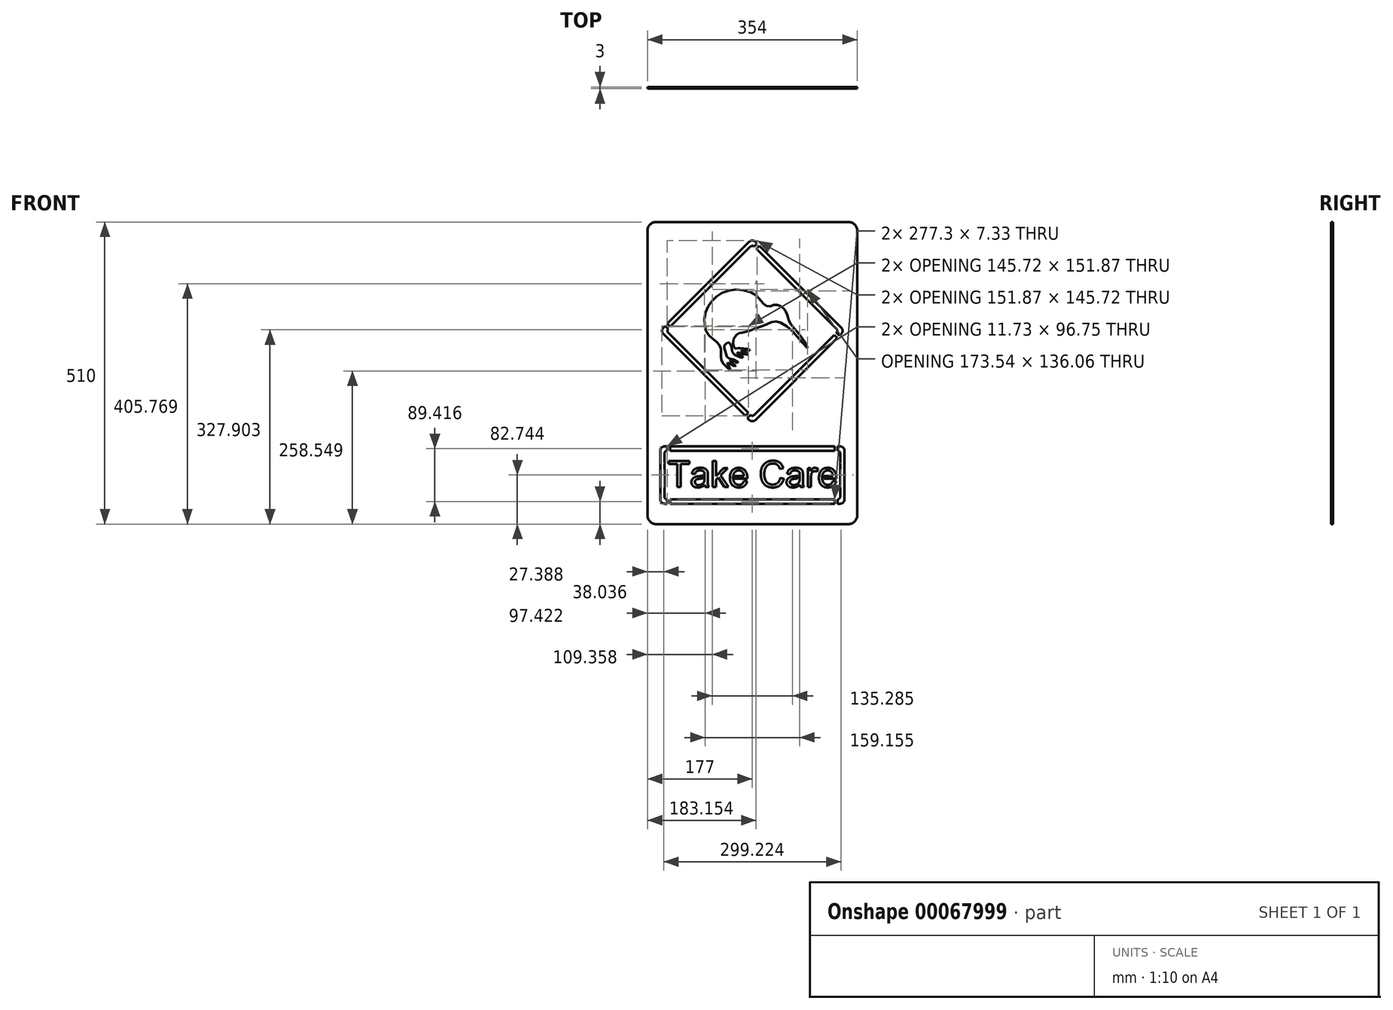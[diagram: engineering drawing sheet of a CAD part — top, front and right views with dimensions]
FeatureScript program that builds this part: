
annotation { "Feature Type Name" : "Feature", "Feature Type Description" : "" }
export const myFeature = defineFeature(function(context is Context, id is Id, definition is map)
    precondition{}
    {
        {
            var Q0;
            Q0=qCreatedBy(makeId("Front.planeOp"),FACE);
            var sketch = newSketch(context, id + "F0", { "sketchPlane" : qUnion([Q0])});
            skLineSegment(sketch, "E0", {"start": v(-162, 255) * mm, "end": v(162, 255) * mm});
            skArc(sketch, "E1", {"start": v(-162, 255) * mm, "mid": v(-172.6, 250.6) * mm, "end": v(-177, 240) * mm});
            skLineSegment(sketch, "E2", {"start": v(-177, -240) * mm, "end": v(-177, 240) * mm});
            skArc(sketch, "E3", {"start": v(-177, -240) * mm, "mid": v(-172.6, -250.6) * mm, "end": v(-162, -255) * mm});
            skLineSegment(sketch, "E4", {"start": v(-162, -255) * mm, "end": v(162, -255) * mm});
            skArc(sketch, "E5", {"start": v(162, -255) * mm, "mid": v(172.6, -250.6) * mm, "end": v(177, -240) * mm});
            skLineSegment(sketch, "E6", {"start": v(177, -240) * mm, "end": v(177, 240) * mm});
            skArc(sketch, "E7", {"start": v(177, 240) * mm, "mid": v(172.6, 250.6) * mm, "end": v(162, 255) * mm});
            skLineSegment(sketch, "E8", {"start": v(121.2, -173.58) * mm, "end": v(136, -173.58) * mm});
            skLineSegment(sketch, "E9", {"start": v(136, -173.58) * mm, "end": v(135.95, -173.09) * mm});
            skLineSegment(sketch, "E10", {"start": v(135.95, -173.09) * mm, "end": v(135.9, -172.61) * mm});
            skLineSegment(sketch, "E11", {"start": v(135.9, -172.61) * mm, "end": v(135.82, -172.15) * mm});
            skLineSegment(sketch, "E12", {"start": v(135.82, -172.15) * mm, "end": v(135.74, -171.7) * mm});
            skLineSegment(sketch, "E13", {"start": v(135.74, -171.7) * mm, "end": v(135.65, -171.27) * mm});
            skLineSegment(sketch, "E14", {"start": v(135.65, -171.27) * mm, "end": v(135.55, -170.85) * mm});
            skLineSegment(sketch, "E15", {"start": v(135.55, -170.85) * mm, "end": v(135.44, -170.45) * mm});
            skLineSegment(sketch, "E16", {"start": v(135.44, -170.45) * mm, "end": v(135.31, -170.07) * mm});
            skLineSegment(sketch, "E17", {"start": v(135.31, -170.07) * mm, "end": v(135.18, -169.7) * mm});
            skLineSegment(sketch, "E18", {"start": v(135.18, -169.7) * mm, "end": v(135.04, -169.34) * mm});
            skLineSegment(sketch, "E19", {"start": v(135.04, -169.34) * mm, "end": v(134.89, -169) * mm});
            skLineSegment(sketch, "E20", {"start": v(134.89, -169) * mm, "end": v(134.72, -168.69) * mm});
            skLineSegment(sketch, "E21", {"start": v(134.72, -168.69) * mm, "end": v(134.55, -168.38) * mm});
            skLineSegment(sketch, "E22", {"start": v(134.55, -168.38) * mm, "end": v(134.36, -168.09) * mm});
            skLineSegment(sketch, "E23", {"start": v(134.36, -168.09) * mm, "end": v(134.17, -167.81) * mm});
            skLineSegment(sketch, "E24", {"start": v(134.17, -167.81) * mm, "end": v(133.96, -167.55) * mm});
            skLineSegment(sketch, "E25", {"start": v(133.96, -167.55) * mm, "end": v(133.64, -167.18) * mm});
            skLineSegment(sketch, "E26", {"start": v(133.64, -167.18) * mm, "end": v(133.3, -166.82) * mm});
            skLineSegment(sketch, "E27", {"start": v(133.3, -166.82) * mm, "end": v(132.94, -166.5) * mm});
            skLineSegment(sketch, "E28", {"start": v(132.94, -166.5) * mm, "end": v(132.58, -166.2) * mm});
            skLineSegment(sketch, "E29", {"start": v(132.58, -166.2) * mm, "end": v(132.2, -165.9) * mm});
            skLineSegment(sketch, "E30", {"start": v(132.2, -165.9) * mm, "end": v(131.82, -165.65) * mm});
            skLineSegment(sketch, "E31", {"start": v(131.82, -165.65) * mm, "end": v(131.41, -165.42) * mm});
            skLineSegment(sketch, "E32", {"start": v(131.41, -165.42) * mm, "end": v(131, -165.22) * mm});
            skLineSegment(sketch, "E33", {"start": v(131, -165.22) * mm, "end": v(130.58, -165.03) * mm});
            skLineSegment(sketch, "E34", {"start": v(130.58, -165.03) * mm, "end": v(130.14, -164.87) * mm});
            skLineSegment(sketch, "E35", {"start": v(130.14, -164.87) * mm, "end": v(129.7, -164.74) * mm});
            skLineSegment(sketch, "E36", {"start": v(129.7, -164.74) * mm, "end": v(129.23, -164.63) * mm});
            skLineSegment(sketch, "E37", {"start": v(129.23, -164.63) * mm, "end": v(128.76, -164.54) * mm});
            skLineSegment(sketch, "E38", {"start": v(128.76, -164.54) * mm, "end": v(128.28, -164.48) * mm});
            skLineSegment(sketch, "E39", {"start": v(128.28, -164.48) * mm, "end": v(127.78, -164.45) * mm});
            skLineSegment(sketch, "E40", {"start": v(127.78, -164.45) * mm, "end": v(127.28, -164.44) * mm});
            skLineSegment(sketch, "E41", {"start": v(127.28, -164.44) * mm, "end": v(126.82, -164.44) * mm});
            skLineSegment(sketch, "E42", {"start": v(126.82, -164.44) * mm, "end": v(126.36, -164.47) * mm});
            skLineSegment(sketch, "E43", {"start": v(126.36, -164.47) * mm, "end": v(125.92, -164.52) * mm});
            skLineSegment(sketch, "E44", {"start": v(125.92, -164.52) * mm, "end": v(125.49, -164.6) * mm});
            skLineSegment(sketch, "E45", {"start": v(125.49, -164.6) * mm, "end": v(125.07, -164.68) * mm});
            skLineSegment(sketch, "E46", {"start": v(125.07, -164.68) * mm, "end": v(124.65, -164.79) * mm});
            skLineSegment(sketch, "E47", {"start": v(124.65, -164.79) * mm, "end": v(124.25, -164.91) * mm});
            skLineSegment(sketch, "E48", {"start": v(124.25, -164.91) * mm, "end": v(123.85, -165.06) * mm});
            skLineSegment(sketch, "E49", {"start": v(123.85, -165.06) * mm, "end": v(123.47, -165.22) * mm});
            skLineSegment(sketch, "E50", {"start": v(123.47, -165.22) * mm, "end": v(123.09, -165.4) * mm});
            skLineSegment(sketch, "E51", {"start": v(123.09, -165.4) * mm, "end": v(122.72, -165.61) * mm});
            skLineSegment(sketch, "E52", {"start": v(122.72, -165.61) * mm, "end": v(122.36, -165.84) * mm});
            skLineSegment(sketch, "E53", {"start": v(122.36, -165.84) * mm, "end": v(122.01, -166.08) * mm});
            skLineSegment(sketch, "E54", {"start": v(122.01, -166.08) * mm, "end": v(121.67, -166.34) * mm});
            skLineSegment(sketch, "E55", {"start": v(121.67, -166.34) * mm, "end": v(121.34, -166.62) * mm});
            skLineSegment(sketch, "E56", {"start": v(121.34, -166.62) * mm, "end": v(121.02, -166.92) * mm});
            skLineSegment(sketch, "E57", {"start": v(121.02, -166.92) * mm, "end": v(120.71, -167.24) * mm});
            skLineSegment(sketch, "E58", {"start": v(120.71, -167.24) * mm, "end": v(120.42, -167.57) * mm});
            skLineSegment(sketch, "E59", {"start": v(120.42, -167.57) * mm, "end": v(120.15, -167.92) * mm});
            skLineSegment(sketch, "E60", {"start": v(120.15, -167.92) * mm, "end": v(119.9, -168.27) * mm});
            skLineSegment(sketch, "E61", {"start": v(119.9, -168.27) * mm, "end": v(119.66, -168.65) * mm});
            skLineSegment(sketch, "E62", {"start": v(119.66, -168.65) * mm, "end": v(119.44, -169.03) * mm});
            skLineSegment(sketch, "E63", {"start": v(119.44, -169.03) * mm, "end": v(119.24, -169.42) * mm});
            skLineSegment(sketch, "E64", {"start": v(119.24, -169.42) * mm, "end": v(119.05, -169.83) * mm});
            skArc(sketch, "E65", {"start": v(119.05, -169.83) * mm, "mid": v(117.86, -176.49) * mm, "end": v(119, -183.15) * mm});
            skLineSegment(sketch, "E66", {"start": v(119, -183.15) * mm, "end": v(119.45, -184.08) * mm});
            skLineSegment(sketch, "E67", {"start": v(119.45, -184.08) * mm, "end": v(119.7, -184.51) * mm});
            skLineSegment(sketch, "E68", {"start": v(119.7, -184.51) * mm, "end": v(119.97, -184.93) * mm});
            skLineSegment(sketch, "E69", {"start": v(119.97, -184.93) * mm, "end": v(120.26, -185.33) * mm});
            skLineSegment(sketch, "E70", {"start": v(120.26, -185.33) * mm, "end": v(120.56, -185.7) * mm});
            skLineSegment(sketch, "E71", {"start": v(120.56, -185.7) * mm, "end": v(120.89, -186.06) * mm});
            skLineSegment(sketch, "E72", {"start": v(120.89, -186.06) * mm, "end": v(121.23, -186.4) * mm});
            skLineSegment(sketch, "E73", {"start": v(121.23, -186.4) * mm, "end": v(121.57, -186.72) * mm});
            skLineSegment(sketch, "E74", {"start": v(121.57, -186.72) * mm, "end": v(121.93, -187.01) * mm});
            skLineSegment(sketch, "E75", {"start": v(121.93, -187.01) * mm, "end": v(122.3, -187.28) * mm});
            skLineSegment(sketch, "E76", {"start": v(122.3, -187.28) * mm, "end": v(122.68, -187.53) * mm});
            skLineSegment(sketch, "E77", {"start": v(122.68, -187.53) * mm, "end": v(123.07, -187.76) * mm});
            skLineSegment(sketch, "E78", {"start": v(123.07, -187.76) * mm, "end": v(123.48, -187.97) * mm});
            skLineSegment(sketch, "E79", {"start": v(123.48, -187.97) * mm, "end": v(123.89, -188.16) * mm});
            skLineSegment(sketch, "E80", {"start": v(123.89, -188.16) * mm, "end": v(124.3, -188.32) * mm});
            skLineSegment(sketch, "E81", {"start": v(124.3, -188.32) * mm, "end": v(124.74, -188.46) * mm});
            skLineSegment(sketch, "E82", {"start": v(124.74, -188.46) * mm, "end": v(125.18, -188.58) * mm});
            skLineSegment(sketch, "E83", {"start": v(125.18, -188.58) * mm, "end": v(125.63, -188.68) * mm});
            skLineSegment(sketch, "E84", {"start": v(125.63, -188.68) * mm, "end": v(126.1, -188.75) * mm});
            skLineSegment(sketch, "E85", {"start": v(126.1, -188.75) * mm, "end": v(126.57, -188.8) * mm});
            skLineSegment(sketch, "E86", {"start": v(126.57, -188.8) * mm, "end": v(127.05, -188.84) * mm});
            skLineSegment(sketch, "E87", {"start": v(127.05, -188.84) * mm, "end": v(127.55, -188.85) * mm});
            skLineSegment(sketch, "E88", {"start": v(127.55, -188.85) * mm, "end": v(128.27, -188.83) * mm});
            skLineSegment(sketch, "E89", {"start": v(128.27, -188.83) * mm, "end": v(128.98, -188.75) * mm});
            skLineSegment(sketch, "E90", {"start": v(128.98, -188.75) * mm, "end": v(129.65, -188.63) * mm});
            skLineSegment(sketch, "E91", {"start": v(129.65, -188.63) * mm, "end": v(130.3, -188.46) * mm});
            skLineSegment(sketch, "E92", {"start": v(130.3, -188.46) * mm, "end": v(130.92, -188.24) * mm});
            skLineSegment(sketch, "E93", {"start": v(130.92, -188.24) * mm, "end": v(131.51, -187.98) * mm});
            skLineSegment(sketch, "E94", {"start": v(131.51, -187.98) * mm, "end": v(132.08, -187.66) * mm});
            skLineSegment(sketch, "E95", {"start": v(132.08, -187.66) * mm, "end": v(132.62, -187.3) * mm});
            skLineSegment(sketch, "E96", {"start": v(132.62, -187.3) * mm, "end": v(133.13, -186.87) * mm});
            skLineSegment(sketch, "E97", {"start": v(133.13, -186.87) * mm, "end": v(133.61, -186.4) * mm});
            skLineSegment(sketch, "E98", {"start": v(133.61, -186.4) * mm, "end": v(134.07, -185.86) * mm});
            skLineSegment(sketch, "E99", {"start": v(134.07, -185.86) * mm, "end": v(134.5, -185.27) * mm});
            skLineSegment(sketch, "E100", {"start": v(134.5, -185.27) * mm, "end": v(134.9, -184.62) * mm});
            skLineSegment(sketch, "E101", {"start": v(134.9, -184.62) * mm, "end": v(135.28, -183.9) * mm});
            skLineSegment(sketch, "E102", {"start": v(135.28, -183.9) * mm, "end": v(135.62, -183.14) * mm});
            skLineSegment(sketch, "E103", {"start": v(135.62, -183.14) * mm, "end": v(135.94, -182.31) * mm});
            skLineSegment(sketch, "E104", {"start": v(135.94, -182.31) * mm, "end": v(141.52, -183) * mm});
            skLineSegment(sketch, "E105", {"start": v(141.52, -183) * mm, "end": v(141.35, -183.6) * mm});
            skLineSegment(sketch, "E106", {"start": v(141.35, -183.6) * mm, "end": v(141.16, -184.2) * mm});
            skLineSegment(sketch, "E107", {"start": v(141.16, -184.2) * mm, "end": v(140.95, -184.76) * mm});
            skLineSegment(sketch, "E108", {"start": v(140.95, -184.76) * mm, "end": v(140.72, -185.31) * mm});
            skLineSegment(sketch, "E109", {"start": v(140.72, -185.31) * mm, "end": v(140.48, -185.85) * mm});
            skLineSegment(sketch, "E110", {"start": v(140.48, -185.85) * mm, "end": v(140.22, -186.36) * mm});
            skLineSegment(sketch, "E111", {"start": v(140.22, -186.36) * mm, "end": v(139.94, -186.86) * mm});
            skLineSegment(sketch, "E112", {"start": v(139.94, -186.86) * mm, "end": v(139.64, -187.35) * mm});
            skLineSegment(sketch, "E113", {"start": v(139.64, -187.35) * mm, "end": v(139.33, -187.81) * mm});
            skLineSegment(sketch, "E114", {"start": v(139.33, -187.81) * mm, "end": v(139, -188.26) * mm});
            skLineSegment(sketch, "E115", {"start": v(139, -188.26) * mm, "end": v(138.65, -188.7) * mm});
            skLineSegment(sketch, "E116", {"start": v(138.65, -188.7) * mm, "end": v(138.28, -189.1) * mm});
            skLineSegment(sketch, "E117", {"start": v(138.28, -189.1) * mm, "end": v(137.9, -189.5) * mm});
            skLineSegment(sketch, "E118", {"start": v(137.9, -189.5) * mm, "end": v(137.5, -189.88) * mm});
            skLineSegment(sketch, "E119", {"start": v(137.5, -189.88) * mm, "end": v(137.07, -190.25) * mm});
            skLineSegment(sketch, "E120", {"start": v(137.07, -190.25) * mm, "end": v(136.63, -190.6) * mm});
            skLineSegment(sketch, "E121", {"start": v(136.63, -190.6) * mm, "end": v(136.18, -190.92) * mm});
            skLineSegment(sketch, "E122", {"start": v(136.18, -190.92) * mm, "end": v(135.71, -191.23) * mm});
            skLineSegment(sketch, "E123", {"start": v(135.71, -191.23) * mm, "end": v(135.23, -191.5) * mm});
            skLineSegment(sketch, "E124", {"start": v(135.23, -191.5) * mm, "end": v(134.73, -191.77) * mm});
            skLineSegment(sketch, "E125", {"start": v(134.73, -191.77) * mm, "end": v(134.21, -192.02) * mm});
            skLineSegment(sketch, "E126", {"start": v(134.21, -192.02) * mm, "end": v(133.68, -192.24) * mm});
            skLineSegment(sketch, "E127", {"start": v(133.68, -192.24) * mm, "end": v(133.13, -192.44) * mm});
            skLineSegment(sketch, "E128", {"start": v(133.13, -192.44) * mm, "end": v(132.57, -192.62) * mm});
            skLineSegment(sketch, "E129", {"start": v(132.57, -192.62) * mm, "end": v(132, -192.78) * mm});
            skLineSegment(sketch, "E130", {"start": v(132, -192.78) * mm, "end": v(131.4, -192.91) * mm});
            skLineSegment(sketch, "E131", {"start": v(131.4, -192.91) * mm, "end": v(130.8, -193.03) * mm});
            skLineSegment(sketch, "E132", {"start": v(130.8, -193.03) * mm, "end": v(130.17, -193.12) * mm});
            skLineSegment(sketch, "E133", {"start": v(130.17, -193.12) * mm, "end": v(129.53, -193.2) * mm});
            skLineSegment(sketch, "E134", {"start": v(129.53, -193.2) * mm, "end": v(128.87, -193.25) * mm});
            skLineSegment(sketch, "E135", {"start": v(128.87, -193.25) * mm, "end": v(128.2, -193.28) * mm});
            skLineSegment(sketch, "E136", {"start": v(128.2, -193.28) * mm, "end": v(127.52, -193.3) * mm});
            skLineSegment(sketch, "E137", {"start": v(127.52, -193.3) * mm, "end": v(126.65, -193.28) * mm});
            skLineSegment(sketch, "E138", {"start": v(126.65, -193.28) * mm, "end": v(125.81, -193.22) * mm});
            skLineSegment(sketch, "E139", {"start": v(125.81, -193.22) * mm, "end": v(125, -193.14) * mm});
            skLineSegment(sketch, "E140", {"start": v(125, -193.14) * mm, "end": v(124.2, -193.02) * mm});
            skLineSegment(sketch, "E141", {"start": v(124.2, -193.02) * mm, "end": v(123.43, -192.87) * mm});
            skLineSegment(sketch, "E142", {"start": v(123.43, -192.87) * mm, "end": v(122.68, -192.69) * mm});
            skLineSegment(sketch, "E143", {"start": v(122.68, -192.69) * mm, "end": v(121.95, -192.47) * mm});
            skLineSegment(sketch, "E144", {"start": v(121.95, -192.47) * mm, "end": v(121.25, -192.22) * mm});
            skLineSegment(sketch, "E145", {"start": v(121.25, -192.22) * mm, "end": v(120.57, -191.93) * mm});
            skLineSegment(sketch, "E146", {"start": v(120.57, -191.93) * mm, "end": v(119.9, -191.61) * mm});
            skLineSegment(sketch, "E147", {"start": v(119.9, -191.61) * mm, "end": v(119.27, -191.26) * mm});
            skLineSegment(sketch, "E148", {"start": v(119.27, -191.26) * mm, "end": v(118.66, -190.87) * mm});
            skLineSegment(sketch, "E149", {"start": v(118.66, -190.87) * mm, "end": v(118.07, -190.45) * mm});
            skLineSegment(sketch, "E150", {"start": v(118.07, -190.45) * mm, "end": v(117.5, -190) * mm});
            skLineSegment(sketch, "E151", {"start": v(117.5, -190) * mm, "end": v(116.96, -189.5) * mm});
            skLineSegment(sketch, "E152", {"start": v(116.96, -189.5) * mm, "end": v(116.43, -188.99) * mm});
            skLineSegment(sketch, "E153", {"start": v(116.43, -188.99) * mm, "end": v(115.94, -188.44) * mm});
            skLineSegment(sketch, "E154", {"start": v(115.94, -188.44) * mm, "end": v(115.47, -187.86) * mm});
            skLineSegment(sketch, "E155", {"start": v(115.47, -187.86) * mm, "end": v(115.04, -187.25) * mm});
            skLineSegment(sketch, "E156", {"start": v(115.04, -187.25) * mm, "end": v(114.64, -186.62) * mm});
            skLineSegment(sketch, "E157", {"start": v(114.64, -186.62) * mm, "end": v(114.27, -185.96) * mm});
            skLineSegment(sketch, "E158", {"start": v(114.27, -185.96) * mm, "end": v(113.94, -185.27) * mm});
            skLineSegment(sketch, "E159", {"start": v(113.94, -185.27) * mm, "end": v(113.63, -184.56) * mm});
            skLineSegment(sketch, "E160", {"start": v(113.63, -184.56) * mm, "end": v(113.36, -183.82) * mm});
            skLineSegment(sketch, "E161", {"start": v(113.36, -183.82) * mm, "end": v(113.12, -183.05) * mm});
            skLineSegment(sketch, "E162", {"start": v(113.12, -183.05) * mm, "end": v(112.91, -182.25) * mm});
            skLineSegment(sketch, "E163", {"start": v(112.91, -182.25) * mm, "end": v(112.74, -181.43) * mm});
            skLineSegment(sketch, "E164", {"start": v(112.74, -181.43) * mm, "end": v(112.6, -180.58) * mm});
            skLineSegment(sketch, "E165", {"start": v(112.6, -180.58) * mm, "end": v(112.48, -179.7) * mm});
            skLineSegment(sketch, "E166", {"start": v(112.48, -179.7) * mm, "end": v(112.4, -178.8) * mm});
            skLineSegment(sketch, "E167", {"start": v(112.4, -178.8) * mm, "end": v(112.35, -177.87) * mm});
            skLineSegment(sketch, "E168", {"start": v(112.35, -177.87) * mm, "end": v(112.34, -176.91) * mm});
            skLineSegment(sketch, "E169", {"start": v(112.34, -176.91) * mm, "end": v(112.35, -175.92) * mm});
            skLineSegment(sketch, "E170", {"start": v(112.35, -175.92) * mm, "end": v(112.4, -174.96) * mm});
            skLineSegment(sketch, "E171", {"start": v(112.4, -174.96) * mm, "end": v(112.48, -174.03) * mm});
            skLineSegment(sketch, "E172", {"start": v(112.48, -174.03) * mm, "end": v(112.6, -173.12) * mm});
            skLineSegment(sketch, "E173", {"start": v(112.6, -173.12) * mm, "end": v(112.74, -172.24) * mm});
            skLineSegment(sketch, "E174", {"start": v(112.74, -172.24) * mm, "end": v(112.92, -171.4) * mm});
            skLineSegment(sketch, "E175", {"start": v(112.92, -171.4) * mm, "end": v(113.13, -170.57) * mm});
            skLineSegment(sketch, "E176", {"start": v(113.13, -170.57) * mm, "end": v(113.37, -169.77) * mm});
            skLineSegment(sketch, "E177", {"start": v(113.37, -169.77) * mm, "end": v(113.65, -169) * mm});
            skLineSegment(sketch, "E178", {"start": v(113.65, -169) * mm, "end": v(113.95, -168.27) * mm});
            skLineSegment(sketch, "E179", {"start": v(113.95, -168.27) * mm, "end": v(114.3, -167.56) * mm});
            skLineSegment(sketch, "E180", {"start": v(114.3, -167.56) * mm, "end": v(114.67, -166.88) * mm});
            skLineSegment(sketch, "E181", {"start": v(114.67, -166.88) * mm, "end": v(115.07, -166.23) * mm});
            skLineSegment(sketch, "E182", {"start": v(115.07, -166.23) * mm, "end": v(115.5, -165.6) * mm});
            skLineSegment(sketch, "E183", {"start": v(115.5, -165.6) * mm, "end": v(115.98, -165) * mm});
            skLineSegment(sketch, "E184", {"start": v(115.98, -165) * mm, "end": v(116.48, -164.44) * mm});
            skLineSegment(sketch, "E185", {"start": v(116.48, -164.44) * mm, "end": v(117, -163.9) * mm});
            skLineSegment(sketch, "E186", {"start": v(117, -163.9) * mm, "end": v(117.55, -163.4) * mm});
            skLineSegment(sketch, "E187", {"start": v(117.55, -163.4) * mm, "end": v(118.12, -162.93) * mm});
            skLineSegment(sketch, "E188", {"start": v(118.12, -162.93) * mm, "end": v(118.7, -162.5) * mm});
            skLineSegment(sketch, "E189", {"start": v(118.7, -162.5) * mm, "end": v(119.3, -162.1) * mm});
            skLineSegment(sketch, "E190", {"start": v(119.3, -162.1) * mm, "end": v(119.93, -161.73) * mm});
            skLineSegment(sketch, "E191", {"start": v(119.93, -161.73) * mm, "end": v(120.57, -161.4) * mm});
            skLineSegment(sketch, "E192", {"start": v(120.57, -161.4) * mm, "end": v(121.23, -161.1) * mm});
            skLineSegment(sketch, "E193", {"start": v(121.23, -161.1) * mm, "end": v(121.91, -160.85) * mm});
            skLineSegment(sketch, "E194", {"start": v(121.91, -160.85) * mm, "end": v(122.61, -160.62) * mm});
            skLineSegment(sketch, "E195", {"start": v(122.61, -160.62) * mm, "end": v(123.33, -160.43) * mm});
            skLineSegment(sketch, "E196", {"start": v(123.33, -160.43) * mm, "end": v(124.07, -160.27) * mm});
            skLineSegment(sketch, "E197", {"start": v(124.07, -160.27) * mm, "end": v(124.83, -160.15) * mm});
            skLineSegment(sketch, "E198", {"start": v(124.83, -160.15) * mm, "end": v(125.6, -160.07) * mm});
            skLineSegment(sketch, "E199", {"start": v(125.6, -160.07) * mm, "end": v(126.4, -160.01) * mm});
            skLineSegment(sketch, "E200", {"start": v(126.4, -160.01) * mm, "end": v(127.22, -160) * mm});
            skLineSegment(sketch, "E201", {"start": v(127.22, -160) * mm, "end": v(128, -160.01) * mm});
            skLineSegment(sketch, "E202", {"start": v(128, -160.01) * mm, "end": v(128.78, -160.06) * mm});
            skLineSegment(sketch, "E203", {"start": v(128.78, -160.06) * mm, "end": v(129.53, -160.15) * mm});
            skLineSegment(sketch, "E204", {"start": v(129.53, -160.15) * mm, "end": v(130.26, -160.27) * mm});
            skLineSegment(sketch, "E205", {"start": v(130.26, -160.27) * mm, "end": v(130.98, -160.42) * mm});
            skLineSegment(sketch, "E206", {"start": v(130.98, -160.42) * mm, "end": v(131.68, -160.6) * mm});
            skLineSegment(sketch, "E207", {"start": v(131.68, -160.6) * mm, "end": v(132.36, -160.83) * mm});
            skLineSegment(sketch, "E208", {"start": v(132.36, -160.83) * mm, "end": v(133.02, -161.08) * mm});
            skLineSegment(sketch, "E209", {"start": v(133.02, -161.08) * mm, "end": v(133.66, -161.37) * mm});
            skLineSegment(sketch, "E210", {"start": v(133.66, -161.37) * mm, "end": v(134.29, -161.7) * mm});
            skLineSegment(sketch, "E211", {"start": v(134.29, -161.7) * mm, "end": v(134.9, -162.05) * mm});
            skLineSegment(sketch, "E212", {"start": v(134.9, -162.05) * mm, "end": v(135.48, -162.44) * mm});
            skLineSegment(sketch, "E213", {"start": v(135.48, -162.44) * mm, "end": v(136.05, -162.87) * mm});
            skLineSegment(sketch, "E214", {"start": v(136.05, -162.87) * mm, "end": v(136.6, -163.33) * mm});
            skLineSegment(sketch, "E215", {"start": v(136.6, -163.33) * mm, "end": v(137.14, -163.82) * mm});
            skLineSegment(sketch, "E216", {"start": v(137.14, -163.82) * mm, "end": v(137.65, -164.35) * mm});
            skLineSegment(sketch, "E217", {"start": v(137.65, -164.35) * mm, "end": v(138.14, -164.9) * mm});
            skLineSegment(sketch, "E218", {"start": v(138.14, -164.9) * mm, "end": v(138.6, -165.49) * mm});
            skLineSegment(sketch, "E219", {"start": v(138.6, -165.49) * mm, "end": v(139.03, -166.1) * mm});
            skLineSegment(sketch, "E220", {"start": v(139.03, -166.1) * mm, "end": v(139.43, -166.74) * mm});
            skLineSegment(sketch, "E221", {"start": v(139.43, -166.74) * mm, "end": v(139.8, -167.4) * mm});
            skLineSegment(sketch, "E222", {"start": v(139.8, -167.4) * mm, "end": v(140.12, -168.1) * mm});
            skLineSegment(sketch, "E223", {"start": v(140.12, -168.1) * mm, "end": v(140.42, -168.83) * mm});
            skLineSegment(sketch, "E224", {"start": v(140.42, -168.83) * mm, "end": v(140.7, -169.58) * mm});
            skLineSegment(sketch, "E225", {"start": v(140.7, -169.58) * mm, "end": v(140.93, -170.36) * mm});
            skLineSegment(sketch, "E226", {"start": v(140.93, -170.36) * mm, "end": v(141.13, -171.16) * mm});
            skLineSegment(sketch, "E227", {"start": v(141.13, -171.16) * mm, "end": v(141.3, -172) * mm});
            skLineSegment(sketch, "E228", {"start": v(141.3, -172) * mm, "end": v(141.45, -172.86) * mm});
            skLineSegment(sketch, "E229", {"start": v(141.45, -172.86) * mm, "end": v(141.56, -173.75) * mm});
            skLineSegment(sketch, "E230", {"start": v(141.56, -173.75) * mm, "end": v(141.64, -174.67) * mm});
            skLineSegment(sketch, "E231", {"start": v(141.64, -174.67) * mm, "end": v(141.69, -175.61) * mm});
            skLineSegment(sketch, "E232", {"start": v(141.69, -175.61) * mm, "end": v(141.7, -176.58) * mm});
            skLineSegment(sketch, "E233", {"start": v(141.7, -176.58) * mm, "end": v(141.7, -176.85) * mm});
            skLineSegment(sketch, "E234", {"start": v(141.7, -176.85) * mm, "end": v(141.7, -177.18) * mm});
            skLineSegment(sketch, "E235", {"start": v(141.7, -177.18) * mm, "end": v(141.69, -177.57) * mm});
            skLineSegment(sketch, "E236", {"start": v(141.69, -177.57) * mm, "end": v(141.67, -178.02) * mm});
            skLineSegment(sketch, "E237", {"start": v(141.67, -178.02) * mm, "end": v(120.99, -178.02) * mm});
            skArc(sketch, "E238", {"start": v(121.2, -173.58) * mm, "mid": v(120.94, -175.8) * mm, "end": v(120.99, -178.02) * mm});
            skLineSegment(sketch, "E239", {"start": v(80.37, -189.2) * mm, "end": v(80.3, -188.64) * mm});
            skLineSegment(sketch, "E240", {"start": v(80.3, -188.64) * mm, "end": v(79.55, -189.26) * mm});
            skLineSegment(sketch, "E241", {"start": v(79.55, -189.26) * mm, "end": v(78.82, -189.82) * mm});
            skLineSegment(sketch, "E242", {"start": v(78.82, -189.82) * mm, "end": v(78.08, -190.34) * mm});
            skLineSegment(sketch, "E243", {"start": v(78.08, -190.34) * mm, "end": v(77.36, -190.82) * mm});
            skLineSegment(sketch, "E244", {"start": v(77.36, -190.82) * mm, "end": v(76.64, -191.24) * mm});
            skLineSegment(sketch, "E245", {"start": v(76.64, -191.24) * mm, "end": v(75.93, -191.62) * mm});
            skLineSegment(sketch, "E246", {"start": v(75.93, -191.62) * mm, "end": v(75.22, -191.96) * mm});
            skLineSegment(sketch, "E247", {"start": v(75.22, -191.96) * mm, "end": v(74.53, -192.24) * mm});
            skLineSegment(sketch, "E248", {"start": v(74.53, -192.24) * mm, "end": v(73.83, -192.49) * mm});
            skLineSegment(sketch, "E249", {"start": v(73.83, -192.49) * mm, "end": v(73.11, -192.7) * mm});
            skLineSegment(sketch, "E250", {"start": v(73.11, -192.7) * mm, "end": v(72.39, -192.88) * mm});
            skLineSegment(sketch, "E251", {"start": v(72.39, -192.88) * mm, "end": v(71.65, -193.03) * mm});
            skLineSegment(sketch, "E252", {"start": v(71.65, -193.03) * mm, "end": v(70.9, -193.14) * mm});
            skLineSegment(sketch, "E253", {"start": v(70.9, -193.14) * mm, "end": v(70.14, -193.23) * mm});
            skLineSegment(sketch, "E254", {"start": v(70.14, -193.23) * mm, "end": v(69.36, -193.28) * mm});
            skLineSegment(sketch, "E255", {"start": v(69.36, -193.28) * mm, "end": v(68.57, -193.3) * mm});
            skLineSegment(sketch, "E256", {"start": v(68.57, -193.3) * mm, "end": v(67.93, -193.28) * mm});
            skLineSegment(sketch, "E257", {"start": v(67.93, -193.28) * mm, "end": v(67.3, -193.25) * mm});
            skLineSegment(sketch, "E258", {"start": v(67.3, -193.25) * mm, "end": v(66.69, -193.2) * mm});
            skLineSegment(sketch, "E259", {"start": v(66.69, -193.2) * mm, "end": v(66.1, -193.13) * mm});
            skLineSegment(sketch, "E260", {"start": v(66.1, -193.13) * mm, "end": v(65.53, -193.04) * mm});
            skLineSegment(sketch, "E261", {"start": v(65.53, -193.04) * mm, "end": v(64.98, -192.93) * mm});
            skLineSegment(sketch, "E262", {"start": v(64.98, -192.93) * mm, "end": v(64.44, -192.8) * mm});
            skLineSegment(sketch, "E263", {"start": v(64.44, -192.8) * mm, "end": v(63.93, -192.65) * mm});
            skLineSegment(sketch, "E264", {"start": v(63.93, -192.65) * mm, "end": v(63.44, -192.48) * mm});
            skLineSegment(sketch, "E265", {"start": v(63.44, -192.48) * mm, "end": v(62.96, -192.3) * mm});
            skLineSegment(sketch, "E266", {"start": v(62.96, -192.3) * mm, "end": v(62.5, -192.08) * mm});
            skLineSegment(sketch, "E267", {"start": v(62.5, -192.08) * mm, "end": v(62.06, -191.85) * mm});
            skLineSegment(sketch, "E268", {"start": v(62.06, -191.85) * mm, "end": v(61.65, -191.6) * mm});
            skLineSegment(sketch, "E269", {"start": v(61.65, -191.6) * mm, "end": v(61.25, -191.33) * mm});
            skLineSegment(sketch, "E270", {"start": v(61.25, -191.33) * mm, "end": v(60.87, -191.04) * mm});
            skLineSegment(sketch, "E271", {"start": v(60.87, -191.04) * mm, "end": v(60.5, -190.73) * mm});
            skLineSegment(sketch, "E272", {"start": v(60.5, -190.73) * mm, "end": v(60.16, -190.4) * mm});
            skLineSegment(sketch, "E273", {"start": v(60.16, -190.4) * mm, "end": v(59.84, -190.06) * mm});
            skLineSegment(sketch, "E274", {"start": v(59.84, -190.06) * mm, "end": v(59.54, -189.72) * mm});
            skLineSegment(sketch, "E275", {"start": v(59.54, -189.72) * mm, "end": v(59.27, -189.36) * mm});
            skLineSegment(sketch, "E276", {"start": v(59.27, -189.36) * mm, "end": v(59.02, -188.99) * mm});
            skLineSegment(sketch, "E277", {"start": v(59.02, -188.99) * mm, "end": v(58.78, -188.6) * mm});
            skLineSegment(sketch, "E278", {"start": v(58.78, -188.6) * mm, "end": v(58.58, -188.21) * mm});
            skLineSegment(sketch, "E279", {"start": v(58.58, -188.21) * mm, "end": v(58.39, -187.8) * mm});
            skLineSegment(sketch, "E280", {"start": v(58.39, -187.8) * mm, "end": v(58.22, -187.4) * mm});
            skLineSegment(sketch, "E281", {"start": v(58.22, -187.4) * mm, "end": v(58.08, -186.96) * mm});
            skLineSegment(sketch, "E282", {"start": v(58.08, -186.96) * mm, "end": v(57.96, -186.53) * mm});
            skLineSegment(sketch, "E283", {"start": v(57.96, -186.53) * mm, "end": v(57.86, -186.08) * mm});
            skLineSegment(sketch, "E284", {"start": v(57.86, -186.08) * mm, "end": v(57.78, -185.62) * mm});
            skLineSegment(sketch, "E285", {"start": v(57.78, -185.62) * mm, "end": v(57.73, -185.15) * mm});
            skLineSegment(sketch, "E286", {"start": v(57.73, -185.15) * mm, "end": v(57.7, -184.67) * mm});
            skLineSegment(sketch, "E287", {"start": v(57.7, -184.67) * mm, "end": v(57.68, -184.17) * mm});
            skLineSegment(sketch, "E288", {"start": v(57.68, -184.17) * mm, "end": v(57.7, -183.6) * mm});
            skLineSegment(sketch, "E289", {"start": v(57.7, -183.6) * mm, "end": v(57.75, -183.03) * mm});
            skLineSegment(sketch, "E290", {"start": v(57.75, -183.03) * mm, "end": v(57.83, -182.48) * mm});
            skLineSegment(sketch, "E291", {"start": v(57.83, -182.48) * mm, "end": v(57.95, -181.93) * mm});
            skLineSegment(sketch, "E292", {"start": v(57.95, -181.93) * mm, "end": v(58.1, -181.4) * mm});
            skLineSegment(sketch, "E293", {"start": v(58.1, -181.4) * mm, "end": v(58.28, -180.9) * mm});
            skLineSegment(sketch, "E294", {"start": v(58.28, -180.9) * mm, "end": v(58.5, -180.39) * mm});
            skLineSegment(sketch, "E295", {"start": v(58.5, -180.39) * mm, "end": v(58.75, -179.9) * mm});
            skLineSegment(sketch, "E296", {"start": v(58.75, -179.9) * mm, "end": v(59.02, -179.43) * mm});
            skLineSegment(sketch, "E297", {"start": v(59.02, -179.43) * mm, "end": v(59.32, -178.98) * mm});
            skLineSegment(sketch, "E298", {"start": v(59.32, -178.98) * mm, "end": v(59.64, -178.55) * mm});
            skLineSegment(sketch, "E299", {"start": v(59.64, -178.55) * mm, "end": v(59.98, -178.15) * mm});
            skLineSegment(sketch, "E300", {"start": v(59.98, -178.15) * mm, "end": v(60.34, -177.78) * mm});
            skLineSegment(sketch, "E301", {"start": v(60.34, -177.78) * mm, "end": v(60.72, -177.43) * mm});
            skLineSegment(sketch, "E302", {"start": v(60.72, -177.43) * mm, "end": v(61.12, -177.1) * mm});
            skLineSegment(sketch, "E303", {"start": v(61.12, -177.1) * mm, "end": v(61.54, -176.8) * mm});
            skLineSegment(sketch, "E304", {"start": v(61.54, -176.8) * mm, "end": v(61.98, -176.51) * mm});
            skLineSegment(sketch, "E305", {"start": v(61.98, -176.51) * mm, "end": v(62.43, -176.24) * mm});
            skLineSegment(sketch, "E306", {"start": v(62.43, -176.24) * mm, "end": v(62.9, -176) * mm});
            skLineSegment(sketch, "E307", {"start": v(62.9, -176) * mm, "end": v(63.37, -175.77) * mm});
            skLineSegment(sketch, "E308", {"start": v(63.37, -175.77) * mm, "end": v(63.86, -175.55) * mm});
            skLineSegment(sketch, "E309", {"start": v(63.86, -175.55) * mm, "end": v(64.37, -175.36) * mm});
            skLineSegment(sketch, "E310", {"start": v(64.37, -175.36) * mm, "end": v(64.89, -175.18) * mm});
            skLineSegment(sketch, "E311", {"start": v(64.89, -175.18) * mm, "end": v(65.42, -175.02) * mm});
            skLineSegment(sketch, "E312", {"start": v(65.42, -175.02) * mm, "end": v(65.85, -174.92) * mm});
            skLineSegment(sketch, "E313", {"start": v(65.85, -174.92) * mm, "end": v(66.32, -174.82) * mm});
            skLineSegment(sketch, "E314", {"start": v(66.32, -174.82) * mm, "end": v(66.84, -174.71) * mm});
            skLineSegment(sketch, "E315", {"start": v(66.84, -174.71) * mm, "end": v(67.42, -174.61) * mm});
            skLineSegment(sketch, "E316", {"start": v(67.42, -174.61) * mm, "end": v(68.04, -174.51) * mm});
            skLineSegment(sketch, "E317", {"start": v(68.04, -174.51) * mm, "end": v(68.72, -174.41) * mm});
            skLineSegment(sketch, "E318", {"start": v(68.72, -174.41) * mm, "end": v(69.45, -174.31) * mm});
            skLineSegment(sketch, "E319", {"start": v(69.45, -174.31) * mm, "end": v(70.22, -174.21) * mm});
            skLineSegment(sketch, "E320", {"start": v(70.22, -174.21) * mm, "end": v(71.03, -174.12) * mm});
            skLineSegment(sketch, "E321", {"start": v(71.03, -174.12) * mm, "end": v(71.8, -174.01) * mm});
            skLineSegment(sketch, "E322", {"start": v(71.8, -174.01) * mm, "end": v(72.55, -173.91) * mm});
            skLineSegment(sketch, "E323", {"start": v(72.55, -173.91) * mm, "end": v(73.28, -173.8) * mm});
            skLineSegment(sketch, "E324", {"start": v(73.28, -173.8) * mm, "end": v(73.97, -173.7) * mm});
            skLineSegment(sketch, "E325", {"start": v(73.97, -173.7) * mm, "end": v(74.64, -173.59) * mm});
            skLineSegment(sketch, "E326", {"start": v(74.64, -173.59) * mm, "end": v(75.28, -173.47) * mm});
            skLineSegment(sketch, "E327", {"start": v(75.28, -173.47) * mm, "end": v(75.9, -173.36) * mm});
            skLineSegment(sketch, "E328", {"start": v(75.9, -173.36) * mm, "end": v(76.49, -173.24) * mm});
            skLineSegment(sketch, "E329", {"start": v(76.49, -173.24) * mm, "end": v(76.8, -173.18) * mm});
            skLineSegment(sketch, "E330", {"start": v(76.8, -177.55) * mm, "end": v(76.8, -173.18) * mm});
            skLineSegment(sketch, "E331", {"start": v(76.8, -177.55) * mm, "end": v(76.72, -177.56) * mm});
            skLineSegment(sketch, "E332", {"start": v(76.72, -177.56) * mm, "end": v(76.18, -177.7) * mm});
            skLineSegment(sketch, "E333", {"start": v(76.18, -177.7) * mm, "end": v(75.61, -177.82) * mm});
            skLineSegment(sketch, "E334", {"start": v(75.61, -177.82) * mm, "end": v(75.03, -177.94) * mm});
            skLineSegment(sketch, "E335", {"start": v(75.03, -177.94) * mm, "end": v(74.42, -178.06) * mm});
            skLineSegment(sketch, "E336", {"start": v(74.42, -178.06) * mm, "end": v(73.79, -178.18) * mm});
            skLineSegment(sketch, "E337", {"start": v(73.79, -178.18) * mm, "end": v(73.13, -178.3) * mm});
            skLineSegment(sketch, "E338", {"start": v(73.13, -178.3) * mm, "end": v(72.46, -178.4) * mm});
            skLineSegment(sketch, "E339", {"start": v(72.46, -178.4) * mm, "end": v(71.76, -178.52) * mm});
            skLineSegment(sketch, "E340", {"start": v(71.76, -178.52) * mm, "end": v(71.03, -178.62) * mm});
            skLineSegment(sketch, "E341", {"start": v(71.03, -178.62) * mm, "end": v(70.23, -178.75) * mm});
            skLineSegment(sketch, "E342", {"start": v(70.23, -178.75) * mm, "end": v(69.49, -178.87) * mm});
            skLineSegment(sketch, "E343", {"start": v(69.49, -178.87) * mm, "end": v(68.8, -179) * mm});
            skLineSegment(sketch, "E344", {"start": v(68.8, -179) * mm, "end": v(68.19, -179.13) * mm});
            skLineSegment(sketch, "E345", {"start": v(68.19, -179.13) * mm, "end": v(67.63, -179.27) * mm});
            skLineSegment(sketch, "E346", {"start": v(67.63, -179.27) * mm, "end": v(67.13, -179.41) * mm});
            skLineSegment(sketch, "E347", {"start": v(67.13, -179.41) * mm, "end": v(66.7, -179.56) * mm});
            skLineSegment(sketch, "E348", {"start": v(66.7, -179.56) * mm, "end": v(66.32, -179.7) * mm});
            skLineSegment(sketch, "E349", {"start": v(66.32, -179.7) * mm, "end": v(65.99, -179.86) * mm});
            skLineSegment(sketch, "E350", {"start": v(65.99, -179.86) * mm, "end": v(65.67, -180.04) * mm});
            skLineSegment(sketch, "E351", {"start": v(65.67, -180.04) * mm, "end": v(65.38, -180.23) * mm});
            skLineSegment(sketch, "E352", {"start": v(65.38, -180.23) * mm, "end": v(65.1, -180.44) * mm});
            skLineSegment(sketch, "E353", {"start": v(65.1, -180.44) * mm, "end": v(64.84, -180.67) * mm});
            skLineSegment(sketch, "E354", {"start": v(64.84, -180.67) * mm, "end": v(64.6, -180.92) * mm});
            skLineSegment(sketch, "E355", {"start": v(64.6, -180.92) * mm, "end": v(64.4, -181.18) * mm});
            skLineSegment(sketch, "E356", {"start": v(64.4, -181.18) * mm, "end": v(64.2, -181.46) * mm});
            skLineSegment(sketch, "E357", {"start": v(64.2, -181.46) * mm, "end": v(64.02, -181.75) * mm});
            skLineSegment(sketch, "E358", {"start": v(64.02, -181.75) * mm, "end": v(63.86, -182.05) * mm});
            skLineSegment(sketch, "E359", {"start": v(63.86, -182.05) * mm, "end": v(63.74, -182.36) * mm});
            skLineSegment(sketch, "E360", {"start": v(63.74, -182.36) * mm, "end": v(63.63, -182.68) * mm});
            skLineSegment(sketch, "E361", {"start": v(63.63, -182.68) * mm, "end": v(63.55, -183) * mm});
            skLineSegment(sketch, "E362", {"start": v(63.55, -183) * mm, "end": v(63.49, -183.33) * mm});
            skLineSegment(sketch, "E363", {"start": v(63.49, -183.33) * mm, "end": v(63.45, -183.67) * mm});
            skLineSegment(sketch, "E364", {"start": v(63.45, -183.67) * mm, "end": v(63.44, -184.02) * mm});
            skLineSegment(sketch, "E365", {"start": v(63.44, -184.02) * mm, "end": v(63.47, -184.55) * mm});
            skLineSegment(sketch, "E366", {"start": v(63.47, -184.55) * mm, "end": v(63.55, -185.06) * mm});
            skLineSegment(sketch, "E367", {"start": v(63.55, -185.06) * mm, "end": v(63.67, -185.54) * mm});
            skLineSegment(sketch, "E368", {"start": v(63.67, -185.54) * mm, "end": v(63.85, -186) * mm});
            skLineSegment(sketch, "E369", {"start": v(63.85, -186) * mm, "end": v(64.08, -186.44) * mm});
            skLineSegment(sketch, "E370", {"start": v(64.08, -186.44) * mm, "end": v(64.36, -186.86) * mm});
            skLineSegment(sketch, "E371", {"start": v(64.36, -186.86) * mm, "end": v(64.7, -187.25) * mm});
            skLineSegment(sketch, "E372", {"start": v(64.7, -187.25) * mm, "end": v(65.08, -187.62) * mm});
            skLineSegment(sketch, "E373", {"start": v(65.08, -187.62) * mm, "end": v(65.51, -187.96) * mm});
            skLineSegment(sketch, "E374", {"start": v(65.51, -187.96) * mm, "end": v(65.99, -188.25) * mm});
            skLineSegment(sketch, "E375", {"start": v(65.99, -188.25) * mm, "end": v(66.52, -188.5) * mm});
            skLineSegment(sketch, "E376", {"start": v(66.52, -188.5) * mm, "end": v(67.1, -188.7) * mm});
            skLineSegment(sketch, "E377", {"start": v(67.1, -188.7) * mm, "end": v(67.71, -188.86) * mm});
            skLineSegment(sketch, "E378", {"start": v(67.71, -188.86) * mm, "end": v(68.38, -188.97) * mm});
            skLineSegment(sketch, "E379", {"start": v(68.38, -188.97) * mm, "end": v(69.1, -189.04) * mm});
            skLineSegment(sketch, "E380", {"start": v(69.1, -189.04) * mm, "end": v(69.86, -189.06) * mm});
            skLineSegment(sketch, "E381", {"start": v(69.86, -189.06) * mm, "end": v(70.63, -189.04) * mm});
            skLineSegment(sketch, "E382", {"start": v(70.63, -189.04) * mm, "end": v(71.38, -188.98) * mm});
            skLineSegment(sketch, "E383", {"start": v(71.38, -188.98) * mm, "end": v(72.1, -188.87) * mm});
            skLineSegment(sketch, "E384", {"start": v(72.1, -188.87) * mm, "end": v(72.8, -188.72) * mm});
            skLineSegment(sketch, "E385", {"start": v(72.8, -188.72) * mm, "end": v(73.5, -188.53) * mm});
            skLineSegment(sketch, "E386", {"start": v(73.5, -188.53) * mm, "end": v(74.15, -188.3) * mm});
            skLineSegment(sketch, "E387", {"start": v(74.15, -188.3) * mm, "end": v(74.8, -188.02) * mm});
            skLineSegment(sketch, "E388", {"start": v(74.8, -188.02) * mm, "end": v(75.41, -187.7) * mm});
            skLineSegment(sketch, "E389", {"start": v(75.41, -187.7) * mm, "end": v(76, -187.34) * mm});
            skLineSegment(sketch, "E390", {"start": v(76, -187.34) * mm, "end": v(76.55, -186.95) * mm});
            skLineSegment(sketch, "E391", {"start": v(76.55, -186.95) * mm, "end": v(77.05, -186.53) * mm});
            skLineSegment(sketch, "E392", {"start": v(77.05, -186.53) * mm, "end": v(77.52, -186.08) * mm});
            skLineSegment(sketch, "E393", {"start": v(77.52, -186.08) * mm, "end": v(77.94, -185.6) * mm});
            skLineSegment(sketch, "E394", {"start": v(77.94, -185.6) * mm, "end": v(78.33, -185.09) * mm});
            skLineSegment(sketch, "E395", {"start": v(78.33, -185.09) * mm, "end": v(78.68, -184.54) * mm});
            skLineSegment(sketch, "E396", {"start": v(78.68, -184.54) * mm, "end": v(78.98, -183.96) * mm});
            skLineSegment(sketch, "E397", {"start": v(78.98, -183.96) * mm, "end": v(79.19, -183.48) * mm});
            skLineSegment(sketch, "E398", {"start": v(79.19, -183.48) * mm, "end": v(79.36, -182.94) * mm});
            skLineSegment(sketch, "E399", {"start": v(79.36, -182.94) * mm, "end": v(79.51, -182.35) * mm});
            skLineSegment(sketch, "E400", {"start": v(79.51, -182.35) * mm, "end": v(79.63, -181.7) * mm});
            skLineSegment(sketch, "E401", {"start": v(79.63, -181.7) * mm, "end": v(79.73, -181) * mm});
            skLineSegment(sketch, "E402", {"start": v(79.73, -181) * mm, "end": v(79.8, -180.24) * mm});
            skLineSegment(sketch, "E403", {"start": v(79.8, -180.24) * mm, "end": v(79.84, -179.43) * mm});
            skLineSegment(sketch, "E404", {"start": v(79.84, -179.43) * mm, "end": v(79.85, -178.56) * mm});
            skLineSegment(sketch, "E405", {"start": v(79.85, -178.56) * mm, "end": v(79.86, -172.09) * mm});
            skLineSegment(sketch, "E406", {"start": v(79.86, -172.09) * mm, "end": v(79.86, -171.85) * mm});
            skLineSegment(sketch, "E407", {"start": v(79.86, -171.85) * mm, "end": v(79.87, -171.64) * mm});
            skLineSegment(sketch, "E408", {"start": v(79.87, -171.64) * mm, "end": v(79.87, -171.45) * mm});
            skLineSegment(sketch, "E409", {"start": v(79.87, -171.45) * mm, "end": v(79.88, -171.28) * mm});
            skLineSegment(sketch, "E410", {"start": v(79.88, -171.28) * mm, "end": v(79.88, -171.15) * mm});
            skLineSegment(sketch, "E411", {"start": v(79.88, -171.15) * mm, "end": v(79.88, -171.03) * mm});
            skLineSegment(sketch, "E412", {"start": v(79.88, -171.03) * mm, "end": v(79.88, -170.94) * mm});
            skLineSegment(sketch, "E413", {"start": v(79.88, -170.94) * mm, "end": v(79.88, -170.54) * mm});
            skLineSegment(sketch, "E414", {"start": v(79.88, -170.54) * mm, "end": v(79.86, -170.15) * mm});
            skLineSegment(sketch, "E415", {"start": v(79.86, -170.15) * mm, "end": v(79.83, -169.78) * mm});
            skLineSegment(sketch, "E416", {"start": v(79.83, -169.78) * mm, "end": v(79.79, -169.42) * mm});
            skLineSegment(sketch, "E417", {"start": v(79.79, -169.42) * mm, "end": v(79.73, -169.07) * mm});
            skLineSegment(sketch, "E418", {"start": v(79.73, -169.07) * mm, "end": v(79.67, -168.74) * mm});
            skLineSegment(sketch, "E419", {"start": v(79.67, -168.74) * mm, "end": v(79.59, -168.43) * mm});
            skLineSegment(sketch, "E420", {"start": v(79.59, -168.43) * mm, "end": v(79.5, -168.13) * mm});
            skLineSegment(sketch, "E421", {"start": v(79.5, -168.13) * mm, "end": v(79.4, -167.85) * mm});
            skLineSegment(sketch, "E422", {"start": v(79.4, -167.85) * mm, "end": v(79.28, -167.58) * mm});
            skLineSegment(sketch, "E423", {"start": v(79.28, -167.58) * mm, "end": v(79.16, -167.33) * mm});
            skLineSegment(sketch, "E424", {"start": v(79.16, -167.33) * mm, "end": v(79.02, -167.1) * mm});
            skLineSegment(sketch, "E425", {"start": v(79.02, -167.1) * mm, "end": v(78.87, -166.87) * mm});
            skLineSegment(sketch, "E426", {"start": v(78.87, -166.87) * mm, "end": v(78.7, -166.66) * mm});
            skLineSegment(sketch, "E427", {"start": v(78.7, -166.66) * mm, "end": v(78.54, -166.47) * mm});
            skLineSegment(sketch, "E428", {"start": v(78.54, -166.47) * mm, "end": v(78.35, -166.3) * mm});
            skLineSegment(sketch, "E429", {"start": v(78.35, -166.3) * mm, "end": v(78.08, -166.07) * mm});
            skLineSegment(sketch, "E430", {"start": v(78.08, -166.07) * mm, "end": v(77.8, -165.87) * mm});
            skLineSegment(sketch, "E431", {"start": v(77.8, -165.87) * mm, "end": v(77.5, -165.67) * mm});
            skLineSegment(sketch, "E432", {"start": v(77.5, -165.67) * mm, "end": v(77.2, -165.5) * mm});
            skLineSegment(sketch, "E433", {"start": v(77.2, -165.5) * mm, "end": v(76.86, -165.33) * mm});
            skLineSegment(sketch, "E434", {"start": v(76.86, -165.33) * mm, "end": v(76.52, -165.18) * mm});
            skLineSegment(sketch, "E435", {"start": v(76.52, -165.18) * mm, "end": v(76.16, -165.04) * mm});
            skLineSegment(sketch, "E436", {"start": v(76.16, -165.04) * mm, "end": v(75.78, -164.92) * mm});
            skLineSegment(sketch, "E437", {"start": v(75.78, -164.92) * mm, "end": v(75.39, -164.82) * mm});
            skLineSegment(sketch, "E438", {"start": v(75.39, -164.82) * mm, "end": v(74.98, -164.72) * mm});
            skLineSegment(sketch, "E439", {"start": v(74.98, -164.72) * mm, "end": v(74.56, -164.64) * mm});
            skLineSegment(sketch, "E440", {"start": v(74.56, -164.64) * mm, "end": v(74.12, -164.58) * mm});
            skLineSegment(sketch, "E441", {"start": v(74.12, -164.58) * mm, "end": v(73.66, -164.53) * mm});
            skLineSegment(sketch, "E442", {"start": v(73.66, -164.53) * mm, "end": v(73.2, -164.5) * mm});
            skLineSegment(sketch, "E443", {"start": v(73.2, -164.5) * mm, "end": v(72.7, -164.47) * mm});
            skLineSegment(sketch, "E444", {"start": v(72.7, -164.47) * mm, "end": v(72.2, -164.47) * mm});
            skLineSegment(sketch, "E445", {"start": v(72.2, -164.47) * mm, "end": v(71.73, -164.47) * mm});
            skLineSegment(sketch, "E446", {"start": v(71.73, -164.47) * mm, "end": v(71.28, -164.49) * mm});
            skLineSegment(sketch, "E447", {"start": v(71.28, -164.49) * mm, "end": v(70.84, -164.51) * mm});
            skLineSegment(sketch, "E448", {"start": v(70.84, -164.51) * mm, "end": v(70.42, -164.55) * mm});
            skLineSegment(sketch, "E449", {"start": v(70.42, -164.55) * mm, "end": v(70.02, -164.6) * mm});
            skLineSegment(sketch, "E450", {"start": v(70.02, -164.6) * mm, "end": v(69.63, -164.65) * mm});
            skLineSegment(sketch, "E451", {"start": v(69.63, -164.65) * mm, "end": v(69.25, -164.72) * mm});
            skLineSegment(sketch, "E452", {"start": v(69.25, -164.72) * mm, "end": v(68.9, -164.8) * mm});
            skLineSegment(sketch, "E453", {"start": v(68.9, -164.8) * mm, "end": v(68.55, -164.89) * mm});
            skLineSegment(sketch, "E454", {"start": v(68.55, -164.89) * mm, "end": v(68.22, -164.99) * mm});
            skLineSegment(sketch, "E455", {"start": v(68.22, -164.99) * mm, "end": v(67.9, -165.1) * mm});
            skLineSegment(sketch, "E456", {"start": v(67.9, -165.1) * mm, "end": v(67.6, -165.22) * mm});
            skLineSegment(sketch, "E457", {"start": v(67.6, -165.22) * mm, "end": v(67.33, -165.35) * mm});
            skLineSegment(sketch, "E458", {"start": v(67.33, -165.35) * mm, "end": v(67.06, -165.49) * mm});
            skLineSegment(sketch, "E459", {"start": v(67.06, -165.49) * mm, "end": v(66.81, -165.64) * mm});
            skLineSegment(sketch, "E460", {"start": v(66.81, -165.64) * mm, "end": v(66.58, -165.8) * mm});
            skLineSegment(sketch, "E461", {"start": v(66.58, -165.8) * mm, "end": v(66.35, -165.97) * mm});
            skLineSegment(sketch, "E462", {"start": v(66.35, -165.97) * mm, "end": v(66.14, -166.17) * mm});
            skLineSegment(sketch, "E463", {"start": v(66.14, -166.17) * mm, "end": v(65.93, -166.37) * mm});
            skLineSegment(sketch, "E464", {"start": v(65.93, -166.37) * mm, "end": v(65.73, -166.6) * mm});
            skLineSegment(sketch, "E465", {"start": v(65.73, -166.6) * mm, "end": v(65.54, -166.83) * mm});
            skLineSegment(sketch, "E466", {"start": v(65.54, -166.83) * mm, "end": v(65.35, -167.1) * mm});
            skLineSegment(sketch, "E467", {"start": v(65.35, -167.1) * mm, "end": v(65.17, -167.36) * mm});
            skLineSegment(sketch, "E468", {"start": v(65.17, -167.36) * mm, "end": v(65, -167.65) * mm});
            skLineSegment(sketch, "E469", {"start": v(65, -167.65) * mm, "end": v(64.83, -167.95) * mm});
            skLineSegment(sketch, "E470", {"start": v(64.83, -167.95) * mm, "end": v(64.68, -168.27) * mm});
            skLineSegment(sketch, "E471", {"start": v(64.68, -168.27) * mm, "end": v(64.53, -168.6) * mm});
            skLineSegment(sketch, "E472", {"start": v(64.53, -168.6) * mm, "end": v(64.39, -168.96) * mm});
            skLineSegment(sketch, "E473", {"start": v(64.39, -168.96) * mm, "end": v(64.25, -169.33) * mm});
            skLineSegment(sketch, "E474", {"start": v(64.25, -169.33) * mm, "end": v(64.13, -169.7) * mm});
            skLineSegment(sketch, "E475", {"start": v(64.13, -169.7) * mm, "end": v(64, -170.1) * mm});
            skLineSegment(sketch, "E476", {"start": v(64, -170.1) * mm, "end": v(63.9, -170.52) * mm});
            skLineSegment(sketch, "E477", {"start": v(63.9, -170.52) * mm, "end": v(58.61, -169.8) * mm});
            skLineSegment(sketch, "E478", {"start": v(58.61, -169.8) * mm, "end": v(58.8, -168.98) * mm});
            skLineSegment(sketch, "E479", {"start": v(58.8, -168.98) * mm, "end": v(59.03, -168.2) * mm});
            skLineSegment(sketch, "E480", {"start": v(59.03, -168.2) * mm, "end": v(59.28, -167.45) * mm});
            skLineSegment(sketch, "E481", {"start": v(59.28, -167.45) * mm, "end": v(59.57, -166.74) * mm});
            skLineSegment(sketch, "E482", {"start": v(59.57, -166.74) * mm, "end": v(59.88, -166.08) * mm});
            skLineSegment(sketch, "E483", {"start": v(59.88, -166.08) * mm, "end": v(60.22, -165.45) * mm});
            skLineSegment(sketch, "E484", {"start": v(60.22, -165.45) * mm, "end": v(60.59, -164.87) * mm});
            skLineSegment(sketch, "E485", {"start": v(60.59, -164.87) * mm, "end": v(60.98, -164.33) * mm});
            skLineSegment(sketch, "E486", {"start": v(60.98, -164.33) * mm, "end": v(61.42, -163.82) * mm});
            skLineSegment(sketch, "E487", {"start": v(61.42, -163.82) * mm, "end": v(61.9, -163.35) * mm});
            skLineSegment(sketch, "E488", {"start": v(61.9, -163.35) * mm, "end": v(62.43, -162.9) * mm});
            skLineSegment(sketch, "E489", {"start": v(62.43, -162.9) * mm, "end": v(63, -162.49) * mm});
            skLineSegment(sketch, "E490", {"start": v(63, -162.49) * mm, "end": v(63.62, -162.1) * mm});
            skLineSegment(sketch, "E491", {"start": v(63.62, -162.1) * mm, "end": v(64.28, -161.74) * mm});
            skLineSegment(sketch, "E492", {"start": v(64.28, -161.74) * mm, "end": v(65, -161.42) * mm});
            skLineSegment(sketch, "E493", {"start": v(65, -161.42) * mm, "end": v(65.75, -161.12) * mm});
            skLineSegment(sketch, "E494", {"start": v(65.75, -161.12) * mm, "end": v(66.55, -160.86) * mm});
            skLineSegment(sketch, "E495", {"start": v(66.55, -160.86) * mm, "end": v(67.37, -160.63) * mm});
            skLineSegment(sketch, "E496", {"start": v(67.37, -160.63) * mm, "end": v(68.23, -160.44) * mm});
            skLineSegment(sketch, "E497", {"start": v(68.23, -160.44) * mm, "end": v(69.12, -160.28) * mm});
            skLineSegment(sketch, "E498", {"start": v(69.12, -160.28) * mm, "end": v(70.04, -160.15) * mm});
            skLineSegment(sketch, "E499", {"start": v(70.04, -160.15) * mm, "end": v(70.99, -160.07) * mm});
            skLineSegment(sketch, "E500", {"start": v(70.99, -160.07) * mm, "end": v(71.97, -160.01) * mm});
            skLineSegment(sketch, "E501", {"start": v(71.97, -160.01) * mm, "end": v(72.98, -160) * mm});
            skLineSegment(sketch, "E502", {"start": v(72.98, -160) * mm, "end": v(73.98, -160.01) * mm});
            skLineSegment(sketch, "E503", {"start": v(73.98, -160.01) * mm, "end": v(74.93, -160.06) * mm});
            skLineSegment(sketch, "E504", {"start": v(74.93, -160.06) * mm, "end": v(75.83, -160.13) * mm});
            skLineSegment(sketch, "E505", {"start": v(75.83, -160.13) * mm, "end": v(76.68, -160.24) * mm});
            skLineSegment(sketch, "E506", {"start": v(76.68, -160.24) * mm, "end": v(77.48, -160.37) * mm});
            skLineSegment(sketch, "E507", {"start": v(77.48, -160.37) * mm, "end": v(78.24, -160.54) * mm});
            skLineSegment(sketch, "E508", {"start": v(78.24, -160.54) * mm, "end": v(78.95, -160.73) * mm});
            skLineSegment(sketch, "E509", {"start": v(78.95, -160.73) * mm, "end": v(79.61, -160.96) * mm});
            skLineSegment(sketch, "E510", {"start": v(79.61, -160.96) * mm, "end": v(80.23, -161.2) * mm});
            skLineSegment(sketch, "E511", {"start": v(80.23, -161.2) * mm, "end": v(80.8, -161.47) * mm});
            skLineSegment(sketch, "E512", {"start": v(80.8, -161.47) * mm, "end": v(81.33, -161.75) * mm});
            skLineSegment(sketch, "E513", {"start": v(81.33, -161.75) * mm, "end": v(81.82, -162.04) * mm});
            skLineSegment(sketch, "E514", {"start": v(81.82, -162.04) * mm, "end": v(82.27, -162.35) * mm});
            skLineSegment(sketch, "E515", {"start": v(82.27, -162.35) * mm, "end": v(82.68, -162.67) * mm});
            skLineSegment(sketch, "E516", {"start": v(82.68, -162.67) * mm, "end": v(83.04, -163.01) * mm});
            skLineSegment(sketch, "E517", {"start": v(83.04, -163.01) * mm, "end": v(83.36, -163.37) * mm});
            skLineSegment(sketch, "E518", {"start": v(83.36, -163.37) * mm, "end": v(83.65, -163.75) * mm});
            skLineSegment(sketch, "E519", {"start": v(83.65, -163.75) * mm, "end": v(83.92, -164.15) * mm});
            skLineSegment(sketch, "E520", {"start": v(83.92, -164.15) * mm, "end": v(84.16, -164.57) * mm});
            skLineSegment(sketch, "E521", {"start": v(84.16, -164.57) * mm, "end": v(84.38, -165.02) * mm});
            skLineSegment(sketch, "E522", {"start": v(84.38, -165.02) * mm, "end": v(84.58, -165.49) * mm});
            skLineSegment(sketch, "E523", {"start": v(84.58, -165.49) * mm, "end": v(84.76, -165.98) * mm});
            skLineSegment(sketch, "E524", {"start": v(84.76, -165.98) * mm, "end": v(84.9, -166.5) * mm});
            skLineSegment(sketch, "E525", {"start": v(84.9, -166.5) * mm, "end": v(85.04, -167.04) * mm});
            skLineSegment(sketch, "E526", {"start": v(85.04, -167.04) * mm, "end": v(85.1, -167.42) * mm});
            skLineSegment(sketch, "E527", {"start": v(85.1, -167.42) * mm, "end": v(85.16, -167.87) * mm});
            skLineSegment(sketch, "E528", {"start": v(85.16, -167.87) * mm, "end": v(85.2, -168.4) * mm});
            skLineSegment(sketch, "E529", {"start": v(85.2, -168.4) * mm, "end": v(85.24, -168.98) * mm});
            skLineSegment(sketch, "E530", {"start": v(85.24, -168.98) * mm, "end": v(85.27, -169.64) * mm});
            skLineSegment(sketch, "E531", {"start": v(85.27, -169.64) * mm, "end": v(85.3, -170.36) * mm});
            skLineSegment(sketch, "E532", {"start": v(85.3, -170.36) * mm, "end": v(85.3, -171.16) * mm});
            skLineSegment(sketch, "E533", {"start": v(85.3, -171.16) * mm, "end": v(85.31, -172.02) * mm});
            skLineSegment(sketch, "E534", {"start": v(85.31, -172.02) * mm, "end": v(85.31, -179.22) * mm});
            skLineSegment(sketch, "E535", {"start": v(85.31, -179.22) * mm, "end": v(85.31, -180.14) * mm});
            skLineSegment(sketch, "E536", {"start": v(85.31, -180.14) * mm, "end": v(85.32, -181.02) * mm});
            skLineSegment(sketch, "E537", {"start": v(85.32, -181.02) * mm, "end": v(85.32, -181.85) * mm});
            skLineSegment(sketch, "E538", {"start": v(85.32, -181.85) * mm, "end": v(85.33, -182.64) * mm});
            skLineSegment(sketch, "E539", {"start": v(85.33, -182.64) * mm, "end": v(85.34, -183.39) * mm});
            skLineSegment(sketch, "E540", {"start": v(85.34, -183.39) * mm, "end": v(85.36, -184.1) * mm});
            skLineSegment(sketch, "E541", {"start": v(85.36, -184.1) * mm, "end": v(85.38, -184.75) * mm});
            skLineSegment(sketch, "E542", {"start": v(85.38, -184.75) * mm, "end": v(85.4, -185.37) * mm});
            skLineSegment(sketch, "E543", {"start": v(85.4, -185.37) * mm, "end": v(85.42, -185.94) * mm});
            skLineSegment(sketch, "E544", {"start": v(85.42, -185.94) * mm, "end": v(85.45, -186.47) * mm});
            skLineSegment(sketch, "E545", {"start": v(85.45, -186.47) * mm, "end": v(85.47, -186.96) * mm});
            skLineSegment(sketch, "E546", {"start": v(85.47, -186.96) * mm, "end": v(85.5, -187.4) * mm});
            skLineSegment(sketch, "E547", {"start": v(85.5, -187.4) * mm, "end": v(85.54, -187.8) * mm});
            skLineSegment(sketch, "E548", {"start": v(85.54, -187.8) * mm, "end": v(85.57, -188.16) * mm});
            skLineSegment(sketch, "E549", {"start": v(85.57, -188.16) * mm, "end": v(85.61, -188.48) * mm});
            skLineSegment(sketch, "E550", {"start": v(85.61, -188.48) * mm, "end": v(85.66, -188.75) * mm});
            skLineSegment(sketch, "E551", {"start": v(85.66, -188.75) * mm, "end": v(85.75, -189.24) * mm});
            skLineSegment(sketch, "E552", {"start": v(85.75, -189.24) * mm, "end": v(85.87, -189.73) * mm});
            skLineSegment(sketch, "E553", {"start": v(85.87, -189.73) * mm, "end": v(86, -190.22) * mm});
            skLineSegment(sketch, "E554", {"start": v(86, -190.22) * mm, "end": v(86.17, -190.7) * mm});
            skLineSegment(sketch, "E555", {"start": v(86.17, -190.7) * mm, "end": v(86.35, -191.18) * mm});
            skLineSegment(sketch, "E556", {"start": v(86.35, -191.18) * mm, "end": v(86.55, -191.65) * mm});
            skLineSegment(sketch, "E557", {"start": v(86.55, -191.65) * mm, "end": v(86.78, -192.11) * mm});
            skLineSegment(sketch, "E558", {"start": v(86.78, -192.11) * mm, "end": v(87.02, -192.57) * mm});
            skLineSegment(sketch, "E559", {"start": v(87.02, -192.57) * mm, "end": v(81.38, -192.57) * mm});
            skLineSegment(sketch, "E560", {"start": v(81.38, -192.57) * mm, "end": v(81.18, -192.14) * mm});
            skLineSegment(sketch, "E561", {"start": v(81.18, -192.14) * mm, "end": v(81, -191.7) * mm});
            skLineSegment(sketch, "E562", {"start": v(81, -191.7) * mm, "end": v(80.84, -191.23) * mm});
            skLineSegment(sketch, "E563", {"start": v(80.84, -191.23) * mm, "end": v(80.7, -190.75) * mm});
            skLineSegment(sketch, "E564", {"start": v(80.7, -190.75) * mm, "end": v(80.57, -190.25) * mm});
            skLineSegment(sketch, "E565", {"start": v(80.57, -190.25) * mm, "end": v(80.46, -189.73) * mm});
            skLineSegment(sketch, "E566", {"start": v(80.46, -189.73) * mm, "end": v(80.37, -189.2) * mm});
            skArc(sketch, "E567", {"start": v(-29.03, -173.58) * mm, "mid": v(-29.28, -175.8) * mm, "end": v(-29.24, -178.02) * mm});
            skLineSegment(sketch, "E568", {"start": v(-29.03, -173.58) * mm, "end": v(-14.22, -173.58) * mm});
            skLineSegment(sketch, "E569", {"start": v(-14.22, -173.58) * mm, "end": v(-14.27, -173.09) * mm});
            skLineSegment(sketch, "E570", {"start": v(-14.27, -173.09) * mm, "end": v(-14.33, -172.61) * mm});
            skLineSegment(sketch, "E571", {"start": v(-14.33, -172.61) * mm, "end": v(-14.4, -172.15) * mm});
            skLineSegment(sketch, "E572", {"start": v(-14.4, -172.15) * mm, "end": v(-14.48, -171.7) * mm});
            skLineSegment(sketch, "E573", {"start": v(-14.48, -171.7) * mm, "end": v(-14.57, -171.27) * mm});
            skLineSegment(sketch, "E574", {"start": v(-14.57, -171.27) * mm, "end": v(-14.67, -170.85) * mm});
            skLineSegment(sketch, "E575", {"start": v(-14.67, -170.85) * mm, "end": v(-14.79, -170.45) * mm});
            skLineSegment(sketch, "E576", {"start": v(-14.79, -170.45) * mm, "end": v(-14.9, -170.07) * mm});
            skLineSegment(sketch, "E577", {"start": v(-14.9, -170.07) * mm, "end": v(-15.04, -169.7) * mm});
            skLineSegment(sketch, "E578", {"start": v(-15.04, -169.7) * mm, "end": v(-15.18, -169.34) * mm});
            skLineSegment(sketch, "E579", {"start": v(-15.18, -169.34) * mm, "end": v(-15.34, -169) * mm});
            skLineSegment(sketch, "E580", {"start": v(-15.34, -169) * mm, "end": v(-15.5, -168.69) * mm});
            skLineSegment(sketch, "E581", {"start": v(-15.5, -168.69) * mm, "end": v(-15.67, -168.38) * mm});
            skLineSegment(sketch, "E582", {"start": v(-15.67, -168.38) * mm, "end": v(-15.86, -168.09) * mm});
            skLineSegment(sketch, "E583", {"start": v(-15.86, -168.09) * mm, "end": v(-16.05, -167.81) * mm});
            skLineSegment(sketch, "E584", {"start": v(-16.05, -167.81) * mm, "end": v(-16.26, -167.55) * mm});
            skLineSegment(sketch, "E585", {"start": v(-16.26, -167.55) * mm, "end": v(-16.59, -167.18) * mm});
            skLineSegment(sketch, "E586", {"start": v(-16.59, -167.18) * mm, "end": v(-16.93, -166.82) * mm});
            skLineSegment(sketch, "E587", {"start": v(-16.93, -166.82) * mm, "end": v(-17.28, -166.5) * mm});
            skLineSegment(sketch, "E588", {"start": v(-17.28, -166.5) * mm, "end": v(-17.64, -166.2) * mm});
            skLineSegment(sketch, "E589", {"start": v(-17.64, -166.2) * mm, "end": v(-18.02, -165.9) * mm});
            skLineSegment(sketch, "E590", {"start": v(-18.02, -165.9) * mm, "end": v(-18.4, -165.65) * mm});
            skLineSegment(sketch, "E591", {"start": v(-18.4, -165.65) * mm, "end": v(-18.8, -165.42) * mm});
            skLineSegment(sketch, "E592", {"start": v(-18.8, -165.42) * mm, "end": v(-19.22, -165.22) * mm});
            skLineSegment(sketch, "E593", {"start": v(-19.22, -165.22) * mm, "end": v(-19.64, -165.03) * mm});
            skLineSegment(sketch, "E594", {"start": v(-19.64, -165.03) * mm, "end": v(-20.08, -164.87) * mm});
            skLineSegment(sketch, "E595", {"start": v(-20.08, -164.87) * mm, "end": v(-20.53, -164.74) * mm});
            skLineSegment(sketch, "E596", {"start": v(-20.53, -164.74) * mm, "end": v(-20.99, -164.63) * mm});
            skLineSegment(sketch, "E597", {"start": v(-20.99, -164.63) * mm, "end": v(-21.46, -164.54) * mm});
            skLineSegment(sketch, "E598", {"start": v(-21.46, -164.54) * mm, "end": v(-21.94, -164.48) * mm});
            skLineSegment(sketch, "E599", {"start": v(-21.94, -164.48) * mm, "end": v(-22.44, -164.45) * mm});
            skLineSegment(sketch, "E600", {"start": v(-22.44, -164.45) * mm, "end": v(-22.95, -164.44) * mm});
            skLineSegment(sketch, "E601", {"start": v(-22.95, -164.44) * mm, "end": v(-23.4, -164.44) * mm});
            skLineSegment(sketch, "E602", {"start": v(-23.4, -164.44) * mm, "end": v(-23.86, -164.47) * mm});
            skLineSegment(sketch, "E603", {"start": v(-23.86, -164.47) * mm, "end": v(-24.3, -164.52) * mm});
            skLineSegment(sketch, "E604", {"start": v(-24.3, -164.52) * mm, "end": v(-24.73, -164.6) * mm});
            skLineSegment(sketch, "E605", {"start": v(-24.73, -164.6) * mm, "end": v(-25.16, -164.68) * mm});
            skLineSegment(sketch, "E606", {"start": v(-25.16, -164.68) * mm, "end": v(-25.57, -164.79) * mm});
            skLineSegment(sketch, "E607", {"start": v(-25.57, -164.79) * mm, "end": v(-25.98, -164.91) * mm});
            skLineSegment(sketch, "E608", {"start": v(-25.98, -164.91) * mm, "end": v(-26.37, -165.06) * mm});
            skLineSegment(sketch, "E609", {"start": v(-26.37, -165.06) * mm, "end": v(-26.76, -165.22) * mm});
            skLineSegment(sketch, "E610", {"start": v(-26.76, -165.22) * mm, "end": v(-27.13, -165.4) * mm});
            skLineSegment(sketch, "E611", {"start": v(-27.13, -165.4) * mm, "end": v(-27.5, -165.61) * mm});
            skLineSegment(sketch, "E612", {"start": v(-27.5, -165.61) * mm, "end": v(-27.86, -165.84) * mm});
            skLineSegment(sketch, "E613", {"start": v(-27.86, -165.84) * mm, "end": v(-28.2, -166.08) * mm});
            skLineSegment(sketch, "E614", {"start": v(-28.2, -166.08) * mm, "end": v(-28.55, -166.34) * mm});
            skLineSegment(sketch, "E615", {"start": v(-28.55, -166.34) * mm, "end": v(-28.88, -166.62) * mm});
            skLineSegment(sketch, "E616", {"start": v(-28.88, -166.62) * mm, "end": v(-29.2, -166.92) * mm});
            skLineSegment(sketch, "E617", {"start": v(-29.2, -166.92) * mm, "end": v(-29.5, -167.24) * mm});
            skLineSegment(sketch, "E618", {"start": v(-29.5, -167.24) * mm, "end": v(-29.8, -167.57) * mm});
            skLineSegment(sketch, "E619", {"start": v(-29.8, -167.57) * mm, "end": v(-30.07, -167.92) * mm});
            skLineSegment(sketch, "E620", {"start": v(-30.07, -167.92) * mm, "end": v(-30.33, -168.27) * mm});
            skLineSegment(sketch, "E621", {"start": v(-30.33, -168.27) * mm, "end": v(-30.56, -168.65) * mm});
            skLineSegment(sketch, "E622", {"start": v(-30.56, -168.65) * mm, "end": v(-30.78, -169.03) * mm});
            skLineSegment(sketch, "E623", {"start": v(-30.78, -169.03) * mm, "end": v(-30.99, -169.42) * mm});
            skLineSegment(sketch, "E624", {"start": v(-30.99, -169.42) * mm, "end": v(-31.17, -169.83) * mm});
            skArc(sketch, "E625", {"start": v(-31.17, -169.83) * mm, "mid": v(-32.36, -176.49) * mm, "end": v(-31.22, -183.15) * mm});
            skLineSegment(sketch, "E626", {"start": v(-31.22, -183.15) * mm, "end": v(-30.77, -184.08) * mm});
            skLineSegment(sketch, "E627", {"start": v(-30.77, -184.08) * mm, "end": v(-30.52, -184.51) * mm});
            skLineSegment(sketch, "E628", {"start": v(-30.52, -184.51) * mm, "end": v(-30.25, -184.93) * mm});
            skLineSegment(sketch, "E629", {"start": v(-30.25, -184.93) * mm, "end": v(-29.97, -185.33) * mm});
            skLineSegment(sketch, "E630", {"start": v(-29.97, -185.33) * mm, "end": v(-29.66, -185.7) * mm});
            skLineSegment(sketch, "E631", {"start": v(-29.66, -185.7) * mm, "end": v(-29.34, -186.06) * mm});
            skLineSegment(sketch, "E632", {"start": v(-29.34, -186.06) * mm, "end": v(-29, -186.4) * mm});
            skLineSegment(sketch, "E633", {"start": v(-29, -186.4) * mm, "end": v(-28.65, -186.72) * mm});
            skLineSegment(sketch, "E634", {"start": v(-28.65, -186.72) * mm, "end": v(-28.29, -187.01) * mm});
            skLineSegment(sketch, "E635", {"start": v(-28.29, -187.01) * mm, "end": v(-27.92, -187.28) * mm});
            skLineSegment(sketch, "E636", {"start": v(-27.92, -187.28) * mm, "end": v(-27.54, -187.53) * mm});
            skLineSegment(sketch, "E637", {"start": v(-27.54, -187.53) * mm, "end": v(-27.15, -187.76) * mm});
            skLineSegment(sketch, "E638", {"start": v(-27.15, -187.76) * mm, "end": v(-26.75, -187.97) * mm});
            skLineSegment(sketch, "E639", {"start": v(-26.75, -187.97) * mm, "end": v(-26.34, -188.16) * mm});
            skLineSegment(sketch, "E640", {"start": v(-26.34, -188.16) * mm, "end": v(-25.92, -188.32) * mm});
            skLineSegment(sketch, "E641", {"start": v(-25.92, -188.32) * mm, "end": v(-25.48, -188.46) * mm});
            skLineSegment(sketch, "E642", {"start": v(-25.48, -188.46) * mm, "end": v(-25.04, -188.58) * mm});
            skLineSegment(sketch, "E643", {"start": v(-25.04, -188.58) * mm, "end": v(-24.59, -188.68) * mm});
            skLineSegment(sketch, "E644", {"start": v(-24.59, -188.68) * mm, "end": v(-24.13, -188.75) * mm});
            skLineSegment(sketch, "E645", {"start": v(-24.13, -188.75) * mm, "end": v(-23.65, -188.8) * mm});
            skLineSegment(sketch, "E646", {"start": v(-23.65, -188.8) * mm, "end": v(-23.17, -188.84) * mm});
            skLineSegment(sketch, "E647", {"start": v(-23.17, -188.84) * mm, "end": v(-22.68, -188.85) * mm});
            skLineSegment(sketch, "E648", {"start": v(-22.68, -188.85) * mm, "end": v(-21.95, -188.83) * mm});
            skLineSegment(sketch, "E649", {"start": v(-21.95, -188.83) * mm, "end": v(-21.25, -188.75) * mm});
            skLineSegment(sketch, "E650", {"start": v(-21.25, -188.75) * mm, "end": v(-20.57, -188.63) * mm});
            skLineSegment(sketch, "E651", {"start": v(-20.57, -188.63) * mm, "end": v(-19.93, -188.46) * mm});
            skLineSegment(sketch, "E652", {"start": v(-19.93, -188.46) * mm, "end": v(-19.3, -188.24) * mm});
            skLineSegment(sketch, "E653", {"start": v(-19.3, -188.24) * mm, "end": v(-18.71, -187.98) * mm});
            skLineSegment(sketch, "E654", {"start": v(-18.71, -187.98) * mm, "end": v(-18.15, -187.66) * mm});
            skLineSegment(sketch, "E655", {"start": v(-18.15, -187.66) * mm, "end": v(-17.6, -187.3) * mm});
            skLineSegment(sketch, "E656", {"start": v(-17.6, -187.3) * mm, "end": v(-17.1, -186.87) * mm});
            skLineSegment(sketch, "E657", {"start": v(-17.1, -186.87) * mm, "end": v(-16.61, -186.4) * mm});
            skLineSegment(sketch, "E658", {"start": v(-16.61, -186.4) * mm, "end": v(-16.16, -185.86) * mm});
            skLineSegment(sketch, "E659", {"start": v(-16.16, -185.86) * mm, "end": v(-15.73, -185.27) * mm});
            skLineSegment(sketch, "E660", {"start": v(-15.73, -185.27) * mm, "end": v(-15.32, -184.62) * mm});
            skLineSegment(sketch, "E661", {"start": v(-15.32, -184.62) * mm, "end": v(-14.95, -183.9) * mm});
            skLineSegment(sketch, "E662", {"start": v(-14.95, -183.9) * mm, "end": v(-14.6, -183.14) * mm});
            skLineSegment(sketch, "E663", {"start": v(-14.6, -183.14) * mm, "end": v(-14.28, -182.31) * mm});
            skLineSegment(sketch, "E664", {"start": v(-14.28, -182.31) * mm, "end": v(-8.7, -183) * mm});
            skLineSegment(sketch, "E665", {"start": v(-8.7, -183) * mm, "end": v(-8.87, -183.6) * mm});
            skLineSegment(sketch, "E666", {"start": v(-8.87, -183.6) * mm, "end": v(-9.06, -184.2) * mm});
            skLineSegment(sketch, "E667", {"start": v(-9.06, -184.2) * mm, "end": v(-9.27, -184.76) * mm});
            skLineSegment(sketch, "E668", {"start": v(-9.27, -184.76) * mm, "end": v(-9.5, -185.31) * mm});
            skLineSegment(sketch, "E669", {"start": v(-9.5, -185.31) * mm, "end": v(-9.74, -185.85) * mm});
            skLineSegment(sketch, "E670", {"start": v(-9.74, -185.85) * mm, "end": v(-10, -186.36) * mm});
            skLineSegment(sketch, "E671", {"start": v(-10, -186.36) * mm, "end": v(-10.28, -186.86) * mm});
            skLineSegment(sketch, "E672", {"start": v(-10.28, -186.86) * mm, "end": v(-10.58, -187.35) * mm});
            skLineSegment(sketch, "E673", {"start": v(-10.58, -187.35) * mm, "end": v(-10.9, -187.81) * mm});
            skLineSegment(sketch, "E674", {"start": v(-10.9, -187.81) * mm, "end": v(-11.23, -188.26) * mm});
            skLineSegment(sketch, "E675", {"start": v(-11.23, -188.26) * mm, "end": v(-11.58, -188.7) * mm});
            skLineSegment(sketch, "E676", {"start": v(-11.58, -188.7) * mm, "end": v(-11.94, -189.1) * mm});
            skLineSegment(sketch, "E677", {"start": v(-11.94, -189.1) * mm, "end": v(-12.33, -189.5) * mm});
            skLineSegment(sketch, "E678", {"start": v(-12.33, -189.5) * mm, "end": v(-12.73, -189.88) * mm});
            skLineSegment(sketch, "E679", {"start": v(-12.73, -189.88) * mm, "end": v(-13.15, -190.25) * mm});
            skLineSegment(sketch, "E680", {"start": v(-13.15, -190.25) * mm, "end": v(-13.59, -190.6) * mm});
            skLineSegment(sketch, "E681", {"start": v(-13.59, -190.6) * mm, "end": v(-14.04, -190.92) * mm});
            skLineSegment(sketch, "E682", {"start": v(-14.04, -190.92) * mm, "end": v(-14.51, -191.23) * mm});
            skLineSegment(sketch, "E683", {"start": v(-14.51, -191.23) * mm, "end": v(-15, -191.5) * mm});
            skLineSegment(sketch, "E684", {"start": v(-15, -191.5) * mm, "end": v(-15.5, -191.77) * mm});
            skLineSegment(sketch, "E685", {"start": v(-15.5, -191.77) * mm, "end": v(-16.01, -192.02) * mm});
            skLineSegment(sketch, "E686", {"start": v(-16.01, -192.02) * mm, "end": v(-16.54, -192.24) * mm});
            skLineSegment(sketch, "E687", {"start": v(-16.54, -192.24) * mm, "end": v(-17.1, -192.44) * mm});
            skLineSegment(sketch, "E688", {"start": v(-17.1, -192.44) * mm, "end": v(-17.65, -192.62) * mm});
            skLineSegment(sketch, "E689", {"start": v(-17.65, -192.62) * mm, "end": v(-18.23, -192.78) * mm});
            skLineSegment(sketch, "E690", {"start": v(-18.23, -192.78) * mm, "end": v(-18.82, -192.91) * mm});
            skLineSegment(sketch, "E691", {"start": v(-18.82, -192.91) * mm, "end": v(-19.43, -193.03) * mm});
            skLineSegment(sketch, "E692", {"start": v(-19.43, -193.03) * mm, "end": v(-20.06, -193.12) * mm});
            skLineSegment(sketch, "E693", {"start": v(-20.06, -193.12) * mm, "end": v(-20.7, -193.2) * mm});
            skLineSegment(sketch, "E694", {"start": v(-20.7, -193.2) * mm, "end": v(-21.35, -193.25) * mm});
            skLineSegment(sketch, "E695", {"start": v(-21.35, -193.25) * mm, "end": v(-22.02, -193.28) * mm});
            skLineSegment(sketch, "E696", {"start": v(-22.02, -193.28) * mm, "end": v(-22.7, -193.3) * mm});
            skLineSegment(sketch, "E697", {"start": v(-22.7, -193.3) * mm, "end": v(-23.57, -193.28) * mm});
            skLineSegment(sketch, "E698", {"start": v(-23.57, -193.28) * mm, "end": v(-24.4, -193.22) * mm});
            skLineSegment(sketch, "E699", {"start": v(-24.4, -193.22) * mm, "end": v(-25.23, -193.14) * mm});
            skLineSegment(sketch, "E700", {"start": v(-25.23, -193.14) * mm, "end": v(-26.02, -193.02) * mm});
            skLineSegment(sketch, "E701", {"start": v(-26.02, -193.02) * mm, "end": v(-26.8, -192.87) * mm});
            skLineSegment(sketch, "E702", {"start": v(-26.8, -192.87) * mm, "end": v(-27.54, -192.69) * mm});
            skLineSegment(sketch, "E703", {"start": v(-27.54, -192.69) * mm, "end": v(-28.27, -192.47) * mm});
            skLineSegment(sketch, "E704", {"start": v(-28.27, -192.47) * mm, "end": v(-28.97, -192.22) * mm});
            skLineSegment(sketch, "E705", {"start": v(-28.97, -192.22) * mm, "end": v(-29.65, -191.93) * mm});
            skLineSegment(sketch, "E706", {"start": v(-29.65, -191.93) * mm, "end": v(-30.31, -191.61) * mm});
            skLineSegment(sketch, "E707", {"start": v(-30.31, -191.61) * mm, "end": v(-30.95, -191.26) * mm});
            skLineSegment(sketch, "E708", {"start": v(-30.95, -191.26) * mm, "end": v(-31.56, -190.87) * mm});
            skLineSegment(sketch, "E709", {"start": v(-31.56, -190.87) * mm, "end": v(-32.15, -190.45) * mm});
            skLineSegment(sketch, "E710", {"start": v(-32.15, -190.45) * mm, "end": v(-32.72, -190) * mm});
            skLineSegment(sketch, "E711", {"start": v(-32.72, -190) * mm, "end": v(-33.27, -189.5) * mm});
            skLineSegment(sketch, "E712", {"start": v(-33.27, -189.5) * mm, "end": v(-33.8, -188.99) * mm});
            skLineSegment(sketch, "E713", {"start": v(-33.8, -188.99) * mm, "end": v(-34.29, -188.44) * mm});
            skLineSegment(sketch, "E714", {"start": v(-34.29, -188.44) * mm, "end": v(-34.75, -187.86) * mm});
            skLineSegment(sketch, "E715", {"start": v(-34.75, -187.86) * mm, "end": v(-35.18, -187.25) * mm});
            skLineSegment(sketch, "E716", {"start": v(-35.18, -187.25) * mm, "end": v(-35.58, -186.62) * mm});
            skLineSegment(sketch, "E717", {"start": v(-35.58, -186.62) * mm, "end": v(-35.95, -185.96) * mm});
            skLineSegment(sketch, "E718", {"start": v(-35.95, -185.96) * mm, "end": v(-36.29, -185.27) * mm});
            skLineSegment(sketch, "E719", {"start": v(-36.29, -185.27) * mm, "end": v(-36.6, -184.56) * mm});
            skLineSegment(sketch, "E720", {"start": v(-36.6, -184.56) * mm, "end": v(-36.86, -183.82) * mm});
            skLineSegment(sketch, "E721", {"start": v(-36.86, -183.82) * mm, "end": v(-37.1, -183.05) * mm});
            skLineSegment(sketch, "E722", {"start": v(-37.1, -183.05) * mm, "end": v(-37.3, -182.25) * mm});
            skLineSegment(sketch, "E723", {"start": v(-37.3, -182.25) * mm, "end": v(-37.49, -181.43) * mm});
            skLineSegment(sketch, "E724", {"start": v(-37.49, -181.43) * mm, "end": v(-37.63, -180.58) * mm});
            skLineSegment(sketch, "E725", {"start": v(-37.63, -180.58) * mm, "end": v(-37.74, -179.7) * mm});
            skLineSegment(sketch, "E726", {"start": v(-37.74, -179.7) * mm, "end": v(-37.82, -178.8) * mm});
            skLineSegment(sketch, "E727", {"start": v(-37.82, -178.8) * mm, "end": v(-37.87, -177.87) * mm});
            skLineSegment(sketch, "E728", {"start": v(-37.87, -177.87) * mm, "end": v(-37.89, -176.91) * mm});
            skLineSegment(sketch, "E729", {"start": v(-37.89, -176.91) * mm, "end": v(-37.87, -175.92) * mm});
            skLineSegment(sketch, "E730", {"start": v(-37.87, -175.92) * mm, "end": v(-37.82, -174.96) * mm});
            skLineSegment(sketch, "E731", {"start": v(-37.82, -174.96) * mm, "end": v(-37.74, -174.03) * mm});
            skLineSegment(sketch, "E732", {"start": v(-37.74, -174.03) * mm, "end": v(-37.63, -173.12) * mm});
            skLineSegment(sketch, "E733", {"start": v(-37.63, -173.12) * mm, "end": v(-37.48, -172.24) * mm});
            skLineSegment(sketch, "E734", {"start": v(-37.48, -172.24) * mm, "end": v(-37.3, -171.4) * mm});
            skLineSegment(sketch, "E735", {"start": v(-37.3, -171.4) * mm, "end": v(-37.1, -170.57) * mm});
            skLineSegment(sketch, "E736", {"start": v(-37.1, -170.57) * mm, "end": v(-36.85, -169.77) * mm});
            skLineSegment(sketch, "E737", {"start": v(-36.85, -169.77) * mm, "end": v(-36.58, -169) * mm});
            skLineSegment(sketch, "E738", {"start": v(-36.58, -169) * mm, "end": v(-36.27, -168.27) * mm});
            skLineSegment(sketch, "E739", {"start": v(-36.27, -168.27) * mm, "end": v(-35.93, -167.56) * mm});
            skLineSegment(sketch, "E740", {"start": v(-35.93, -167.56) * mm, "end": v(-35.56, -166.88) * mm});
            skLineSegment(sketch, "E741", {"start": v(-35.56, -166.88) * mm, "end": v(-35.15, -166.23) * mm});
            skLineSegment(sketch, "E742", {"start": v(-35.15, -166.23) * mm, "end": v(-34.72, -165.6) * mm});
            skLineSegment(sketch, "E743", {"start": v(-34.72, -165.6) * mm, "end": v(-34.25, -165) * mm});
            skLineSegment(sketch, "E744", {"start": v(-34.25, -165) * mm, "end": v(-33.75, -164.44) * mm});
            skLineSegment(sketch, "E745", {"start": v(-33.75, -164.44) * mm, "end": v(-33.22, -163.9) * mm});
            skLineSegment(sketch, "E746", {"start": v(-33.22, -163.9) * mm, "end": v(-32.67, -163.4) * mm});
            skLineSegment(sketch, "E747", {"start": v(-32.67, -163.4) * mm, "end": v(-32.1, -162.93) * mm});
            skLineSegment(sketch, "E748", {"start": v(-32.1, -162.93) * mm, "end": v(-31.52, -162.5) * mm});
            skLineSegment(sketch, "E749", {"start": v(-31.52, -162.5) * mm, "end": v(-30.92, -162.1) * mm});
            skLineSegment(sketch, "E750", {"start": v(-30.92, -162.1) * mm, "end": v(-30.3, -161.73) * mm});
            skLineSegment(sketch, "E751", {"start": v(-30.3, -161.73) * mm, "end": v(-29.65, -161.4) * mm});
            skLineSegment(sketch, "E752", {"start": v(-29.65, -161.4) * mm, "end": v(-29, -161.1) * mm});
            skLineSegment(sketch, "E753", {"start": v(-29, -161.1) * mm, "end": v(-28.31, -160.85) * mm});
            skLineSegment(sketch, "E754", {"start": v(-28.31, -160.85) * mm, "end": v(-27.61, -160.62) * mm});
            skLineSegment(sketch, "E755", {"start": v(-27.61, -160.62) * mm, "end": v(-26.9, -160.43) * mm});
            skLineSegment(sketch, "E756", {"start": v(-26.9, -160.43) * mm, "end": v(-26.15, -160.27) * mm});
            skLineSegment(sketch, "E757", {"start": v(-26.15, -160.27) * mm, "end": v(-25.4, -160.15) * mm});
            skLineSegment(sketch, "E758", {"start": v(-25.4, -160.15) * mm, "end": v(-24.62, -160.07) * mm});
            skLineSegment(sketch, "E759", {"start": v(-24.62, -160.07) * mm, "end": v(-23.82, -160.01) * mm});
            skLineSegment(sketch, "E760", {"start": v(-23.82, -160.01) * mm, "end": v(-23, -160) * mm});
            skLineSegment(sketch, "E761", {"start": v(-23, -160) * mm, "end": v(-22.22, -160.01) * mm});
            skLineSegment(sketch, "E762", {"start": v(-22.22, -160.01) * mm, "end": v(-21.45, -160.06) * mm});
            skLineSegment(sketch, "E763", {"start": v(-21.45, -160.06) * mm, "end": v(-20.7, -160.15) * mm});
            skLineSegment(sketch, "E764", {"start": v(-20.7, -160.15) * mm, "end": v(-19.96, -160.27) * mm});
            skLineSegment(sketch, "E765", {"start": v(-19.96, -160.27) * mm, "end": v(-19.24, -160.42) * mm});
            skLineSegment(sketch, "E766", {"start": v(-19.24, -160.42) * mm, "end": v(-18.54, -160.6) * mm});
            skLineSegment(sketch, "E767", {"start": v(-18.54, -160.6) * mm, "end": v(-17.86, -160.83) * mm});
            skLineSegment(sketch, "E768", {"start": v(-17.86, -160.83) * mm, "end": v(-17.2, -161.08) * mm});
            skLineSegment(sketch, "E769", {"start": v(-17.2, -161.08) * mm, "end": v(-16.56, -161.37) * mm});
            skLineSegment(sketch, "E770", {"start": v(-16.56, -161.37) * mm, "end": v(-15.93, -161.7) * mm});
            skLineSegment(sketch, "E771", {"start": v(-15.93, -161.7) * mm, "end": v(-15.33, -162.05) * mm});
            skLineSegment(sketch, "E772", {"start": v(-15.33, -162.05) * mm, "end": v(-14.74, -162.44) * mm});
            skLineSegment(sketch, "E773", {"start": v(-14.74, -162.44) * mm, "end": v(-14.17, -162.87) * mm});
            skLineSegment(sketch, "E774", {"start": v(-14.17, -162.87) * mm, "end": v(-13.62, -163.33) * mm});
            skLineSegment(sketch, "E775", {"start": v(-13.62, -163.33) * mm, "end": v(-13.08, -163.82) * mm});
            skLineSegment(sketch, "E776", {"start": v(-13.08, -163.82) * mm, "end": v(-12.57, -164.35) * mm});
            skLineSegment(sketch, "E777", {"start": v(-12.57, -164.35) * mm, "end": v(-12.08, -164.9) * mm});
            skLineSegment(sketch, "E778", {"start": v(-12.08, -164.9) * mm, "end": v(-11.62, -165.49) * mm});
            skLineSegment(sketch, "E779", {"start": v(-11.62, -165.49) * mm, "end": v(-11.2, -166.1) * mm});
            skLineSegment(sketch, "E780", {"start": v(-11.2, -166.1) * mm, "end": v(-10.8, -166.74) * mm});
            skLineSegment(sketch, "E781", {"start": v(-10.8, -166.74) * mm, "end": v(-10.43, -167.4) * mm});
            skLineSegment(sketch, "E782", {"start": v(-10.43, -167.4) * mm, "end": v(-10.1, -168.1) * mm});
            skLineSegment(sketch, "E783", {"start": v(-10.1, -168.1) * mm, "end": v(-9.8, -168.83) * mm});
            skLineSegment(sketch, "E784", {"start": v(-9.8, -168.83) * mm, "end": v(-9.53, -169.58) * mm});
            skLineSegment(sketch, "E785", {"start": v(-9.53, -169.58) * mm, "end": v(-9.3, -170.36) * mm});
            skLineSegment(sketch, "E786", {"start": v(-9.3, -170.36) * mm, "end": v(-9.09, -171.16) * mm});
            skLineSegment(sketch, "E787", {"start": v(-9.09, -171.16) * mm, "end": v(-8.91, -172) * mm});
            skLineSegment(sketch, "E788", {"start": v(-8.91, -172) * mm, "end": v(-8.77, -172.86) * mm});
            skLineSegment(sketch, "E789", {"start": v(-8.77, -172.86) * mm, "end": v(-8.66, -173.75) * mm});
            skLineSegment(sketch, "E790", {"start": v(-8.66, -173.75) * mm, "end": v(-8.58, -174.67) * mm});
            skLineSegment(sketch, "E791", {"start": v(-8.58, -174.67) * mm, "end": v(-8.53, -175.61) * mm});
            skLineSegment(sketch, "E792", {"start": v(-8.53, -175.61) * mm, "end": v(-8.52, -176.58) * mm});
            skLineSegment(sketch, "E793", {"start": v(-8.52, -176.58) * mm, "end": v(-8.52, -176.85) * mm});
            skLineSegment(sketch, "E794", {"start": v(-8.52, -176.85) * mm, "end": v(-8.53, -177.18) * mm});
            skLineSegment(sketch, "E795", {"start": v(-8.53, -177.18) * mm, "end": v(-8.54, -177.57) * mm});
            skLineSegment(sketch, "E796", {"start": v(-8.54, -177.57) * mm, "end": v(-8.55, -178.02) * mm});
            skLineSegment(sketch, "E797", {"start": v(-8.55, -178.02) * mm, "end": v(-29.24, -178.02) * mm});
            skLineSegment(sketch, "E798", {"start": v(-80.11, -189.2) * mm, "end": v(-80.18, -188.64) * mm});
            skLineSegment(sketch, "E799", {"start": v(-80.18, -188.64) * mm, "end": v(-80.93, -189.26) * mm});
            skLineSegment(sketch, "E800", {"start": v(-80.93, -189.26) * mm, "end": v(-81.67, -189.82) * mm});
            skLineSegment(sketch, "E801", {"start": v(-81.67, -189.82) * mm, "end": v(-82.4, -190.34) * mm});
            skLineSegment(sketch, "E802", {"start": v(-82.4, -190.34) * mm, "end": v(-83.12, -190.82) * mm});
            skLineSegment(sketch, "E803", {"start": v(-83.12, -190.82) * mm, "end": v(-83.84, -191.24) * mm});
            skLineSegment(sketch, "E804", {"start": v(-83.84, -191.24) * mm, "end": v(-84.55, -191.62) * mm});
            skLineSegment(sketch, "E805", {"start": v(-84.55, -191.62) * mm, "end": v(-85.26, -191.96) * mm});
            skLineSegment(sketch, "E806", {"start": v(-85.26, -191.96) * mm, "end": v(-85.96, -192.24) * mm});
            skLineSegment(sketch, "E807", {"start": v(-85.96, -192.24) * mm, "end": v(-86.66, -192.49) * mm});
            skLineSegment(sketch, "E808", {"start": v(-86.66, -192.49) * mm, "end": v(-87.37, -192.7) * mm});
            skLineSegment(sketch, "E809", {"start": v(-87.37, -192.7) * mm, "end": v(-88.1, -192.88) * mm});
            skLineSegment(sketch, "E810", {"start": v(-88.1, -192.88) * mm, "end": v(-88.83, -193.03) * mm});
            skLineSegment(sketch, "E811", {"start": v(-88.83, -193.03) * mm, "end": v(-89.58, -193.14) * mm});
            skLineSegment(sketch, "E812", {"start": v(-89.58, -193.14) * mm, "end": v(-90.35, -193.23) * mm});
            skLineSegment(sketch, "E813", {"start": v(-90.35, -193.23) * mm, "end": v(-91.12, -193.28) * mm});
            skLineSegment(sketch, "E814", {"start": v(-91.12, -193.28) * mm, "end": v(-91.9, -193.3) * mm});
            skLineSegment(sketch, "E815", {"start": v(-91.9, -193.3) * mm, "end": v(-92.56, -193.28) * mm});
            skLineSegment(sketch, "E816", {"start": v(-92.56, -193.28) * mm, "end": v(-93.18, -193.25) * mm});
            skLineSegment(sketch, "E817", {"start": v(-93.18, -193.25) * mm, "end": v(-93.8, -193.2) * mm});
            skLineSegment(sketch, "E818", {"start": v(-93.8, -193.2) * mm, "end": v(-94.38, -193.13) * mm});
            skLineSegment(sketch, "E819", {"start": v(-94.38, -193.13) * mm, "end": v(-94.95, -193.04) * mm});
            skLineSegment(sketch, "E820", {"start": v(-94.95, -193.04) * mm, "end": v(-95.5, -192.93) * mm});
            skLineSegment(sketch, "E821", {"start": v(-95.5, -192.93) * mm, "end": v(-96.04, -192.8) * mm});
            skLineSegment(sketch, "E822", {"start": v(-96.04, -192.8) * mm, "end": v(-96.55, -192.65) * mm});
            skLineSegment(sketch, "E823", {"start": v(-96.55, -192.65) * mm, "end": v(-97.05, -192.48) * mm});
            skLineSegment(sketch, "E824", {"start": v(-97.05, -192.48) * mm, "end": v(-97.52, -192.3) * mm});
            skLineSegment(sketch, "E825", {"start": v(-97.52, -192.3) * mm, "end": v(-97.98, -192.08) * mm});
            skLineSegment(sketch, "E826", {"start": v(-97.98, -192.08) * mm, "end": v(-98.42, -191.85) * mm});
            skLineSegment(sketch, "E827", {"start": v(-98.42, -191.85) * mm, "end": v(-98.84, -191.6) * mm});
            skLineSegment(sketch, "E828", {"start": v(-98.84, -191.6) * mm, "end": v(-99.24, -191.33) * mm});
            skLineSegment(sketch, "E829", {"start": v(-99.24, -191.33) * mm, "end": v(-99.62, -191.04) * mm});
            skLineSegment(sketch, "E830", {"start": v(-99.62, -191.04) * mm, "end": v(-99.98, -190.73) * mm});
            skLineSegment(sketch, "E831", {"start": v(-99.98, -190.73) * mm, "end": v(-100.32, -190.4) * mm});
            skLineSegment(sketch, "E832", {"start": v(-100.32, -190.4) * mm, "end": v(-100.64, -190.06) * mm});
            skLineSegment(sketch, "E833", {"start": v(-100.64, -190.06) * mm, "end": v(-100.94, -189.72) * mm});
            skLineSegment(sketch, "E834", {"start": v(-100.94, -189.72) * mm, "end": v(-101.21, -189.36) * mm});
            skLineSegment(sketch, "E835", {"start": v(-101.21, -189.36) * mm, "end": v(-101.47, -188.99) * mm});
            skLineSegment(sketch, "E836", {"start": v(-101.47, -188.99) * mm, "end": v(-101.7, -188.6) * mm});
            skLineSegment(sketch, "E837", {"start": v(-101.7, -188.6) * mm, "end": v(-101.9, -188.21) * mm});
            skLineSegment(sketch, "E838", {"start": v(-101.9, -188.21) * mm, "end": v(-102.1, -187.8) * mm});
            skLineSegment(sketch, "E839", {"start": v(-102.1, -187.8) * mm, "end": v(-102.26, -187.4) * mm});
            skLineSegment(sketch, "E840", {"start": v(-102.26, -187.4) * mm, "end": v(-102.4, -186.96) * mm});
            skLineSegment(sketch, "E841", {"start": v(-102.4, -186.96) * mm, "end": v(-102.52, -186.53) * mm});
            skLineSegment(sketch, "E842", {"start": v(-102.52, -186.53) * mm, "end": v(-102.62, -186.08) * mm});
            skLineSegment(sketch, "E843", {"start": v(-102.62, -186.08) * mm, "end": v(-102.7, -185.62) * mm});
            skLineSegment(sketch, "E844", {"start": v(-102.7, -185.62) * mm, "end": v(-102.75, -185.15) * mm});
            skLineSegment(sketch, "E845", {"start": v(-102.75, -185.15) * mm, "end": v(-102.79, -184.67) * mm});
            skLineSegment(sketch, "E846", {"start": v(-102.79, -184.67) * mm, "end": v(-102.8, -184.17) * mm});
            skLineSegment(sketch, "E847", {"start": v(-102.8, -184.17) * mm, "end": v(-102.78, -183.6) * mm});
            skLineSegment(sketch, "E848", {"start": v(-102.78, -183.6) * mm, "end": v(-102.73, -183.03) * mm});
            skLineSegment(sketch, "E849", {"start": v(-102.73, -183.03) * mm, "end": v(-102.65, -182.48) * mm});
            skLineSegment(sketch, "E850", {"start": v(-102.65, -182.48) * mm, "end": v(-102.53, -181.93) * mm});
            skLineSegment(sketch, "E851", {"start": v(-102.53, -181.93) * mm, "end": v(-102.38, -181.4) * mm});
            skLineSegment(sketch, "E852", {"start": v(-102.38, -181.4) * mm, "end": v(-102.2, -180.9) * mm});
            skLineSegment(sketch, "E853", {"start": v(-102.2, -180.9) * mm, "end": v(-101.98, -180.39) * mm});
            skLineSegment(sketch, "E854", {"start": v(-101.98, -180.39) * mm, "end": v(-101.73, -179.9) * mm});
            skLineSegment(sketch, "E855", {"start": v(-101.73, -179.9) * mm, "end": v(-101.46, -179.43) * mm});
            skLineSegment(sketch, "E856", {"start": v(-101.46, -179.43) * mm, "end": v(-101.16, -178.98) * mm});
            skLineSegment(sketch, "E857", {"start": v(-101.16, -178.98) * mm, "end": v(-100.84, -178.55) * mm});
            skLineSegment(sketch, "E858", {"start": v(-100.84, -178.55) * mm, "end": v(-100.5, -178.15) * mm});
            skLineSegment(sketch, "E859", {"start": v(-100.5, -178.15) * mm, "end": v(-100.14, -177.78) * mm});
            skLineSegment(sketch, "E860", {"start": v(-100.14, -177.78) * mm, "end": v(-99.77, -177.43) * mm});
            skLineSegment(sketch, "E861", {"start": v(-99.77, -177.43) * mm, "end": v(-99.36, -177.1) * mm});
            skLineSegment(sketch, "E862", {"start": v(-99.36, -177.1) * mm, "end": v(-98.94, -176.8) * mm});
            skLineSegment(sketch, "E863", {"start": v(-98.94, -176.8) * mm, "end": v(-98.5, -176.51) * mm});
            skLineSegment(sketch, "E864", {"start": v(-98.5, -176.51) * mm, "end": v(-98.05, -176.24) * mm});
            skLineSegment(sketch, "E865", {"start": v(-98.05, -176.24) * mm, "end": v(-97.59, -176) * mm});
            skLineSegment(sketch, "E866", {"start": v(-97.59, -176) * mm, "end": v(-97.11, -175.77) * mm});
            skLineSegment(sketch, "E867", {"start": v(-97.11, -175.77) * mm, "end": v(-96.62, -175.55) * mm});
            skLineSegment(sketch, "E868", {"start": v(-96.62, -175.55) * mm, "end": v(-96.11, -175.36) * mm});
            skLineSegment(sketch, "E869", {"start": v(-96.11, -175.36) * mm, "end": v(-95.6, -175.18) * mm});
            skLineSegment(sketch, "E870", {"start": v(-95.6, -175.18) * mm, "end": v(-95.06, -175.02) * mm});
            skLineSegment(sketch, "E871", {"start": v(-95.06, -175.02) * mm, "end": v(-94.64, -174.92) * mm});
            skLineSegment(sketch, "E872", {"start": v(-94.64, -174.92) * mm, "end": v(-94.16, -174.82) * mm});
            skLineSegment(sketch, "E873", {"start": v(-94.16, -174.82) * mm, "end": v(-93.64, -174.71) * mm});
            skLineSegment(sketch, "E874", {"start": v(-93.64, -174.71) * mm, "end": v(-93.06, -174.61) * mm});
            skLineSegment(sketch, "E875", {"start": v(-93.06, -174.61) * mm, "end": v(-92.44, -174.51) * mm});
            skLineSegment(sketch, "E876", {"start": v(-92.44, -174.51) * mm, "end": v(-91.76, -174.41) * mm});
            skLineSegment(sketch, "E877", {"start": v(-91.76, -174.41) * mm, "end": v(-91.04, -174.31) * mm});
            skLineSegment(sketch, "E878", {"start": v(-91.04, -174.31) * mm, "end": v(-90.26, -174.21) * mm});
            skLineSegment(sketch, "E879", {"start": v(-90.26, -174.21) * mm, "end": v(-89.46, -174.12) * mm});
            skLineSegment(sketch, "E880", {"start": v(-89.46, -174.12) * mm, "end": v(-88.68, -174.01) * mm});
            skLineSegment(sketch, "E881", {"start": v(-88.68, -174.01) * mm, "end": v(-87.93, -173.91) * mm});
            skLineSegment(sketch, "E882", {"start": v(-87.93, -173.91) * mm, "end": v(-87.2, -173.8) * mm});
            skLineSegment(sketch, "E883", {"start": v(-87.2, -173.8) * mm, "end": v(-86.5, -173.7) * mm});
            skLineSegment(sketch, "E884", {"start": v(-86.5, -173.7) * mm, "end": v(-85.84, -173.59) * mm});
            skLineSegment(sketch, "E885", {"start": v(-85.84, -173.59) * mm, "end": v(-85.2, -173.47) * mm});
            skLineSegment(sketch, "E886", {"start": v(-85.2, -173.47) * mm, "end": v(-84.58, -173.36) * mm});
            skLineSegment(sketch, "E887", {"start": v(-84.58, -173.36) * mm, "end": v(-84, -173.24) * mm});
            skLineSegment(sketch, "E888", {"start": v(-84, -173.24) * mm, "end": v(-83.69, -173.18) * mm});
            skLineSegment(sketch, "E889", {"start": v(-83.69, -177.55) * mm, "end": v(-83.69, -173.18) * mm});
            skLineSegment(sketch, "E890", {"start": v(-83.69, -177.55) * mm, "end": v(-83.77, -177.56) * mm});
            skLineSegment(sketch, "E891", {"start": v(-83.77, -177.56) * mm, "end": v(-84.3, -177.7) * mm});
            skLineSegment(sketch, "E892", {"start": v(-84.3, -177.7) * mm, "end": v(-84.87, -177.82) * mm});
            skLineSegment(sketch, "E893", {"start": v(-84.87, -177.82) * mm, "end": v(-85.45, -177.94) * mm});
            skLineSegment(sketch, "E894", {"start": v(-85.45, -177.94) * mm, "end": v(-86.06, -178.06) * mm});
            skLineSegment(sketch, "E895", {"start": v(-86.06, -178.06) * mm, "end": v(-86.7, -178.18) * mm});
            skLineSegment(sketch, "E896", {"start": v(-86.7, -178.18) * mm, "end": v(-87.35, -178.3) * mm});
            skLineSegment(sketch, "E897", {"start": v(-87.35, -178.3) * mm, "end": v(-88.03, -178.4) * mm});
            skLineSegment(sketch, "E898", {"start": v(-88.03, -178.4) * mm, "end": v(-88.73, -178.52) * mm});
            skLineSegment(sketch, "E899", {"start": v(-88.73, -178.52) * mm, "end": v(-89.45, -178.62) * mm});
            skLineSegment(sketch, "E900", {"start": v(-89.45, -178.62) * mm, "end": v(-90.25, -178.75) * mm});
            skLineSegment(sketch, "E901", {"start": v(-90.25, -178.75) * mm, "end": v(-91, -178.87) * mm});
            skLineSegment(sketch, "E902", {"start": v(-91, -178.87) * mm, "end": v(-91.67, -179) * mm});
            skLineSegment(sketch, "E903", {"start": v(-91.67, -179) * mm, "end": v(-92.3, -179.13) * mm});
            skLineSegment(sketch, "E904", {"start": v(-92.3, -179.13) * mm, "end": v(-92.85, -179.27) * mm});
            skLineSegment(sketch, "E905", {"start": v(-92.85, -179.27) * mm, "end": v(-93.35, -179.41) * mm});
            skLineSegment(sketch, "E906", {"start": v(-93.35, -179.41) * mm, "end": v(-93.78, -179.56) * mm});
            skLineSegment(sketch, "E907", {"start": v(-93.78, -179.56) * mm, "end": v(-94.16, -179.7) * mm});
            skLineSegment(sketch, "E908", {"start": v(-94.16, -179.7) * mm, "end": v(-94.5, -179.86) * mm});
            skLineSegment(sketch, "E909", {"start": v(-94.5, -179.86) * mm, "end": v(-94.8, -180.04) * mm});
            skLineSegment(sketch, "E910", {"start": v(-94.8, -180.04) * mm, "end": v(-95.1, -180.23) * mm});
            skLineSegment(sketch, "E911", {"start": v(-95.1, -180.23) * mm, "end": v(-95.38, -180.44) * mm});
            skLineSegment(sketch, "E912", {"start": v(-95.38, -180.44) * mm, "end": v(-95.64, -180.67) * mm});
            skLineSegment(sketch, "E913", {"start": v(-95.64, -180.67) * mm, "end": v(-95.87, -180.92) * mm});
            skLineSegment(sketch, "E914", {"start": v(-95.87, -180.92) * mm, "end": v(-96.1, -181.18) * mm});
            skLineSegment(sketch, "E915", {"start": v(-96.1, -181.18) * mm, "end": v(-96.29, -181.46) * mm});
            skLineSegment(sketch, "E916", {"start": v(-96.29, -181.46) * mm, "end": v(-96.46, -181.75) * mm});
            skLineSegment(sketch, "E917", {"start": v(-96.46, -181.75) * mm, "end": v(-96.62, -182.05) * mm});
            skLineSegment(sketch, "E918", {"start": v(-96.62, -182.05) * mm, "end": v(-96.75, -182.36) * mm});
            skLineSegment(sketch, "E919", {"start": v(-96.75, -182.36) * mm, "end": v(-96.85, -182.68) * mm});
            skLineSegment(sketch, "E920", {"start": v(-96.85, -182.68) * mm, "end": v(-96.93, -183) * mm});
            skLineSegment(sketch, "E921", {"start": v(-96.93, -183) * mm, "end": v(-97, -183.33) * mm});
            skLineSegment(sketch, "E922", {"start": v(-97, -183.33) * mm, "end": v(-97.03, -183.67) * mm});
            skLineSegment(sketch, "E923", {"start": v(-97.03, -183.67) * mm, "end": v(-97.04, -184.02) * mm});
            skLineSegment(sketch, "E924", {"start": v(-97.04, -184.02) * mm, "end": v(-97.01, -184.55) * mm});
            skLineSegment(sketch, "E925", {"start": v(-97.01, -184.55) * mm, "end": v(-96.94, -185.06) * mm});
            skLineSegment(sketch, "E926", {"start": v(-96.94, -185.06) * mm, "end": v(-96.8, -185.54) * mm});
            skLineSegment(sketch, "E927", {"start": v(-96.8, -185.54) * mm, "end": v(-96.63, -186) * mm});
            skLineSegment(sketch, "E928", {"start": v(-96.63, -186) * mm, "end": v(-96.4, -186.44) * mm});
            skLineSegment(sketch, "E929", {"start": v(-96.4, -186.44) * mm, "end": v(-96.12, -186.86) * mm});
            skLineSegment(sketch, "E930", {"start": v(-96.12, -186.86) * mm, "end": v(-95.79, -187.25) * mm});
            skLineSegment(sketch, "E931", {"start": v(-95.79, -187.25) * mm, "end": v(-95.4, -187.62) * mm});
            skLineSegment(sketch, "E932", {"start": v(-95.4, -187.62) * mm, "end": v(-94.97, -187.96) * mm});
            skLineSegment(sketch, "E933", {"start": v(-94.97, -187.96) * mm, "end": v(-94.5, -188.25) * mm});
            skLineSegment(sketch, "E934", {"start": v(-94.5, -188.25) * mm, "end": v(-93.97, -188.5) * mm});
            skLineSegment(sketch, "E935", {"start": v(-93.97, -188.5) * mm, "end": v(-93.4, -188.7) * mm});
            skLineSegment(sketch, "E936", {"start": v(-93.4, -188.7) * mm, "end": v(-92.77, -188.86) * mm});
            skLineSegment(sketch, "E937", {"start": v(-92.77, -188.86) * mm, "end": v(-92.1, -188.97) * mm});
            skLineSegment(sketch, "E938", {"start": v(-92.1, -188.97) * mm, "end": v(-91.38, -189.04) * mm});
            skLineSegment(sketch, "E939", {"start": v(-91.38, -189.04) * mm, "end": v(-90.62, -189.06) * mm});
            skLineSegment(sketch, "E940", {"start": v(-90.62, -189.06) * mm, "end": v(-89.85, -189.04) * mm});
            skLineSegment(sketch, "E941", {"start": v(-89.85, -189.04) * mm, "end": v(-89.1, -188.98) * mm});
            skLineSegment(sketch, "E942", {"start": v(-89.1, -188.98) * mm, "end": v(-88.38, -188.87) * mm});
            skLineSegment(sketch, "E943", {"start": v(-88.38, -188.87) * mm, "end": v(-87.67, -188.72) * mm});
            skLineSegment(sketch, "E944", {"start": v(-87.67, -188.72) * mm, "end": v(-86.99, -188.53) * mm});
            skLineSegment(sketch, "E945", {"start": v(-86.99, -188.53) * mm, "end": v(-86.33, -188.3) * mm});
            skLineSegment(sketch, "E946", {"start": v(-86.33, -188.3) * mm, "end": v(-85.69, -188.02) * mm});
            skLineSegment(sketch, "E947", {"start": v(-85.69, -188.02) * mm, "end": v(-85.07, -187.7) * mm});
            skLineSegment(sketch, "E948", {"start": v(-85.07, -187.7) * mm, "end": v(-84.48, -187.34) * mm});
            skLineSegment(sketch, "E949", {"start": v(-84.48, -187.34) * mm, "end": v(-83.94, -186.95) * mm});
            skLineSegment(sketch, "E950", {"start": v(-83.94, -186.95) * mm, "end": v(-83.43, -186.53) * mm});
            skLineSegment(sketch, "E951", {"start": v(-83.43, -186.53) * mm, "end": v(-82.96, -186.08) * mm});
            skLineSegment(sketch, "E952", {"start": v(-82.96, -186.08) * mm, "end": v(-82.54, -185.6) * mm});
            skLineSegment(sketch, "E953", {"start": v(-82.54, -185.6) * mm, "end": v(-82.15, -185.09) * mm});
            skLineSegment(sketch, "E954", {"start": v(-82.15, -185.09) * mm, "end": v(-81.8, -184.54) * mm});
            skLineSegment(sketch, "E955", {"start": v(-81.8, -184.54) * mm, "end": v(-81.5, -183.96) * mm});
            skLineSegment(sketch, "E956", {"start": v(-81.5, -183.96) * mm, "end": v(-81.3, -183.48) * mm});
            skLineSegment(sketch, "E957", {"start": v(-81.3, -183.48) * mm, "end": v(-81.12, -182.94) * mm});
            skLineSegment(sketch, "E958", {"start": v(-81.12, -182.94) * mm, "end": v(-80.97, -182.35) * mm});
            skLineSegment(sketch, "E959", {"start": v(-80.97, -182.35) * mm, "end": v(-80.85, -181.7) * mm});
            skLineSegment(sketch, "E960", {"start": v(-80.85, -181.7) * mm, "end": v(-80.75, -181) * mm});
            skLineSegment(sketch, "E961", {"start": v(-80.75, -181) * mm, "end": v(-80.69, -180.24) * mm});
            skLineSegment(sketch, "E962", {"start": v(-80.69, -180.24) * mm, "end": v(-80.64, -179.43) * mm});
            skLineSegment(sketch, "E963", {"start": v(-80.64, -179.43) * mm, "end": v(-80.63, -178.56) * mm});
            skLineSegment(sketch, "E964", {"start": v(-80.63, -178.56) * mm, "end": v(-80.62, -172.09) * mm});
            skLineSegment(sketch, "E965", {"start": v(-80.62, -172.09) * mm, "end": v(-80.62, -171.85) * mm});
            skLineSegment(sketch, "E966", {"start": v(-80.62, -171.85) * mm, "end": v(-80.61, -171.64) * mm});
            skLineSegment(sketch, "E967", {"start": v(-80.61, -171.64) * mm, "end": v(-80.6, -171.45) * mm});
            skLineSegment(sketch, "E968", {"start": v(-80.6, -171.45) * mm, "end": v(-80.6, -171.28) * mm});
            skLineSegment(sketch, "E969", {"start": v(-80.6, -171.28) * mm, "end": v(-80.6, -171.15) * mm});
            skLineSegment(sketch, "E970", {"start": v(-80.6, -171.15) * mm, "end": v(-80.6, -171.03) * mm});
            skLineSegment(sketch, "E971", {"start": v(-80.6, -171.03) * mm, "end": v(-80.6, -170.94) * mm});
            skLineSegment(sketch, "E972", {"start": v(-80.6, -170.94) * mm, "end": v(-80.6, -170.54) * mm});
            skLineSegment(sketch, "E973", {"start": v(-80.6, -170.54) * mm, "end": v(-80.62, -170.15) * mm});
            skLineSegment(sketch, "E974", {"start": v(-80.62, -170.15) * mm, "end": v(-80.65, -169.78) * mm});
            skLineSegment(sketch, "E975", {"start": v(-80.65, -169.78) * mm, "end": v(-80.7, -169.42) * mm});
            skLineSegment(sketch, "E976", {"start": v(-80.7, -169.42) * mm, "end": v(-80.75, -169.07) * mm});
            skLineSegment(sketch, "E977", {"start": v(-80.75, -169.07) * mm, "end": v(-80.82, -168.74) * mm});
            skLineSegment(sketch, "E978", {"start": v(-80.82, -168.74) * mm, "end": v(-80.9, -168.43) * mm});
            skLineSegment(sketch, "E979", {"start": v(-80.9, -168.43) * mm, "end": v(-80.98, -168.13) * mm});
            skLineSegment(sketch, "E980", {"start": v(-80.98, -168.13) * mm, "end": v(-81.08, -167.85) * mm});
            skLineSegment(sketch, "E981", {"start": v(-81.08, -167.85) * mm, "end": v(-81.2, -167.58) * mm});
            skLineSegment(sketch, "E982", {"start": v(-81.2, -167.58) * mm, "end": v(-81.32, -167.33) * mm});
            skLineSegment(sketch, "E983", {"start": v(-81.32, -167.33) * mm, "end": v(-81.46, -167.1) * mm});
            skLineSegment(sketch, "E984", {"start": v(-81.46, -167.1) * mm, "end": v(-81.61, -166.87) * mm});
            skLineSegment(sketch, "E985", {"start": v(-81.61, -166.87) * mm, "end": v(-81.77, -166.66) * mm});
            skLineSegment(sketch, "E986", {"start": v(-81.77, -166.66) * mm, "end": v(-81.95, -166.47) * mm});
            skLineSegment(sketch, "E987", {"start": v(-81.95, -166.47) * mm, "end": v(-82.13, -166.3) * mm});
            skLineSegment(sketch, "E988", {"start": v(-82.13, -166.3) * mm, "end": v(-82.4, -166.07) * mm});
            skLineSegment(sketch, "E989", {"start": v(-82.4, -166.07) * mm, "end": v(-82.68, -165.87) * mm});
            skLineSegment(sketch, "E990", {"start": v(-82.68, -165.87) * mm, "end": v(-82.98, -165.67) * mm});
            skLineSegment(sketch, "E991", {"start": v(-82.98, -165.67) * mm, "end": v(-83.3, -165.5) * mm});
            skLineSegment(sketch, "E992", {"start": v(-83.3, -165.5) * mm, "end": v(-83.62, -165.33) * mm});
            skLineSegment(sketch, "E993", {"start": v(-83.62, -165.33) * mm, "end": v(-83.97, -165.18) * mm});
            skLineSegment(sketch, "E994", {"start": v(-83.97, -165.18) * mm, "end": v(-84.33, -165.04) * mm});
            skLineSegment(sketch, "E995", {"start": v(-84.33, -165.04) * mm, "end": v(-84.7, -164.92) * mm});
            skLineSegment(sketch, "E996", {"start": v(-84.7, -164.92) * mm, "end": v(-85.1, -164.82) * mm});
            skLineSegment(sketch, "E997", {"start": v(-85.1, -164.82) * mm, "end": v(-85.5, -164.72) * mm});
            skLineSegment(sketch, "E998", {"start": v(-85.5, -164.72) * mm, "end": v(-85.93, -164.64) * mm});
            skLineSegment(sketch, "E999", {"start": v(-85.93, -164.64) * mm, "end": v(-86.37, -164.58) * mm});
            skLineSegment(sketch, "E1000", {"start": v(-86.37, -164.58) * mm, "end": v(-86.82, -164.53) * mm});
            skLineSegment(sketch, "E1001", {"start": v(-86.82, -164.53) * mm, "end": v(-87.3, -164.5) * mm});
            skLineSegment(sketch, "E1002", {"start": v(-87.3, -164.5) * mm, "end": v(-87.78, -164.47) * mm});
            skLineSegment(sketch, "E1003", {"start": v(-87.78, -164.47) * mm, "end": v(-88.28, -164.47) * mm});
            skLineSegment(sketch, "E1004", {"start": v(-88.28, -164.47) * mm, "end": v(-88.75, -164.47) * mm});
            skLineSegment(sketch, "E1005", {"start": v(-88.75, -164.47) * mm, "end": v(-89.2, -164.49) * mm});
            skLineSegment(sketch, "E1006", {"start": v(-89.2, -164.49) * mm, "end": v(-89.64, -164.51) * mm});
            skLineSegment(sketch, "E1007", {"start": v(-89.64, -164.51) * mm, "end": v(-90.06, -164.55) * mm});
            skLineSegment(sketch, "E1008", {"start": v(-90.06, -164.55) * mm, "end": v(-90.47, -164.6) * mm});
            skLineSegment(sketch, "E1009", {"start": v(-90.47, -164.6) * mm, "end": v(-90.86, -164.65) * mm});
            skLineSegment(sketch, "E1010", {"start": v(-90.86, -164.65) * mm, "end": v(-91.23, -164.72) * mm});
            skLineSegment(sketch, "E1011", {"start": v(-91.23, -164.72) * mm, "end": v(-91.6, -164.8) * mm});
            skLineSegment(sketch, "E1012", {"start": v(-91.6, -164.8) * mm, "end": v(-91.93, -164.89) * mm});
            skLineSegment(sketch, "E1013", {"start": v(-91.93, -164.89) * mm, "end": v(-92.26, -164.99) * mm});
            skLineSegment(sketch, "E1014", {"start": v(-92.26, -164.99) * mm, "end": v(-92.58, -165.1) * mm});
            skLineSegment(sketch, "E1015", {"start": v(-92.58, -165.1) * mm, "end": v(-92.87, -165.22) * mm});
            skLineSegment(sketch, "E1016", {"start": v(-92.87, -165.22) * mm, "end": v(-93.15, -165.35) * mm});
            skLineSegment(sketch, "E1017", {"start": v(-93.15, -165.35) * mm, "end": v(-93.42, -165.49) * mm});
            skLineSegment(sketch, "E1018", {"start": v(-93.42, -165.49) * mm, "end": v(-93.67, -165.64) * mm});
            skLineSegment(sketch, "E1019", {"start": v(-93.67, -165.64) * mm, "end": v(-93.9, -165.8) * mm});
            skLineSegment(sketch, "E1020", {"start": v(-93.9, -165.8) * mm, "end": v(-94.13, -165.97) * mm});
            skLineSegment(sketch, "E1021", {"start": v(-94.13, -165.97) * mm, "end": v(-94.34, -166.17) * mm});
            skLineSegment(sketch, "E1022", {"start": v(-94.34, -166.17) * mm, "end": v(-94.55, -166.37) * mm});
            skLineSegment(sketch, "E1023", {"start": v(-94.55, -166.37) * mm, "end": v(-94.75, -166.6) * mm});
            skLineSegment(sketch, "E1024", {"start": v(-94.75, -166.6) * mm, "end": v(-94.95, -166.83) * mm});
            skLineSegment(sketch, "E1025", {"start": v(-94.95, -166.83) * mm, "end": v(-95.13, -167.1) * mm});
            skLineSegment(sketch, "E1026", {"start": v(-95.13, -167.1) * mm, "end": v(-95.31, -167.36) * mm});
            skLineSegment(sketch, "E1027", {"start": v(-95.31, -167.36) * mm, "end": v(-95.48, -167.65) * mm});
            skLineSegment(sketch, "E1028", {"start": v(-95.48, -167.65) * mm, "end": v(-95.65, -167.95) * mm});
            skLineSegment(sketch, "E1029", {"start": v(-95.65, -167.95) * mm, "end": v(-95.8, -168.27) * mm});
            skLineSegment(sketch, "E1030", {"start": v(-95.8, -168.27) * mm, "end": v(-95.95, -168.6) * mm});
            skLineSegment(sketch, "E1031", {"start": v(-95.95, -168.6) * mm, "end": v(-96.1, -168.96) * mm});
            skLineSegment(sketch, "E1032", {"start": v(-96.1, -168.96) * mm, "end": v(-96.23, -169.33) * mm});
            skLineSegment(sketch, "E1033", {"start": v(-96.23, -169.33) * mm, "end": v(-96.36, -169.7) * mm});
            skLineSegment(sketch, "E1034", {"start": v(-96.36, -169.7) * mm, "end": v(-96.48, -170.1) * mm});
            skLineSegment(sketch, "E1035", {"start": v(-96.48, -170.1) * mm, "end": v(-96.59, -170.52) * mm});
            skLineSegment(sketch, "E1036", {"start": v(-96.59, -170.52) * mm, "end": v(-101.87, -169.8) * mm});
            skLineSegment(sketch, "E1037", {"start": v(-101.87, -169.8) * mm, "end": v(-101.67, -168.98) * mm});
            skLineSegment(sketch, "E1038", {"start": v(-101.67, -168.98) * mm, "end": v(-101.45, -168.2) * mm});
            skLineSegment(sketch, "E1039", {"start": v(-101.45, -168.2) * mm, "end": v(-101.2, -167.45) * mm});
            skLineSegment(sketch, "E1040", {"start": v(-101.2, -167.45) * mm, "end": v(-100.92, -166.74) * mm});
            skLineSegment(sketch, "E1041", {"start": v(-100.92, -166.74) * mm, "end": v(-100.6, -166.08) * mm});
            skLineSegment(sketch, "E1042", {"start": v(-100.6, -166.08) * mm, "end": v(-100.27, -165.45) * mm});
            skLineSegment(sketch, "E1043", {"start": v(-100.27, -165.45) * mm, "end": v(-99.9, -164.87) * mm});
            skLineSegment(sketch, "E1044", {"start": v(-99.9, -164.87) * mm, "end": v(-99.5, -164.33) * mm});
            skLineSegment(sketch, "E1045", {"start": v(-99.5, -164.33) * mm, "end": v(-99.06, -163.82) * mm});
            skLineSegment(sketch, "E1046", {"start": v(-99.06, -163.82) * mm, "end": v(-98.58, -163.35) * mm});
            skLineSegment(sketch, "E1047", {"start": v(-98.58, -163.35) * mm, "end": v(-98.05, -162.9) * mm});
            skLineSegment(sketch, "E1048", {"start": v(-98.05, -162.9) * mm, "end": v(-97.48, -162.49) * mm});
            skLineSegment(sketch, "E1049", {"start": v(-97.48, -162.49) * mm, "end": v(-96.86, -162.1) * mm});
            skLineSegment(sketch, "E1050", {"start": v(-96.86, -162.1) * mm, "end": v(-96.2, -161.74) * mm});
            skLineSegment(sketch, "E1051", {"start": v(-96.2, -161.74) * mm, "end": v(-95.49, -161.42) * mm});
            skLineSegment(sketch, "E1052", {"start": v(-95.49, -161.42) * mm, "end": v(-94.73, -161.12) * mm});
            skLineSegment(sketch, "E1053", {"start": v(-94.73, -161.12) * mm, "end": v(-93.93, -160.86) * mm});
            skLineSegment(sketch, "E1054", {"start": v(-93.93, -160.86) * mm, "end": v(-93.1, -160.63) * mm});
            skLineSegment(sketch, "E1055", {"start": v(-93.1, -160.63) * mm, "end": v(-92.25, -160.44) * mm});
            skLineSegment(sketch, "E1056", {"start": v(-92.25, -160.44) * mm, "end": v(-91.36, -160.28) * mm});
            skLineSegment(sketch, "E1057", {"start": v(-91.36, -160.28) * mm, "end": v(-90.44, -160.15) * mm});
            skLineSegment(sketch, "E1058", {"start": v(-90.44, -160.15) * mm, "end": v(-89.5, -160.07) * mm});
            skLineSegment(sketch, "E1059", {"start": v(-89.5, -160.07) * mm, "end": v(-88.51, -160.01) * mm});
            skLineSegment(sketch, "E1060", {"start": v(-88.51, -160.01) * mm, "end": v(-87.5, -160) * mm});
            skLineSegment(sketch, "E1061", {"start": v(-87.5, -160) * mm, "end": v(-86.5, -160.01) * mm});
            skLineSegment(sketch, "E1062", {"start": v(-86.5, -160.01) * mm, "end": v(-85.56, -160.06) * mm});
            skLineSegment(sketch, "E1063", {"start": v(-85.56, -160.06) * mm, "end": v(-84.66, -160.13) * mm});
            skLineSegment(sketch, "E1064", {"start": v(-84.66, -160.13) * mm, "end": v(-83.8, -160.24) * mm});
            skLineSegment(sketch, "E1065", {"start": v(-83.8, -160.24) * mm, "end": v(-83, -160.37) * mm});
            skLineSegment(sketch, "E1066", {"start": v(-83, -160.37) * mm, "end": v(-82.24, -160.54) * mm});
            skLineSegment(sketch, "E1067", {"start": v(-82.24, -160.54) * mm, "end": v(-81.53, -160.73) * mm});
            skLineSegment(sketch, "E1068", {"start": v(-81.53, -160.73) * mm, "end": v(-80.87, -160.96) * mm});
            skLineSegment(sketch, "E1069", {"start": v(-80.87, -160.96) * mm, "end": v(-80.25, -161.2) * mm});
            skLineSegment(sketch, "E1070", {"start": v(-80.25, -161.2) * mm, "end": v(-79.68, -161.47) * mm});
            skLineSegment(sketch, "E1071", {"start": v(-79.68, -161.47) * mm, "end": v(-79.15, -161.75) * mm});
            skLineSegment(sketch, "E1072", {"start": v(-79.15, -161.75) * mm, "end": v(-78.66, -162.04) * mm});
            skLineSegment(sketch, "E1073", {"start": v(-78.66, -162.04) * mm, "end": v(-78.21, -162.35) * mm});
            skLineSegment(sketch, "E1074", {"start": v(-78.21, -162.35) * mm, "end": v(-77.8, -162.67) * mm});
            skLineSegment(sketch, "E1075", {"start": v(-77.8, -162.67) * mm, "end": v(-77.44, -163.01) * mm});
            skLineSegment(sketch, "E1076", {"start": v(-77.44, -163.01) * mm, "end": v(-77.12, -163.37) * mm});
            skLineSegment(sketch, "E1077", {"start": v(-77.12, -163.37) * mm, "end": v(-76.83, -163.75) * mm});
            skLineSegment(sketch, "E1078", {"start": v(-76.83, -163.75) * mm, "end": v(-76.57, -164.15) * mm});
            skLineSegment(sketch, "E1079", {"start": v(-76.57, -164.15) * mm, "end": v(-76.32, -164.57) * mm});
            skLineSegment(sketch, "E1080", {"start": v(-76.32, -164.57) * mm, "end": v(-76.1, -165.02) * mm});
            skLineSegment(sketch, "E1081", {"start": v(-76.1, -165.02) * mm, "end": v(-75.9, -165.49) * mm});
            skLineSegment(sketch, "E1082", {"start": v(-75.9, -165.49) * mm, "end": v(-75.73, -165.98) * mm});
            skLineSegment(sketch, "E1083", {"start": v(-75.73, -165.98) * mm, "end": v(-75.57, -166.5) * mm});
            skLineSegment(sketch, "E1084", {"start": v(-75.57, -166.5) * mm, "end": v(-75.44, -167.04) * mm});
            skLineSegment(sketch, "E1085", {"start": v(-75.44, -167.04) * mm, "end": v(-75.38, -167.42) * mm});
            skLineSegment(sketch, "E1086", {"start": v(-75.38, -167.42) * mm, "end": v(-75.32, -167.87) * mm});
            skLineSegment(sketch, "E1087", {"start": v(-75.32, -167.87) * mm, "end": v(-75.28, -168.4) * mm});
            skLineSegment(sketch, "E1088", {"start": v(-75.28, -168.4) * mm, "end": v(-75.24, -168.98) * mm});
            skLineSegment(sketch, "E1089", {"start": v(-75.24, -168.98) * mm, "end": v(-75.2, -169.64) * mm});
            skLineSegment(sketch, "E1090", {"start": v(-75.2, -169.64) * mm, "end": v(-75.19, -170.36) * mm});
            skLineSegment(sketch, "E1091", {"start": v(-75.19, -170.36) * mm, "end": v(-75.18, -171.16) * mm});
            skLineSegment(sketch, "E1092", {"start": v(-75.18, -171.16) * mm, "end": v(-75.17, -172.02) * mm});
            skLineSegment(sketch, "E1093", {"start": v(-75.17, -172.02) * mm, "end": v(-75.17, -179.22) * mm});
            skLineSegment(sketch, "E1094", {"start": v(-75.17, -179.22) * mm, "end": v(-75.17, -180.14) * mm});
            skLineSegment(sketch, "E1095", {"start": v(-75.17, -180.14) * mm, "end": v(-75.17, -181.02) * mm});
            skLineSegment(sketch, "E1096", {"start": v(-75.17, -181.02) * mm, "end": v(-75.16, -181.85) * mm});
            skLineSegment(sketch, "E1097", {"start": v(-75.16, -181.85) * mm, "end": v(-75.15, -182.64) * mm});
            skLineSegment(sketch, "E1098", {"start": v(-75.15, -182.64) * mm, "end": v(-75.14, -183.39) * mm});
            skLineSegment(sketch, "E1099", {"start": v(-75.14, -183.39) * mm, "end": v(-75.12, -184.1) * mm});
            skLineSegment(sketch, "E1100", {"start": v(-75.12, -184.1) * mm, "end": v(-75.1, -184.75) * mm});
            skLineSegment(sketch, "E1101", {"start": v(-75.1, -184.75) * mm, "end": v(-75.09, -185.37) * mm});
            skLineSegment(sketch, "E1102", {"start": v(-75.09, -185.37) * mm, "end": v(-75.06, -185.94) * mm});
            skLineSegment(sketch, "E1103", {"start": v(-75.06, -185.94) * mm, "end": v(-75.04, -186.47) * mm});
            skLineSegment(sketch, "E1104", {"start": v(-75.04, -186.47) * mm, "end": v(-75, -186.96) * mm});
            skLineSegment(sketch, "E1105", {"start": v(-75, -186.96) * mm, "end": v(-74.98, -187.4) * mm});
            skLineSegment(sketch, "E1106", {"start": v(-74.98, -187.4) * mm, "end": v(-74.94, -187.8) * mm});
            skLineSegment(sketch, "E1107", {"start": v(-74.94, -187.8) * mm, "end": v(-74.9, -188.16) * mm});
            skLineSegment(sketch, "E1108", {"start": v(-74.9, -188.16) * mm, "end": v(-74.87, -188.48) * mm});
            skLineSegment(sketch, "E1109", {"start": v(-74.87, -188.48) * mm, "end": v(-74.83, -188.75) * mm});
            skLineSegment(sketch, "E1110", {"start": v(-74.83, -188.75) * mm, "end": v(-74.73, -189.24) * mm});
            skLineSegment(sketch, "E1111", {"start": v(-74.73, -189.24) * mm, "end": v(-74.61, -189.73) * mm});
            skLineSegment(sketch, "E1112", {"start": v(-74.61, -189.73) * mm, "end": v(-74.47, -190.22) * mm});
            skLineSegment(sketch, "E1113", {"start": v(-74.47, -190.22) * mm, "end": v(-74.31, -190.7) * mm});
            skLineSegment(sketch, "E1114", {"start": v(-74.31, -190.7) * mm, "end": v(-74.13, -191.18) * mm});
            skLineSegment(sketch, "E1115", {"start": v(-74.13, -191.18) * mm, "end": v(-73.93, -191.65) * mm});
            skLineSegment(sketch, "E1116", {"start": v(-73.93, -191.65) * mm, "end": v(-73.7, -192.11) * mm});
            skLineSegment(sketch, "E1117", {"start": v(-73.7, -192.11) * mm, "end": v(-73.46, -192.57) * mm});
            skLineSegment(sketch, "E1118", {"start": v(-73.46, -192.57) * mm, "end": v(-79.1, -192.57) * mm});
            skLineSegment(sketch, "E1119", {"start": v(-79.1, -192.57) * mm, "end": v(-79.3, -192.14) * mm});
            skLineSegment(sketch, "E1120", {"start": v(-79.3, -192.14) * mm, "end": v(-79.48, -191.7) * mm});
            skLineSegment(sketch, "E1121", {"start": v(-79.48, -191.7) * mm, "end": v(-79.65, -191.23) * mm});
            skLineSegment(sketch, "E1122", {"start": v(-79.65, -191.23) * mm, "end": v(-79.8, -190.75) * mm});
            skLineSegment(sketch, "E1123", {"start": v(-79.8, -190.75) * mm, "end": v(-79.92, -190.25) * mm});
            skLineSegment(sketch, "E1124", {"start": v(-79.92, -190.25) * mm, "end": v(-80.02, -189.73) * mm});
            skLineSegment(sketch, "E1125", {"start": v(-80.02, -189.73) * mm, "end": v(-80.11, -189.2) * mm});
            skLineSegment(sketch, "E1126", {"start": v(138.65, -213.3) * mm, "end": v(-138.65, -213.3) * mm});
            skLineSegment(sketch, "E1127", {"start": v(138.65, -213.3) * mm, "end": v(138.65, -220.63) * mm});
            skLineSegment(sketch, "E1128", {"start": v(138.65, -220.63) * mm, "end": v(-138.65, -220.63) * mm});
            skLineSegment(sketch, "E1129", {"start": v(-138.65, -213.3) * mm, "end": v(-138.65, -220.63) * mm});
            skArc(sketch, "E1130", {"start": v(143.75, -131.21) * mm, "mid": v(146.86, -132.5) * mm, "end": v(148.15, -135.61) * mm});
            skLineSegment(sketch, "E1131", {"start": v(143.75, -131.21) * mm, "end": v(143.75, -123.88) * mm});
            skLineSegment(sketch, "E1132", {"start": v(143.75, -123.88) * mm, "end": v(148.15, -123.88) * mm});
            skArc(sketch, "E1133", {"start": v(148.15, -123.88) * mm, "mid": v(153.33, -126.03) * mm, "end": v(155.48, -131.21) * mm});
            skLineSegment(sketch, "E1134", {"start": v(155.48, -131.21) * mm, "end": v(155.48, -213.3) * mm});
            skArc(sketch, "E1135", {"start": v(155.48, -213.3) * mm, "mid": v(153.33, -218.48) * mm, "end": v(148.15, -220.63) * mm});
            skLineSegment(sketch, "E1136", {"start": v(148.15, -220.63) * mm, "end": v(143.75, -220.63) * mm});
            skLineSegment(sketch, "E1137", {"start": v(143.75, -213.3) * mm, "end": v(143.75, -220.63) * mm});
            skArc(sketch, "E1138", {"start": v(148.15, -208.9) * mm, "mid": v(146.86, -212.01) * mm, "end": v(143.75, -213.3) * mm});
            skLineSegment(sketch, "E1139", {"start": v(148.15, -135.61) * mm, "end": v(148.15, -208.9) * mm});
            skLineSegment(sketch, "E1140", {"start": v(-138.65, -131.21) * mm, "end": v(138.65, -131.21) * mm});
            skLineSegment(sketch, "E1141", {"start": v(-138.65, -131.21) * mm, "end": v(-138.65, -123.88) * mm});
            skLineSegment(sketch, "E1142", {"start": v(-138.65, -123.88) * mm, "end": v(138.65, -123.88) * mm});
            skLineSegment(sketch, "E1143", {"start": v(138.65, -131.21) * mm, "end": v(138.65, -123.88) * mm});
            skLineSegment(sketch, "E1144", {"start": v(-6.72, -67.2) * mm, "end": v(-142, 68.08) * mm});
            skLineSegment(sketch, "E1145", {"start": v(-6.72, -67.2) * mm, "end": v(-11.9, -72.39) * mm});
            skLineSegment(sketch, "E1146", {"start": v(-11.9, -72.39) * mm, "end": v(-150.3, 66) * mm});
            skArc(sketch, "E1147", {"start": v(-150.3, 66) * mm, "mid": v(-152.44, 71.2) * mm, "end": v(-150.3, 76.37) * mm});
            skLineSegment(sketch, "E1148", {"start": v(-150.3, 76.37) * mm, "end": v(-147.18, 79.48) * mm});
            skLineSegment(sketch, "E1149", {"start": v(-142, 74.3) * mm, "end": v(-147.18, 79.48) * mm});
            skArc(sketch, "E1150", {"start": v(-142, 68.08) * mm, "mid": v(-143.29, 71.2) * mm, "end": v(-142, 74.3) * mm});
            skLineSegment(sketch, "E1151", {"start": v(138.4, 64.48) * mm, "end": v(3.1, -70.8) * mm});
            skLineSegment(sketch, "E1152", {"start": v(138.4, 64.48) * mm, "end": v(143.58, 59.3) * mm});
            skLineSegment(sketch, "E1153", {"start": v(143.58, 59.3) * mm, "end": v(5.18, -79.1) * mm});
            skArc(sketch, "E1154", {"start": v(5.18, -79.1) * mm, "mid": v(0, -81.25) * mm, "end": v(-5.18, -79.1) * mm});
            skLineSegment(sketch, "E1155", {"start": v(-5.18, -79.1) * mm, "end": v(-8.3, -76) * mm});
            skLineSegment(sketch, "E1156", {"start": v(-3.1, -70.8) * mm, "end": v(-8.3, -76) * mm});
            skArc(sketch, "E1157", {"start": v(3.1, -70.8) * mm, "mid": v(0, -72.1) * mm, "end": v(-3.1, -70.8) * mm});
            skLineSegment(sketch, "E1158", {"start": v(6.72, 209.59) * mm, "end": v(142, 74.3) * mm});
            skLineSegment(sketch, "E1159", {"start": v(6.72, 209.59) * mm, "end": v(11.9, 214.77) * mm});
            skLineSegment(sketch, "E1160", {"start": v(11.9, 214.77) * mm, "end": v(150.3, 76.37) * mm});
            skArc(sketch, "E1161", {"start": v(150.3, 76.37) * mm, "mid": v(152.44, 71.2) * mm, "end": v(150.3, 66) * mm});
            skLineSegment(sketch, "E1162", {"start": v(150.3, 66) * mm, "end": v(147.18, 62.9) * mm});
            skLineSegment(sketch, "E1163", {"start": v(142, 68.08) * mm, "end": v(147.18, 62.9) * mm});
            skArc(sketch, "E1164", {"start": v(142, 74.3) * mm, "mid": v(143.29, 71.2) * mm, "end": v(142, 68.08) * mm});
            skLineSegment(sketch, "E1165", {"start": v(92.92, 42.12) * mm, "end": v(84.45, 51.5) * mm});
            skLineSegment(sketch, "E1166", {"start": v(84.45, 51.5) * mm, "end": v(76.18, 61.04) * mm});
            skLineSegment(sketch, "E1167", {"start": v(76.18, 61.04) * mm, "end": v(67.62, 70.35) * mm});
            skLineSegment(sketch, "E1168", {"start": v(67.62, 70.35) * mm, "end": v(58.3, 78.87) * mm});
            skLineSegment(sketch, "E1169", {"start": v(58.3, 78.87) * mm, "end": v(47.42, 85.3) * mm});
            skLineSegment(sketch, "E1170", {"start": v(47.42, 85.3) * mm, "end": v(39.81, 87.37) * mm});
            skLineSegment(sketch, "E1171", {"start": v(39.81, 87.37) * mm, "end": v(32.08, 86.03) * mm});
            skLineSegment(sketch, "E1172", {"start": v(32.08, 86.03) * mm, "end": v(24.9, 82.62) * mm});
            skLineSegment(sketch, "E1173", {"start": v(24.9, 82.62) * mm, "end": v(17.56, 79.71) * mm});
            skLineSegment(sketch, "E1174", {"start": v(17.56, 79.71) * mm, "end": v(10.13, 77.06) * mm});
            skLineSegment(sketch, "E1175", {"start": v(10.13, 77.06) * mm, "end": v(2.77, 74.17) * mm});
            skLineSegment(sketch, "E1176", {"start": v(2.77, 74.17) * mm, "end": v(-4.61, 71.37) * mm});
            skLineSegment(sketch, "E1177", {"start": v(-4.61, 71.37) * mm, "end": v(-12.16, 69.12) * mm});
            skLineSegment(sketch, "E1178", {"start": v(-12.16, 69.12) * mm, "end": v(-17.35, 68.1) * mm});
            skLineSegment(sketch, "E1179", {"start": v(-17.35, 68.1) * mm, "end": v(-22.56, 67.14) * mm});
            skLineSegment(sketch, "E1180", {"start": v(-22.56, 67.14) * mm, "end": v(-27.06, 64.5) * mm});
            skLineSegment(sketch, "E1181", {"start": v(-27.06, 64.5) * mm, "end": v(-31.45, 57.9) * mm});
            skLineSegment(sketch, "E1182", {"start": v(-31.45, 57.9) * mm, "end": v(-32.43, 50.04) * mm});
            skLineSegment(sketch, "E1183", {"start": v(-32.43, 50.04) * mm, "end": v(-31.18, 45.01) * mm});
            skLineSegment(sketch, "E1184", {"start": v(-31.18, 45.01) * mm, "end": v(-29.97, 42.5) * mm});
            skLineSegment(sketch, "E1185", {"start": v(-29.97, 42.5) * mm, "end": v(-29.08, 41.6) * mm});
            skLineSegment(sketch, "E1186", {"start": v(-29.08, 41.6) * mm, "end": v(-27.86, 41.39) * mm});
            skLineSegment(sketch, "E1187", {"start": v(-27.86, 41.39) * mm, "end": v(-24, 41.83) * mm});
            skLineSegment(sketch, "E1188", {"start": v(-24, 41.83) * mm, "end": v(-20.34, 41.88) * mm});
            skLineSegment(sketch, "E1189", {"start": v(-20.34, 41.88) * mm, "end": v(-14.56, 41.49) * mm});
            skLineSegment(sketch, "E1190", {"start": v(-14.56, 41.49) * mm, "end": v(-8.75, 40.47) * mm});
            skLineSegment(sketch, "E1191", {"start": v(-8.75, 40.47) * mm, "end": v(-6.39, 39.95) * mm});
            skLineSegment(sketch, "E1192", {"start": v(-6.39, 39.95) * mm, "end": v(-4.36, 38.9) * mm});
            skLineSegment(sketch, "E1193", {"start": v(-4.36, 38.9) * mm, "end": v(-4.12, 38.6) * mm});
            skLineSegment(sketch, "E1194", {"start": v(-4.12, 38.6) * mm, "end": v(-4.24, 38.37) * mm});
            skLineSegment(sketch, "E1195", {"start": v(-4.24, 38.37) * mm, "end": v(-4.53, 38.24) * mm});
            skLineSegment(sketch, "E1196", {"start": v(-4.53, 38.24) * mm, "end": v(-5.3, 38.08) * mm});
            skLineSegment(sketch, "E1197", {"start": v(-5.3, 38.08) * mm, "end": v(-8.55, 37.96) * mm});
            skLineSegment(sketch, "E1198", {"start": v(-8.55, 37.96) * mm, "end": v(-11.38, 38.04) * mm});
            skLineSegment(sketch, "E1199", {"start": v(-11.38, 38.04) * mm, "end": v(-14.3, 37.99) * mm});
            skLineSegment(sketch, "E1200", {"start": v(-14.3, 37.99) * mm, "end": v(-17.49, 38.05) * mm});
            skLineSegment(sketch, "E1201", {"start": v(-17.49, 38.05) * mm, "end": v(-18.08, 37.99) * mm});
            skLineSegment(sketch, "E1202", {"start": v(-18.08, 37.99) * mm, "end": v(-18.4, 37.83) * mm});
            skLineSegment(sketch, "E1203", {"start": v(-18.4, 37.83) * mm, "end": v(-18.45, 37.02) * mm});
            skLineSegment(sketch, "E1204", {"start": v(-18.45, 37.02) * mm, "end": v(-17.53, 35.88) * mm});
            skLineSegment(sketch, "E1205", {"start": v(-17.53, 35.88) * mm, "end": v(-16.25, 35.56) * mm});
            skLineSegment(sketch, "E1206", {"start": v(-16.25, 35.56) * mm, "end": v(-11.91, 34.66) * mm});
            skLineSegment(sketch, "E1207", {"start": v(-11.91, 34.66) * mm, "end": v(-8.69, 33.42) * mm});
            skLineSegment(sketch, "E1208", {"start": v(-8.69, 33.42) * mm, "end": v(-7.87, 32.23) * mm});
            skLineSegment(sketch, "E1209", {"start": v(-7.87, 32.23) * mm, "end": v(-7.74, 31.57) * mm});
            skLineSegment(sketch, "E1210", {"start": v(-7.74, 31.57) * mm, "end": v(-7.94, 31.14) * mm});
            skLineSegment(sketch, "E1211", {"start": v(-7.94, 31.14) * mm, "end": v(-8.43, 31.02) * mm});
            skLineSegment(sketch, "E1212", {"start": v(-8.43, 31.02) * mm, "end": v(-8.95, 31.05) * mm});
            skLineSegment(sketch, "E1213", {"start": v(-8.95, 31.05) * mm, "end": v(-10.03, 31.26) * mm});
            skLineSegment(sketch, "E1214", {"start": v(-10.03, 31.26) * mm, "end": v(-11.83, 31.58) * mm});
            skLineSegment(sketch, "E1215", {"start": v(-11.83, 31.58) * mm, "end": v(-15.13, 32) * mm});
            skLineSegment(sketch, "E1216", {"start": v(-15.13, 32) * mm, "end": v(-18.47, 32.89) * mm});
            skLineSegment(sketch, "E1217", {"start": v(-18.47, 32.89) * mm, "end": v(-21.89, 33.77) * mm});
            skLineSegment(sketch, "E1218", {"start": v(-21.89, 33.77) * mm, "end": v(-23.48, 34.42) * mm});
            skLineSegment(sketch, "E1219", {"start": v(-23.48, 34.42) * mm, "end": v(-24.59, 34.51) * mm});
            skLineSegment(sketch, "E1220", {"start": v(-24.59, 34.51) * mm, "end": v(-25.33, 34.26) * mm});
            skLineSegment(sketch, "E1221", {"start": v(-25.33, 34.26) * mm, "end": v(-25.47, 33.82) * mm});
            skLineSegment(sketch, "E1222", {"start": v(-25.47, 33.82) * mm, "end": v(-25.24, 33.25) * mm});
            skLineSegment(sketch, "E1223", {"start": v(-25.24, 33.25) * mm, "end": v(-24.32, 32.33) * mm});
            skLineSegment(sketch, "E1224", {"start": v(-24.32, 32.33) * mm, "end": v(-22.18, 31.46) * mm});
            skLineSegment(sketch, "E1225", {"start": v(-22.18, 31.46) * mm, "end": v(-18.39, 29.2) * mm});
            skLineSegment(sketch, "E1226", {"start": v(-18.39, 29.2) * mm, "end": v(-16.86, 28.3) * mm});
            skLineSegment(sketch, "E1227", {"start": v(-16.86, 28.3) * mm, "end": v(-15.88, 26.88) * mm});
            skLineSegment(sketch, "E1228", {"start": v(-15.88, 26.88) * mm, "end": v(-15.94, 26.23) * mm});
            skLineSegment(sketch, "E1229", {"start": v(-15.94, 26.23) * mm, "end": v(-16.34, 25.9) * mm});
            skLineSegment(sketch, "E1230", {"start": v(-16.34, 25.9) * mm, "end": v(-17.78, 26.03) * mm});
            skLineSegment(sketch, "E1231", {"start": v(-17.78, 26.03) * mm, "end": v(-21.4, 27.07) * mm});
            skLineSegment(sketch, "E1232", {"start": v(-21.4, 27.07) * mm, "end": v(-29.3, 30.8) * mm});
            skLineSegment(sketch, "E1233", {"start": v(-29.3, 30.8) * mm, "end": v(-32.03, 32.96) * mm});
            skLineSegment(sketch, "E1234", {"start": v(-32.03, 32.96) * mm, "end": v(-33.93, 35.77) * mm});
            skLineSegment(sketch, "E1235", {"start": v(-33.93, 35.77) * mm, "end": v(-34.45, 40.24) * mm});
            skLineSegment(sketch, "E1236", {"start": v(-34.45, 40.24) * mm, "end": v(-35.4, 44.54) * mm});
            skLineSegment(sketch, "E1237", {"start": v(-35.4, 44.54) * mm, "end": v(-36.7, 47.78) * mm});
            skLineSegment(sketch, "E1238", {"start": v(-36.7, 47.78) * mm, "end": v(-38.76, 50.6) * mm});
            skLineSegment(sketch, "E1239", {"start": v(-38.76, 50.6) * mm, "end": v(-41.2, 51.4) * mm});
            skLineSegment(sketch, "E1240", {"start": v(-41.2, 51.4) * mm, "end": v(-43.49, 50.02) * mm});
            skLineSegment(sketch, "E1241", {"start": v(-43.49, 50.02) * mm, "end": v(-45.62, 48.37) * mm});
            skLineSegment(sketch, "E1242", {"start": v(-45.62, 48.37) * mm, "end": v(-47.07, 46.27) * mm});
            skLineSegment(sketch, "E1243", {"start": v(-47.07, 46.27) * mm, "end": v(-47.45, 41.81) * mm});
            skLineSegment(sketch, "E1244", {"start": v(-47.45, 41.81) * mm, "end": v(-46.24, 37.55) * mm});
            skLineSegment(sketch, "E1245", {"start": v(-46.24, 37.55) * mm, "end": v(-44.05, 30.96) * mm});
            skLineSegment(sketch, "E1246", {"start": v(-44.05, 30.96) * mm, "end": v(-42.47, 27.34) * mm});
            skLineSegment(sketch, "E1247", {"start": v(-42.47, 27.34) * mm, "end": v(-39.6, 24.62) * mm});
            skLineSegment(sketch, "E1248", {"start": v(-39.6, 24.62) * mm, "end": v(-35.88, 23.39) * mm});
            skLineSegment(sketch, "E1249", {"start": v(-35.88, 23.39) * mm, "end": v(-31.92, 22.66) * mm});
            skLineSegment(sketch, "E1250", {"start": v(-31.92, 22.66) * mm, "end": v(-28, 20.87) * mm});
            skLineSegment(sketch, "E1251", {"start": v(-28, 20.87) * mm, "end": v(-26.2, 19.95) * mm});
            skLineSegment(sketch, "E1252", {"start": v(-26.2, 19.95) * mm, "end": v(-24.78, 19.23) * mm});
            skLineSegment(sketch, "E1253", {"start": v(-24.78, 19.23) * mm, "end": v(-24.45, 18.68) * mm});
            skLineSegment(sketch, "E1254", {"start": v(-24.45, 18.68) * mm, "end": v(-24.43, 18) * mm});
            skLineSegment(sketch, "E1255", {"start": v(-24.43, 18) * mm, "end": v(-24.7, 17.54) * mm});
            skLineSegment(sketch, "E1256", {"start": v(-24.7, 17.54) * mm, "end": v(-25.22, 17.42) * mm});
            skLineSegment(sketch, "E1257", {"start": v(-25.22, 17.42) * mm, "end": v(-27.33, 18.12) * mm});
            skLineSegment(sketch, "E1258", {"start": v(-27.33, 18.12) * mm, "end": v(-28.93, 18.88) * mm});
            skLineSegment(sketch, "E1259", {"start": v(-28.93, 18.88) * mm, "end": v(-31.2, 19.86) * mm});
            skLineSegment(sketch, "E1260", {"start": v(-31.2, 19.86) * mm, "end": v(-35.61, 21.07) * mm});
            skLineSegment(sketch, "E1261", {"start": v(-35.61, 21.07) * mm, "end": v(-36.88, 21.2) * mm});
            skLineSegment(sketch, "E1262", {"start": v(-36.88, 21.2) * mm, "end": v(-37.52, 21.01) * mm});
            skLineSegment(sketch, "E1263", {"start": v(-37.52, 21.01) * mm, "end": v(-37.63, 20.61) * mm});
            skLineSegment(sketch, "E1264", {"start": v(-37.63, 20.61) * mm, "end": v(-37.35, 19.83) * mm});
            skLineSegment(sketch, "E1265", {"start": v(-37.35, 19.83) * mm, "end": v(-35, 17.08) * mm});
            skLineSegment(sketch, "E1266", {"start": v(-35, 17.08) * mm, "end": v(-32.6, 15.68) * mm});
            skLineSegment(sketch, "E1267", {"start": v(-32.6, 15.68) * mm, "end": v(-30.63, 14.59) * mm});
            skLineSegment(sketch, "E1268", {"start": v(-30.63, 14.59) * mm, "end": v(-29, 12.61) * mm});
            skLineSegment(sketch, "E1269", {"start": v(-29, 12.61) * mm, "end": v(-28.71, 11.76) * mm});
            skLineSegment(sketch, "E1270", {"start": v(-28.71, 11.76) * mm, "end": v(-28.72, 11.43) * mm});
            skLineSegment(sketch, "E1271", {"start": v(-28.72, 11.43) * mm, "end": v(-28.85, 11.23) * mm});
            skLineSegment(sketch, "E1272", {"start": v(-28.85, 11.23) * mm, "end": v(-29.54, 11.15) * mm});
            skLineSegment(sketch, "E1273", {"start": v(-29.54, 11.15) * mm, "end": v(-30.36, 11.38) * mm});
            skLineSegment(sketch, "E1274", {"start": v(-30.36, 11.38) * mm, "end": v(-33.14, 12.74) * mm});
            skLineSegment(sketch, "E1275", {"start": v(-33.14, 12.74) * mm, "end": v(-35.18, 14.02) * mm});
            skLineSegment(sketch, "E1276", {"start": v(-35.18, 14.02) * mm, "end": v(-39, 16.02) * mm});
            skLineSegment(sketch, "E1277", {"start": v(-39, 16.02) * mm, "end": v(-40.76, 16.51) * mm});
            skLineSegment(sketch, "E1278", {"start": v(-40.76, 16.51) * mm, "end": v(-42.05, 16.6) * mm});
            skLineSegment(sketch, "E1279", {"start": v(-42.05, 16.6) * mm, "end": v(-42.35, 16.47) * mm});
            skLineSegment(sketch, "E1280", {"start": v(-42.35, 16.47) * mm, "end": v(-42.48, 16.2) * mm});
            skLineSegment(sketch, "E1281", {"start": v(-42.48, 16.2) * mm, "end": v(-42.3, 15.41) * mm});
            skLineSegment(sketch, "E1282", {"start": v(-42.3, 15.41) * mm, "end": v(-41.94, 14.74) * mm});
            skLineSegment(sketch, "E1283", {"start": v(-41.94, 14.74) * mm, "end": v(-41.18, 13.77) * mm});
            skLineSegment(sketch, "E1284", {"start": v(-41.18, 13.77) * mm, "end": v(-39.55, 11.84) * mm});
            skLineSegment(sketch, "E1285", {"start": v(-39.55, 11.84) * mm, "end": v(-37.55, 6.98) * mm});
            skLineSegment(sketch, "E1286", {"start": v(-37.55, 6.98) * mm, "end": v(-37.38, 5.37) * mm});
            skLineSegment(sketch, "E1287", {"start": v(-37.38, 5.37) * mm, "end": v(-37.5, 4.98) * mm});
            skLineSegment(sketch, "E1288", {"start": v(-37.5, 4.98) * mm, "end": v(-37.75, 4.87) * mm});
            skLineSegment(sketch, "E1289", {"start": v(-37.75, 4.87) * mm, "end": v(-38.15, 5.02) * mm});
            skLineSegment(sketch, "E1290", {"start": v(-38.15, 5.02) * mm, "end": v(-38.54, 5.3) * mm});
            skLineSegment(sketch, "E1291", {"start": v(-38.54, 5.3) * mm, "end": v(-39.37, 6.04) * mm});
            skLineSegment(sketch, "E1292", {"start": v(-39.37, 6.04) * mm, "end": v(-41.1, 7.88) * mm});
            skLineSegment(sketch, "E1293", {"start": v(-41.1, 7.88) * mm, "end": v(-45.26, 12.32) * mm});
            skLineSegment(sketch, "E1294", {"start": v(-45.26, 12.32) * mm, "end": v(-49.58, 16.73) * mm});
            skLineSegment(sketch, "E1295", {"start": v(-49.58, 16.73) * mm, "end": v(-52.35, 22.03) * mm});
            skLineSegment(sketch, "E1296", {"start": v(-52.35, 22.03) * mm, "end": v(-53.02, 28.17) * mm});
            skLineSegment(sketch, "E1297", {"start": v(-53.02, 28.17) * mm, "end": v(-52.9, 34.53) * mm});
            skLineSegment(sketch, "E1298", {"start": v(-52.9, 34.53) * mm, "end": v(-53.03, 40.93) * mm});
            skLineSegment(sketch, "E1299", {"start": v(-53.03, 40.93) * mm, "end": v(-55.17, 46.88) * mm});
            skLineSegment(sketch, "E1300", {"start": v(-55.17, 46.88) * mm, "end": v(-60.57, 52.9) * mm});
            skLineSegment(sketch, "E1301", {"start": v(-60.57, 52.9) * mm, "end": v(-66.9, 58.1) * mm});
            skLineSegment(sketch, "E1302", {"start": v(-66.9, 58.1) * mm, "end": v(-73.09, 63.54) * mm});
            skLineSegment(sketch, "E1303", {"start": v(-73.09, 63.54) * mm, "end": v(-78.28, 71.42) * mm});
            skLineSegment(sketch, "E1304", {"start": v(-78.28, 71.42) * mm, "end": v(-80.5, 80.86) * mm});
            skLineSegment(sketch, "E1305", {"start": v(-80.5, 80.86) * mm, "end": v(-80.61, 91.8) * mm});
            skLineSegment(sketch, "E1306", {"start": v(-80.61, 91.8) * mm, "end": v(-78.72, 102.52) * mm});
            skLineSegment(sketch, "E1307", {"start": v(-78.72, 102.52) * mm, "end": v(-74.74, 112.65) * mm});
            skLineSegment(sketch, "E1308", {"start": v(-74.74, 112.65) * mm, "end": v(-68.45, 121.56) * mm});
            skLineSegment(sketch, "E1309", {"start": v(-68.45, 121.56) * mm, "end": v(-60.45, 129.11) * mm});
            skLineSegment(sketch, "E1310", {"start": v(-60.45, 129.11) * mm, "end": v(-51.27, 135.1) * mm});
            skLineSegment(sketch, "E1311", {"start": v(-51.27, 135.1) * mm, "end": v(-39.82, 139.43) * mm});
            skLineSegment(sketch, "E1312", {"start": v(-39.82, 139.43) * mm, "end": v(-27.65, 140.93) * mm});
            skLineSegment(sketch, "E1313", {"start": v(-27.65, 140.93) * mm, "end": v(-15.44, 139.97) * mm});
            skLineSegment(sketch, "E1314", {"start": v(-15.44, 139.97) * mm, "end": v(-3.48, 136.93) * mm});
            skLineSegment(sketch, "E1315", {"start": v(-3.48, 136.93) * mm, "end": v(7.03, 130.76) * mm});
            skLineSegment(sketch, "E1316", {"start": v(7.03, 130.76) * mm, "end": v(15.1, 121.56) * mm});
            skLineSegment(sketch, "E1317", {"start": v(15.1, 121.56) * mm, "end": v(18.95, 116.7) * mm});
            skLineSegment(sketch, "E1318", {"start": v(18.95, 116.7) * mm, "end": v(23.85, 113.07) * mm});
            skLineSegment(sketch, "E1319", {"start": v(23.85, 113.07) * mm, "end": v(29.95, 112.68) * mm});
            skLineSegment(sketch, "E1320", {"start": v(29.95, 112.68) * mm, "end": v(35.7, 114.83) * mm});
            skLineSegment(sketch, "E1321", {"start": v(35.7, 114.83) * mm, "end": v(41.8, 115) * mm});
            skLineSegment(sketch, "E1322", {"start": v(41.8, 115) * mm, "end": v(47.6, 112.94) * mm});
            skLineSegment(sketch, "E1323", {"start": v(47.6, 112.94) * mm, "end": v(52.57, 109.27) * mm});
            skLineSegment(sketch, "E1324", {"start": v(52.57, 109.27) * mm, "end": v(56.41, 104.47) * mm});
            skLineSegment(sketch, "E1325", {"start": v(56.41, 104.47) * mm, "end": v(59.44, 96.91) * mm});
            skLineSegment(sketch, "E1326", {"start": v(59.44, 96.91) * mm, "end": v(61.2, 88.94) * mm});
            skLineSegment(sketch, "E1327", {"start": v(61.2, 88.94) * mm, "end": v(65.07, 81.8) * mm});
            skLineSegment(sketch, "E1328", {"start": v(65.07, 81.8) * mm, "end": v(70.41, 75.5) * mm});
            skLineSegment(sketch, "E1329", {"start": v(70.41, 75.5) * mm, "end": v(75.74, 69.38) * mm});
            skLineSegment(sketch, "E1330", {"start": v(75.74, 69.38) * mm, "end": v(80.85, 63.13) * mm});
            skLineSegment(sketch, "E1331", {"start": v(80.85, 63.13) * mm, "end": v(85.68, 56.57) * mm});
            skLineSegment(sketch, "E1332", {"start": v(85.68, 56.57) * mm, "end": v(90.39, 49.78) * mm});
            skLineSegment(sketch, "E1333", {"start": v(90.39, 49.78) * mm, "end": v(92.92, 42.12) * mm});
            skLineSegment(sketch, "E1334", {"start": v(99.02, -192.57) * mm, "end": v(93.62, -192.57) * mm});
            skLineSegment(sketch, "E1335", {"start": v(93.62, -192.57) * mm, "end": v(93.62, -160.72) * mm});
            skLineSegment(sketch, "E1336", {"start": v(93.62, -160.72) * mm, "end": v(98.48, -160.72) * mm});
            skLineSegment(sketch, "E1337", {"start": v(98.48, -160.72) * mm, "end": v(98.48, -165.55) * mm});
            skLineSegment(sketch, "E1338", {"start": v(98.48, -165.55) * mm, "end": v(98.71, -165.13) * mm});
            skLineSegment(sketch, "E1339", {"start": v(98.71, -165.13) * mm, "end": v(98.94, -164.73) * mm});
            skLineSegment(sketch, "E1340", {"start": v(98.94, -164.73) * mm, "end": v(99.17, -164.36) * mm});
            skLineSegment(sketch, "E1341", {"start": v(99.17, -164.36) * mm, "end": v(99.4, -164) * mm});
            skLineSegment(sketch, "E1342", {"start": v(99.4, -164) * mm, "end": v(99.61, -163.65) * mm});
            skLineSegment(sketch, "E1343", {"start": v(99.61, -163.65) * mm, "end": v(99.83, -163.33) * mm});
            skLineSegment(sketch, "E1344", {"start": v(99.83, -163.33) * mm, "end": v(100.05, -163.02) * mm});
            skLineSegment(sketch, "E1345", {"start": v(100.05, -163.02) * mm, "end": v(100.27, -162.73) * mm});
            skLineSegment(sketch, "E1346", {"start": v(100.27, -162.73) * mm, "end": v(100.48, -162.46) * mm});
            skLineSegment(sketch, "E1347", {"start": v(100.48, -162.46) * mm, "end": v(100.7, -162.21) * mm});
            skLineSegment(sketch, "E1348", {"start": v(100.7, -162.21) * mm, "end": v(100.9, -161.98) * mm});
            skLineSegment(sketch, "E1349", {"start": v(100.9, -161.98) * mm, "end": v(101.1, -161.76) * mm});
            skLineSegment(sketch, "E1350", {"start": v(101.1, -161.76) * mm, "end": v(101.31, -161.56) * mm});
            skLineSegment(sketch, "E1351", {"start": v(101.31, -161.56) * mm, "end": v(101.52, -161.38) * mm});
            skLineSegment(sketch, "E1352", {"start": v(101.52, -161.38) * mm, "end": v(101.72, -161.22) * mm});
            skLineSegment(sketch, "E1353", {"start": v(101.72, -161.22) * mm, "end": v(101.91, -161.08) * mm});
            skLineSegment(sketch, "E1354", {"start": v(101.91, -161.08) * mm, "end": v(102.31, -160.82) * mm});
            skLineSegment(sketch, "E1355", {"start": v(102.31, -160.82) * mm, "end": v(102.72, -160.6) * mm});
            skLineSegment(sketch, "E1356", {"start": v(102.72, -160.6) * mm, "end": v(103.14, -160.42) * mm});
            skLineSegment(sketch, "E1357", {"start": v(103.14, -160.42) * mm, "end": v(103.57, -160.27) * mm});
            skLineSegment(sketch, "E1358", {"start": v(103.57, -160.27) * mm, "end": v(104, -160.15) * mm});
            skLineSegment(sketch, "E1359", {"start": v(104, -160.15) * mm, "end": v(104.45, -160.06) * mm});
            skLineSegment(sketch, "E1360", {"start": v(104.45, -160.06) * mm, "end": v(104.91, -160.01) * mm});
            skLineSegment(sketch, "E1361", {"start": v(104.91, -160.01) * mm, "end": v(105.38, -160) * mm});
            skLineSegment(sketch, "E1362", {"start": v(105.38, -160) * mm, "end": v(106.06, -160.02) * mm});
            skLineSegment(sketch, "E1363", {"start": v(106.06, -160.02) * mm, "end": v(106.75, -160.1) * mm});
            skLineSegment(sketch, "E1364", {"start": v(106.75, -160.1) * mm, "end": v(107.44, -160.24) * mm});
            skLineSegment(sketch, "E1365", {"start": v(107.44, -160.24) * mm, "end": v(108.13, -160.43) * mm});
            skLineSegment(sketch, "E1366", {"start": v(108.13, -160.43) * mm, "end": v(108.83, -160.68) * mm});
            skLineSegment(sketch, "E1367", {"start": v(108.83, -160.68) * mm, "end": v(109.52, -160.97) * mm});
            skLineSegment(sketch, "E1368", {"start": v(109.52, -160.97) * mm, "end": v(110.22, -161.33) * mm});
            skLineSegment(sketch, "E1369", {"start": v(110.22, -161.33) * mm, "end": v(110.93, -161.74) * mm});
            skLineSegment(sketch, "E1370", {"start": v(110.93, -161.74) * mm, "end": v(109.07, -166.74) * mm});
            skLineSegment(sketch, "E1371", {"start": v(109.07, -166.74) * mm, "end": v(108.57, -166.47) * mm});
            skLineSegment(sketch, "E1372", {"start": v(108.57, -166.47) * mm, "end": v(108.08, -166.23) * mm});
            skLineSegment(sketch, "E1373", {"start": v(108.08, -166.23) * mm, "end": v(107.58, -166.03) * mm});
            skLineSegment(sketch, "E1374", {"start": v(107.58, -166.03) * mm, "end": v(107.09, -165.87) * mm});
            skLineSegment(sketch, "E1375", {"start": v(107.09, -165.87) * mm, "end": v(106.6, -165.74) * mm});
            skLineSegment(sketch, "E1376", {"start": v(106.6, -165.74) * mm, "end": v(106.1, -165.65) * mm});
            skLineSegment(sketch, "E1377", {"start": v(106.1, -165.65) * mm, "end": v(105.6, -165.6) * mm});
            skLineSegment(sketch, "E1378", {"start": v(105.6, -165.6) * mm, "end": v(105.1, -165.58) * mm});
            skLineSegment(sketch, "E1379", {"start": v(105.1, -165.58) * mm, "end": v(104.67, -165.6) * mm});
            skLineSegment(sketch, "E1380", {"start": v(104.67, -165.6) * mm, "end": v(104.25, -165.64) * mm});
            skLineSegment(sketch, "E1381", {"start": v(104.25, -165.64) * mm, "end": v(103.83, -165.72) * mm});
            skLineSegment(sketch, "E1382", {"start": v(103.83, -165.72) * mm, "end": v(103.43, -165.84) * mm});
            skLineSegment(sketch, "E1383", {"start": v(103.43, -165.84) * mm, "end": v(103.04, -166) * mm});
            skLineSegment(sketch, "E1384", {"start": v(103.04, -166) * mm, "end": v(102.66, -166.17) * mm});
            skLineSegment(sketch, "E1385", {"start": v(102.66, -166.17) * mm, "end": v(102.29, -166.4) * mm});
            skLineSegment(sketch, "E1386", {"start": v(102.29, -166.4) * mm, "end": v(101.93, -166.64) * mm});
            skLineSegment(sketch, "E1387", {"start": v(101.93, -166.64) * mm, "end": v(101.59, -166.92) * mm});
            skLineSegment(sketch, "E1388", {"start": v(101.59, -166.92) * mm, "end": v(101.27, -167.22) * mm});
            skLineSegment(sketch, "E1389", {"start": v(101.27, -167.22) * mm, "end": v(100.99, -167.55) * mm});
            skLineSegment(sketch, "E1390", {"start": v(100.99, -167.55) * mm, "end": v(100.72, -167.91) * mm});
            skLineSegment(sketch, "E1391", {"start": v(100.72, -167.91) * mm, "end": v(100.48, -168.3) * mm});
            skLineSegment(sketch, "E1392", {"start": v(100.48, -168.3) * mm, "end": v(100.27, -168.7) * mm});
            skLineSegment(sketch, "E1393", {"start": v(100.27, -168.7) * mm, "end": v(100.08, -169.14) * mm});
            skLineSegment(sketch, "E1394", {"start": v(100.08, -169.14) * mm, "end": v(99.92, -169.6) * mm});
            skLineSegment(sketch, "E1395", {"start": v(99.92, -169.6) * mm, "end": v(99.7, -170.32) * mm});
            skLineSegment(sketch, "E1396", {"start": v(99.7, -170.32) * mm, "end": v(99.53, -171.07) * mm});
            skLineSegment(sketch, "E1397", {"start": v(99.53, -171.07) * mm, "end": v(99.37, -171.83) * mm});
            skLineSegment(sketch, "E1398", {"start": v(99.37, -171.83) * mm, "end": v(99.24, -172.6) * mm});
            skLineSegment(sketch, "E1399", {"start": v(99.24, -172.6) * mm, "end": v(99.15, -173.4) * mm});
            skLineSegment(sketch, "E1400", {"start": v(99.15, -173.4) * mm, "end": v(99.08, -174.22) * mm});
            skLineSegment(sketch, "E1401", {"start": v(99.08, -174.22) * mm, "end": v(99.03, -175.05) * mm});
            skLineSegment(sketch, "E1402", {"start": v(99.03, -175.05) * mm, "end": v(99.02, -175.9) * mm});
            skLineSegment(sketch, "E1403", {"start": v(99.02, -175.9) * mm, "end": v(99.02, -192.57) * mm});
            skLineSegment(sketch, "E1404", {"start": v(47.06, -177.84) * mm, "end": v(47.21, -177.15) * mm});
            skLineSegment(sketch, "E1405", {"start": v(47.21, -177.15) * mm, "end": v(53.03, -178.62) * mm});
            skLineSegment(sketch, "E1406", {"start": v(53.03, -178.62) * mm, "end": v(52.8, -179.5) * mm});
            skLineSegment(sketch, "E1407", {"start": v(52.8, -179.5) * mm, "end": v(52.53, -180.36) * mm});
            skLineSegment(sketch, "E1408", {"start": v(52.53, -180.36) * mm, "end": v(52.25, -181.2) * mm});
            skLineSegment(sketch, "E1409", {"start": v(52.25, -181.2) * mm, "end": v(51.94, -182) * mm});
            skLineSegment(sketch, "E1410", {"start": v(51.94, -182) * mm, "end": v(51.6, -182.77) * mm});
            skLineSegment(sketch, "E1411", {"start": v(51.6, -182.77) * mm, "end": v(51.25, -183.52) * mm});
            skLineSegment(sketch, "E1412", {"start": v(51.25, -183.52) * mm, "end": v(50.87, -184.24) * mm});
            skLineSegment(sketch, "E1413", {"start": v(50.87, -184.24) * mm, "end": v(50.47, -184.94) * mm});
            skLineSegment(sketch, "E1414", {"start": v(50.47, -184.94) * mm, "end": v(50.05, -185.61) * mm});
            skLineSegment(sketch, "E1415", {"start": v(50.05, -185.61) * mm, "end": v(49.6, -186.26) * mm});
            skLineSegment(sketch, "E1416", {"start": v(49.6, -186.26) * mm, "end": v(49.14, -186.87) * mm});
            skLineSegment(sketch, "E1417", {"start": v(49.14, -186.87) * mm, "end": v(48.64, -187.46) * mm});
            skLineSegment(sketch, "E1418", {"start": v(48.64, -187.46) * mm, "end": v(48.13, -188.03) * mm});
            skLineSegment(sketch, "E1419", {"start": v(48.13, -188.03) * mm, "end": v(47.6, -188.56) * mm});
            skLineSegment(sketch, "E1420", {"start": v(47.6, -188.56) * mm, "end": v(47.03, -189.07) * mm});
            skLineSegment(sketch, "E1421", {"start": v(47.03, -189.07) * mm, "end": v(46.45, -189.56) * mm});
            skLineSegment(sketch, "E1422", {"start": v(46.45, -189.56) * mm, "end": v(45.85, -190.01) * mm});
            skLineSegment(sketch, "E1423", {"start": v(45.85, -190.01) * mm, "end": v(45.23, -190.44) * mm});
            skLineSegment(sketch, "E1424", {"start": v(45.23, -190.44) * mm, "end": v(44.6, -190.84) * mm});
            skLineSegment(sketch, "E1425", {"start": v(44.6, -190.84) * mm, "end": v(43.94, -191.2) * mm});
            skLineSegment(sketch, "E1426", {"start": v(43.94, -191.2) * mm, "end": v(43.27, -191.54) * mm});
            skLineSegment(sketch, "E1427", {"start": v(43.27, -191.54) * mm, "end": v(42.59, -191.85) * mm});
            skLineSegment(sketch, "E1428", {"start": v(42.59, -191.85) * mm, "end": v(41.88, -192.13) * mm});
            skLineSegment(sketch, "E1429", {"start": v(41.88, -192.13) * mm, "end": v(41.17, -192.38) * mm});
            skLineSegment(sketch, "E1430", {"start": v(41.17, -192.38) * mm, "end": v(40.43, -192.6) * mm});
            skLineSegment(sketch, "E1431", {"start": v(40.43, -192.6) * mm, "end": v(39.68, -192.8) * mm});
            skLineSegment(sketch, "E1432", {"start": v(39.68, -192.8) * mm, "end": v(38.91, -192.95) * mm});
            skLineSegment(sketch, "E1433", {"start": v(38.91, -192.95) * mm, "end": v(38.13, -193.09) * mm});
            skLineSegment(sketch, "E1434", {"start": v(38.13, -193.09) * mm, "end": v(37.33, -193.19) * mm});
            skLineSegment(sketch, "E1435", {"start": v(37.33, -193.19) * mm, "end": v(36.51, -193.26) * mm});
            skLineSegment(sketch, "E1436", {"start": v(36.51, -193.26) * mm, "end": v(35.68, -193.3) * mm});
            skLineSegment(sketch, "E1437", {"start": v(35.68, -193.3) * mm, "end": v(34.83, -193.32) * mm});
            skLineSegment(sketch, "E1438", {"start": v(34.83, -193.32) * mm, "end": v(33.95, -193.31) * mm});
            skLineSegment(sketch, "E1439", {"start": v(33.95, -193.31) * mm, "end": v(33.1, -193.28) * mm});
            skLineSegment(sketch, "E1440", {"start": v(33.1, -193.28) * mm, "end": v(32.25, -193.22) * mm});
            skLineSegment(sketch, "E1441", {"start": v(32.25, -193.22) * mm, "end": v(31.44, -193.14) * mm});
            skLineSegment(sketch, "E1442", {"start": v(31.44, -193.14) * mm, "end": v(30.64, -193.04) * mm});
            skLineSegment(sketch, "E1443", {"start": v(30.64, -193.04) * mm, "end": v(29.87, -192.91) * mm});
            skLineSegment(sketch, "E1444", {"start": v(29.87, -192.91) * mm, "end": v(29.11, -192.77) * mm});
            skLineSegment(sketch, "E1445", {"start": v(29.11, -192.77) * mm, "end": v(28.38, -192.6) * mm});
            skLineSegment(sketch, "E1446", {"start": v(28.38, -192.6) * mm, "end": v(27.67, -192.4) * mm});
            skLineSegment(sketch, "E1447", {"start": v(27.67, -192.4) * mm, "end": v(26.98, -192.2) * mm});
            skLineSegment(sketch, "E1448", {"start": v(26.98, -192.2) * mm, "end": v(26.3, -191.95) * mm});
            skLineSegment(sketch, "E1449", {"start": v(26.3, -191.95) * mm, "end": v(25.66, -191.7) * mm});
            skLineSegment(sketch, "E1450", {"start": v(25.66, -191.7) * mm, "end": v(25.03, -191.41) * mm});
            skLineSegment(sketch, "E1451", {"start": v(25.03, -191.41) * mm, "end": v(24.42, -191.1) * mm});
            skLineSegment(sketch, "E1452", {"start": v(24.42, -191.1) * mm, "end": v(23.83, -190.78) * mm});
            skLineSegment(sketch, "E1453", {"start": v(23.83, -190.78) * mm, "end": v(23.26, -190.43) * mm});
            skLineSegment(sketch, "E1454", {"start": v(23.26, -190.43) * mm, "end": v(22.71, -190.06) * mm});
            skLineSegment(sketch, "E1455", {"start": v(22.71, -190.06) * mm, "end": v(22.18, -189.66) * mm});
            skLineSegment(sketch, "E1456", {"start": v(22.18, -189.66) * mm, "end": v(21.67, -189.25) * mm});
            skLineSegment(sketch, "E1457", {"start": v(21.67, -189.25) * mm, "end": v(21.17, -188.82) * mm});
            skLineSegment(sketch, "E1458", {"start": v(21.17, -188.82) * mm, "end": v(20.69, -188.36) * mm});
            skLineSegment(sketch, "E1459", {"start": v(20.69, -188.36) * mm, "end": v(20.22, -187.9) * mm});
            skLineSegment(sketch, "E1460", {"start": v(20.22, -187.9) * mm, "end": v(19.77, -187.4) * mm});
            skLineSegment(sketch, "E1461", {"start": v(19.77, -187.4) * mm, "end": v(19.34, -186.88) * mm});
            skLineSegment(sketch, "E1462", {"start": v(19.34, -186.88) * mm, "end": v(18.92, -186.35) * mm});
            skLineSegment(sketch, "E1463", {"start": v(18.92, -186.35) * mm, "end": v(18.53, -185.8) * mm});
            skLineSegment(sketch, "E1464", {"start": v(18.53, -185.8) * mm, "end": v(18.14, -185.22) * mm});
            skLineSegment(sketch, "E1465", {"start": v(18.14, -185.22) * mm, "end": v(17.78, -184.63) * mm});
            skLineSegment(sketch, "E1466", {"start": v(17.78, -184.63) * mm, "end": v(17.43, -184.01) * mm});
            skLineSegment(sketch, "E1467", {"start": v(17.43, -184.01) * mm, "end": v(17.1, -183.38) * mm});
            skLineSegment(sketch, "E1468", {"start": v(17.1, -183.38) * mm, "end": v(16.78, -182.72) * mm});
            skLineSegment(sketch, "E1469", {"start": v(16.78, -182.72) * mm, "end": v(16.48, -182.04) * mm});
            skLineSegment(sketch, "E1470", {"start": v(16.48, -182.04) * mm, "end": v(16.2, -181.35) * mm});
            skLineSegment(sketch, "E1471", {"start": v(16.2, -181.35) * mm, "end": v(15.94, -180.66) * mm});
            skLineSegment(sketch, "E1472", {"start": v(15.94, -180.66) * mm, "end": v(15.7, -179.96) * mm});
            skLineSegment(sketch, "E1473", {"start": v(15.7, -179.96) * mm, "end": v(15.47, -179.25) * mm});
            skLineSegment(sketch, "E1474", {"start": v(15.47, -179.25) * mm, "end": v(15.26, -178.53) * mm});
            skLineSegment(sketch, "E1475", {"start": v(15.26, -178.53) * mm, "end": v(15.07, -177.81) * mm});
            skLineSegment(sketch, "E1476", {"start": v(15.07, -177.81) * mm, "end": v(14.9, -177.08) * mm});
            skLineSegment(sketch, "E1477", {"start": v(14.9, -177.08) * mm, "end": v(14.74, -176.35) * mm});
            skLineSegment(sketch, "E1478", {"start": v(14.74, -176.35) * mm, "end": v(14.6, -175.61) * mm});
            skLineSegment(sketch, "E1479", {"start": v(14.6, -175.61) * mm, "end": v(14.49, -174.87) * mm});
            skLineSegment(sketch, "E1480", {"start": v(14.49, -174.87) * mm, "end": v(14.39, -174.11) * mm});
            skLineSegment(sketch, "E1481", {"start": v(14.39, -174.11) * mm, "end": v(14.3, -173.35) * mm});
            skLineSegment(sketch, "E1482", {"start": v(14.3, -173.35) * mm, "end": v(14.24, -172.59) * mm});
            skLineSegment(sketch, "E1483", {"start": v(14.24, -172.59) * mm, "end": v(14.2, -171.82) * mm});
            skLineSegment(sketch, "E1484", {"start": v(14.2, -171.82) * mm, "end": v(14.17, -171.04) * mm});
            skLineSegment(sketch, "E1485", {"start": v(14.17, -171.04) * mm, "end": v(14.16, -170.25) * mm});
            skLineSegment(sketch, "E1486", {"start": v(14.16, -170.25) * mm, "end": v(14.17, -169.4) * mm});
            skLineSegment(sketch, "E1487", {"start": v(14.17, -169.4) * mm, "end": v(14.2, -168.56) * mm});
            skLineSegment(sketch, "E1488", {"start": v(14.2, -168.56) * mm, "end": v(14.25, -167.74) * mm});
            skLineSegment(sketch, "E1489", {"start": v(14.25, -167.74) * mm, "end": v(14.32, -166.93) * mm});
            skLineSegment(sketch, "E1490", {"start": v(14.32, -166.93) * mm, "end": v(14.41, -166.13) * mm});
            skLineSegment(sketch, "E1491", {"start": v(14.41, -166.13) * mm, "end": v(14.53, -165.35) * mm});
            skLineSegment(sketch, "E1492", {"start": v(14.53, -165.35) * mm, "end": v(14.66, -164.58) * mm});
            skLineSegment(sketch, "E1493", {"start": v(14.66, -164.58) * mm, "end": v(14.81, -163.82) * mm});
            skLineSegment(sketch, "E1494", {"start": v(14.81, -163.82) * mm, "end": v(14.99, -163.08) * mm});
            skLineSegment(sketch, "E1495", {"start": v(14.99, -163.08) * mm, "end": v(15.18, -162.35) * mm});
            skLineSegment(sketch, "E1496", {"start": v(15.18, -162.35) * mm, "end": v(15.4, -161.64) * mm});
            skLineSegment(sketch, "E1497", {"start": v(15.4, -161.64) * mm, "end": v(15.63, -160.94) * mm});
            skLineSegment(sketch, "E1498", {"start": v(15.63, -160.94) * mm, "end": v(15.9, -160.25) * mm});
            skLineSegment(sketch, "E1499", {"start": v(15.9, -160.25) * mm, "end": v(16.17, -159.58) * mm});
            skLineSegment(sketch, "E1500", {"start": v(16.17, -159.58) * mm, "end": v(16.47, -158.92) * mm});
            skLineSegment(sketch, "E1501", {"start": v(16.47, -158.92) * mm, "end": v(16.78, -158.27) * mm});
            skLineSegment(sketch, "E1502", {"start": v(16.78, -158.27) * mm, "end": v(17.12, -157.64) * mm});
            skLineSegment(sketch, "E1503", {"start": v(17.12, -157.64) * mm, "end": v(17.47, -157.03) * mm});
            skLineSegment(sketch, "E1504", {"start": v(17.47, -157.03) * mm, "end": v(17.85, -156.44) * mm});
            skLineSegment(sketch, "E1505", {"start": v(17.85, -156.44) * mm, "end": v(18.23, -155.87) * mm});
            skLineSegment(sketch, "E1506", {"start": v(18.23, -155.87) * mm, "end": v(18.64, -155.31) * mm});
            skLineSegment(sketch, "E1507", {"start": v(18.64, -155.31) * mm, "end": v(19.06, -154.78) * mm});
            skLineSegment(sketch, "E1508", {"start": v(19.06, -154.78) * mm, "end": v(19.5, -154.27) * mm});
            skLineSegment(sketch, "E1509", {"start": v(19.5, -154.27) * mm, "end": v(19.96, -153.77) * mm});
            skLineSegment(sketch, "E1510", {"start": v(19.96, -153.77) * mm, "end": v(20.44, -153.3) * mm});
            skLineSegment(sketch, "E1511", {"start": v(20.44, -153.3) * mm, "end": v(20.93, -152.84) * mm});
            skLineSegment(sketch, "E1512", {"start": v(20.93, -152.84) * mm, "end": v(21.44, -152.4) * mm});
            skLineSegment(sketch, "E1513", {"start": v(21.44, -152.4) * mm, "end": v(21.97, -151.98) * mm});
            skLineSegment(sketch, "E1514", {"start": v(21.97, -151.98) * mm, "end": v(22.51, -151.58) * mm});
            skLineSegment(sketch, "E1515", {"start": v(22.51, -151.58) * mm, "end": v(23.08, -151.2) * mm});
            skLineSegment(sketch, "E1516", {"start": v(23.08, -151.2) * mm, "end": v(23.66, -150.84) * mm});
            skLineSegment(sketch, "E1517", {"start": v(23.66, -150.84) * mm, "end": v(24.25, -150.5) * mm});
            skLineSegment(sketch, "E1518", {"start": v(24.25, -150.5) * mm, "end": v(24.86, -150.18) * mm});
            skLineSegment(sketch, "E1519", {"start": v(24.86, -150.18) * mm, "end": v(25.48, -149.88) * mm});
            skLineSegment(sketch, "E1520", {"start": v(25.48, -149.88) * mm, "end": v(26.1, -149.6) * mm});
            skLineSegment(sketch, "E1521", {"start": v(26.1, -149.6) * mm, "end": v(26.74, -149.34) * mm});
            skLineSegment(sketch, "E1522", {"start": v(26.74, -149.34) * mm, "end": v(27.38, -149.1) * mm});
            skLineSegment(sketch, "E1523", {"start": v(27.38, -149.1) * mm, "end": v(28.02, -148.88) * mm});
            skLineSegment(sketch, "E1524", {"start": v(28.02, -148.88) * mm, "end": v(28.68, -148.69) * mm});
            skLineSegment(sketch, "E1525", {"start": v(28.68, -148.69) * mm, "end": v(29.34, -148.51) * mm});
            skLineSegment(sketch, "E1526", {"start": v(29.34, -148.51) * mm, "end": v(30.01, -148.36) * mm});
            skLineSegment(sketch, "E1527", {"start": v(30.01, -148.36) * mm, "end": v(30.69, -148.22) * mm});
            skLineSegment(sketch, "E1528", {"start": v(30.69, -148.22) * mm, "end": v(31.37, -148.1) * mm});
            skLineSegment(sketch, "E1529", {"start": v(31.37, -148.1) * mm, "end": v(32.07, -148.01) * mm});
            skLineSegment(sketch, "E1530", {"start": v(32.07, -148.01) * mm, "end": v(32.77, -147.94) * mm});
            skLineSegment(sketch, "E1531", {"start": v(32.77, -147.94) * mm, "end": v(33.48, -147.89) * mm});
            skLineSegment(sketch, "E1532", {"start": v(33.48, -147.89) * mm, "end": v(34.2, -147.86) * mm});
            skLineSegment(sketch, "E1533", {"start": v(34.2, -147.86) * mm, "end": v(34.92, -147.85) * mm});
            skLineSegment(sketch, "E1534", {"start": v(34.92, -147.85) * mm, "end": v(35.73, -147.86) * mm});
            skLineSegment(sketch, "E1535", {"start": v(35.73, -147.86) * mm, "end": v(36.53, -147.9) * mm});
            skLineSegment(sketch, "E1536", {"start": v(36.53, -147.9) * mm, "end": v(37.32, -147.97) * mm});
            skLineSegment(sketch, "E1537", {"start": v(37.32, -147.97) * mm, "end": v(38.08, -148.06) * mm});
            skLineSegment(sketch, "E1538", {"start": v(38.08, -148.06) * mm, "end": v(38.84, -148.18) * mm});
            skLineSegment(sketch, "E1539", {"start": v(38.84, -148.18) * mm, "end": v(39.57, -148.32) * mm});
            skLineSegment(sketch, "E1540", {"start": v(39.57, -148.32) * mm, "end": v(40.29, -148.5) * mm});
            skLineSegment(sketch, "E1541", {"start": v(40.29, -148.5) * mm, "end": v(41, -148.69) * mm});
            skLineSegment(sketch, "E1542", {"start": v(41, -148.69) * mm, "end": v(41.68, -148.91) * mm});
            skLineSegment(sketch, "E1543", {"start": v(41.68, -148.91) * mm, "end": v(42.34, -149.16) * mm});
            skLineSegment(sketch, "E1544", {"start": v(42.34, -149.16) * mm, "end": v(43, -149.44) * mm});
            skLineSegment(sketch, "E1545", {"start": v(43, -149.44) * mm, "end": v(43.63, -149.74) * mm});
            skLineSegment(sketch, "E1546", {"start": v(43.63, -149.74) * mm, "end": v(44.25, -150.06) * mm});
            skLineSegment(sketch, "E1547", {"start": v(44.25, -150.06) * mm, "end": v(44.86, -150.42) * mm});
            skLineSegment(sketch, "E1548", {"start": v(44.86, -150.42) * mm, "end": v(45.44, -150.8) * mm});
            skLineSegment(sketch, "E1549", {"start": v(45.44, -150.8) * mm, "end": v(46.01, -151.2) * mm});
            skLineSegment(sketch, "E1550", {"start": v(46.01, -151.2) * mm, "end": v(46.57, -151.64) * mm});
            skLineSegment(sketch, "E1551", {"start": v(46.57, -151.64) * mm, "end": v(47.1, -152.09) * mm});
            skLineSegment(sketch, "E1552", {"start": v(47.1, -152.09) * mm, "end": v(47.6, -152.56) * mm});
            skLineSegment(sketch, "E1553", {"start": v(47.6, -152.56) * mm, "end": v(48.1, -153.06) * mm});
            skLineSegment(sketch, "E1554", {"start": v(48.1, -153.06) * mm, "end": v(48.56, -153.57) * mm});
            skLineSegment(sketch, "E1555", {"start": v(48.56, -153.57) * mm, "end": v(49, -154.11) * mm});
            skLineSegment(sketch, "E1556", {"start": v(49, -154.11) * mm, "end": v(49.43, -154.67) * mm});
            skLineSegment(sketch, "E1557", {"start": v(49.43, -154.67) * mm, "end": v(49.83, -155.25) * mm});
            skLineSegment(sketch, "E1558", {"start": v(49.83, -155.25) * mm, "end": v(50.21, -155.85) * mm});
            skLineSegment(sketch, "E1559", {"start": v(50.21, -155.85) * mm, "end": v(50.57, -156.47) * mm});
            skLineSegment(sketch, "E1560", {"start": v(50.57, -156.47) * mm, "end": v(50.91, -157.12) * mm});
            skLineSegment(sketch, "E1561", {"start": v(50.91, -157.12) * mm, "end": v(51.23, -157.78) * mm});
            skLineSegment(sketch, "E1562", {"start": v(51.23, -157.78) * mm, "end": v(51.52, -158.47) * mm});
            skLineSegment(sketch, "E1563", {"start": v(51.52, -158.47) * mm, "end": v(51.8, -159.18) * mm});
            skLineSegment(sketch, "E1564", {"start": v(51.8, -159.18) * mm, "end": v(52.05, -159.9) * mm});
            skLineSegment(sketch, "E1565", {"start": v(52.05, -159.9) * mm, "end": v(52.28, -160.66) * mm});
            skLineSegment(sketch, "E1566", {"start": v(52.28, -160.66) * mm, "end": v(46.55, -162) * mm});
            skLineSegment(sketch, "E1567", {"start": v(46.55, -162) * mm, "end": v(46.36, -161.42) * mm});
            skLineSegment(sketch, "E1568", {"start": v(46.36, -161.42) * mm, "end": v(46.15, -160.85) * mm});
            skLineSegment(sketch, "E1569", {"start": v(46.15, -160.85) * mm, "end": v(45.93, -160.3) * mm});
            skLineSegment(sketch, "E1570", {"start": v(45.93, -160.3) * mm, "end": v(45.7, -159.77) * mm});
            skLineSegment(sketch, "E1571", {"start": v(45.7, -159.77) * mm, "end": v(45.46, -159.26) * mm});
            skLineSegment(sketch, "E1572", {"start": v(45.46, -159.26) * mm, "end": v(45.21, -158.77) * mm});
            skLineSegment(sketch, "E1573", {"start": v(45.21, -158.77) * mm, "end": v(44.95, -158.3) * mm});
            skLineSegment(sketch, "E1574", {"start": v(44.95, -158.3) * mm, "end": v(44.68, -157.86) * mm});
            skLineSegment(sketch, "E1575", {"start": v(44.68, -157.86) * mm, "end": v(44.4, -157.43) * mm});
            skLineSegment(sketch, "E1576", {"start": v(44.4, -157.43) * mm, "end": v(44.1, -157.03) * mm});
            skLineSegment(sketch, "E1577", {"start": v(44.1, -157.03) * mm, "end": v(43.8, -156.64) * mm});
            skLineSegment(sketch, "E1578", {"start": v(43.8, -156.64) * mm, "end": v(43.48, -156.27) * mm});
            skLineSegment(sketch, "E1579", {"start": v(43.48, -156.27) * mm, "end": v(43.16, -155.93) * mm});
            skLineSegment(sketch, "E1580", {"start": v(43.16, -155.93) * mm, "end": v(42.82, -155.6) * mm});
            skLineSegment(sketch, "E1581", {"start": v(42.82, -155.6) * mm, "end": v(42.47, -155.3) * mm});
            skLineSegment(sketch, "E1582", {"start": v(42.47, -155.3) * mm, "end": v(42.12, -155.02) * mm});
            skLineSegment(sketch, "E1583", {"start": v(42.12, -155.02) * mm, "end": v(41.75, -154.75) * mm});
            skLineSegment(sketch, "E1584", {"start": v(41.75, -154.75) * mm, "end": v(41.36, -154.5) * mm});
            skLineSegment(sketch, "E1585", {"start": v(41.36, -154.5) * mm, "end": v(40.97, -154.27) * mm});
            skLineSegment(sketch, "E1586", {"start": v(40.97, -154.27) * mm, "end": v(40.57, -154.06) * mm});
            skLineSegment(sketch, "E1587", {"start": v(40.57, -154.06) * mm, "end": v(40.15, -153.86) * mm});
            skLineSegment(sketch, "E1588", {"start": v(40.15, -153.86) * mm, "end": v(39.72, -153.68) * mm});
            skLineSegment(sketch, "E1589", {"start": v(39.72, -153.68) * mm, "end": v(39.28, -153.52) * mm});
            skLineSegment(sketch, "E1590", {"start": v(39.28, -153.52) * mm, "end": v(38.83, -153.37) * mm});
            skLineSegment(sketch, "E1591", {"start": v(38.83, -153.37) * mm, "end": v(38.37, -153.25) * mm});
            skLineSegment(sketch, "E1592", {"start": v(38.37, -153.25) * mm, "end": v(37.9, -153.13) * mm});
            skLineSegment(sketch, "E1593", {"start": v(37.9, -153.13) * mm, "end": v(37.4, -153.04) * mm});
            skLineSegment(sketch, "E1594", {"start": v(37.4, -153.04) * mm, "end": v(36.9, -152.96) * mm});
            skLineSegment(sketch, "E1595", {"start": v(36.9, -152.96) * mm, "end": v(36.4, -152.9) * mm});
            skLineSegment(sketch, "E1596", {"start": v(36.4, -152.9) * mm, "end": v(35.88, -152.86) * mm});
            skLineSegment(sketch, "E1597", {"start": v(35.88, -152.86) * mm, "end": v(35.34, -152.84) * mm});
            skLineSegment(sketch, "E1598", {"start": v(35.34, -152.84) * mm, "end": v(34.8, -152.83) * mm});
            skLineSegment(sketch, "E1599", {"start": v(34.8, -152.83) * mm, "end": v(34.17, -152.84) * mm});
            skLineSegment(sketch, "E1600", {"start": v(34.17, -152.84) * mm, "end": v(33.55, -152.86) * mm});
            skLineSegment(sketch, "E1601", {"start": v(33.55, -152.86) * mm, "end": v(32.95, -152.91) * mm});
            skLineSegment(sketch, "E1602", {"start": v(32.95, -152.91) * mm, "end": v(32.37, -152.98) * mm});
            skLineSegment(sketch, "E1603", {"start": v(32.37, -152.98) * mm, "end": v(31.8, -153.06) * mm});
            skLineSegment(sketch, "E1604", {"start": v(31.8, -153.06) * mm, "end": v(31.23, -153.17) * mm});
            skLineSegment(sketch, "E1605", {"start": v(31.23, -153.17) * mm, "end": v(30.68, -153.3) * mm});
            skLineSegment(sketch, "E1606", {"start": v(30.68, -153.3) * mm, "end": v(30.14, -153.43) * mm});
            skLineSegment(sketch, "E1607", {"start": v(30.14, -153.43) * mm, "end": v(29.62, -153.6) * mm});
            skLineSegment(sketch, "E1608", {"start": v(29.62, -153.6) * mm, "end": v(29.1, -153.78) * mm});
            skLineSegment(sketch, "E1609", {"start": v(29.1, -153.78) * mm, "end": v(28.61, -153.97) * mm});
            skLineSegment(sketch, "E1610", {"start": v(28.61, -153.97) * mm, "end": v(28.13, -154.2) * mm});
            skLineSegment(sketch, "E1611", {"start": v(28.13, -154.2) * mm, "end": v(27.66, -154.43) * mm});
            skLineSegment(sketch, "E1612", {"start": v(27.66, -154.43) * mm, "end": v(27.2, -154.69) * mm});
            skLineSegment(sketch, "E1613", {"start": v(27.2, -154.69) * mm, "end": v(26.75, -154.96) * mm});
            skLineSegment(sketch, "E1614", {"start": v(26.75, -154.96) * mm, "end": v(26.32, -155.26) * mm});
            skLineSegment(sketch, "E1615", {"start": v(26.32, -155.26) * mm, "end": v(25.9, -155.57) * mm});
            skLineSegment(sketch, "E1616", {"start": v(25.9, -155.57) * mm, "end": v(25.5, -155.89) * mm});
            skLineSegment(sketch, "E1617", {"start": v(25.5, -155.89) * mm, "end": v(25.12, -156.23) * mm});
            skLineSegment(sketch, "E1618", {"start": v(25.12, -156.23) * mm, "end": v(24.75, -156.58) * mm});
            skLineSegment(sketch, "E1619", {"start": v(24.75, -156.58) * mm, "end": v(24.4, -156.94) * mm});
            skLineSegment(sketch, "E1620", {"start": v(24.4, -156.94) * mm, "end": v(24.05, -157.31) * mm});
            skLineSegment(sketch, "E1621", {"start": v(24.05, -157.31) * mm, "end": v(23.73, -157.7) * mm});
            skLineSegment(sketch, "E1622", {"start": v(23.73, -157.7) * mm, "end": v(23.42, -158.1) * mm});
            skLineSegment(sketch, "E1623", {"start": v(23.42, -158.1) * mm, "end": v(23.13, -158.52) * mm});
            skLineSegment(sketch, "E1624", {"start": v(23.13, -158.52) * mm, "end": v(22.86, -158.94) * mm});
            skLineSegment(sketch, "E1625", {"start": v(22.86, -158.94) * mm, "end": v(22.6, -159.38) * mm});
            skLineSegment(sketch, "E1626", {"start": v(22.6, -159.38) * mm, "end": v(22.35, -159.84) * mm});
            skLineSegment(sketch, "E1627", {"start": v(22.35, -159.84) * mm, "end": v(22.13, -160.3) * mm});
            skLineSegment(sketch, "E1628", {"start": v(22.13, -160.3) * mm, "end": v(21.91, -160.78) * mm});
            skLineSegment(sketch, "E1629", {"start": v(21.91, -160.78) * mm, "end": v(21.72, -161.28) * mm});
            skLineSegment(sketch, "E1630", {"start": v(21.72, -161.28) * mm, "end": v(21.54, -161.78) * mm});
            skLineSegment(sketch, "E1631", {"start": v(21.54, -161.78) * mm, "end": v(21.21, -162.8) * mm});
            skLineSegment(sketch, "E1632", {"start": v(21.21, -162.8) * mm, "end": v(20.93, -163.84) * mm});
            skLineSegment(sketch, "E1633", {"start": v(20.93, -163.84) * mm, "end": v(20.7, -164.89) * mm});
            skLineSegment(sketch, "E1634", {"start": v(20.7, -164.89) * mm, "end": v(20.5, -165.94) * mm});
            skLineSegment(sketch, "E1635", {"start": v(20.5, -165.94) * mm, "end": v(20.35, -167) * mm});
            skLineSegment(sketch, "E1636", {"start": v(20.35, -167) * mm, "end": v(20.24, -168.07) * mm});
            skLineSegment(sketch, "E1637", {"start": v(20.24, -168.07) * mm, "end": v(20.18, -169.14) * mm});
            skLineSegment(sketch, "E1638", {"start": v(20.18, -169.14) * mm, "end": v(20.16, -170.22) * mm});
            skLineSegment(sketch, "E1639", {"start": v(20.16, -170.22) * mm, "end": v(20.18, -171.6) * mm});
            skLineSegment(sketch, "E1640", {"start": v(20.18, -171.6) * mm, "end": v(20.26, -172.94) * mm});
            skLineSegment(sketch, "E1641", {"start": v(20.26, -172.94) * mm, "end": v(20.39, -174.23) * mm});
            skLineSegment(sketch, "E1642", {"start": v(20.39, -174.23) * mm, "end": v(20.57, -175.48) * mm});
            skLineSegment(sketch, "E1643", {"start": v(20.57, -175.48) * mm, "end": v(20.8, -176.68) * mm});
            skLineSegment(sketch, "E1644", {"start": v(20.8, -176.68) * mm, "end": v(21.08, -177.84) * mm});
            skLineSegment(sketch, "E1645", {"start": v(21.08, -177.84) * mm, "end": v(21.4, -178.95) * mm});
            skLineSegment(sketch, "E1646", {"start": v(21.4, -178.95) * mm, "end": v(21.8, -180.02) * mm});
            skLineSegment(sketch, "E1647", {"start": v(21.8, -180.02) * mm, "end": v(22, -180.53) * mm});
            skLineSegment(sketch, "E1648", {"start": v(22, -180.53) * mm, "end": v(22.23, -181.03) * mm});
            skLineSegment(sketch, "E1649", {"start": v(22.23, -181.03) * mm, "end": v(22.47, -181.51) * mm});
            skLineSegment(sketch, "E1650", {"start": v(22.47, -181.51) * mm, "end": v(22.72, -181.98) * mm});
            skLineSegment(sketch, "E1651", {"start": v(22.72, -181.98) * mm, "end": v(23, -182.43) * mm});
            skLineSegment(sketch, "E1652", {"start": v(23, -182.43) * mm, "end": v(23.27, -182.86) * mm});
            skLineSegment(sketch, "E1653", {"start": v(23.27, -182.86) * mm, "end": v(23.57, -183.28) * mm});
            skLineSegment(sketch, "E1654", {"start": v(23.57, -183.28) * mm, "end": v(23.88, -183.67) * mm});
            skLineSegment(sketch, "E1655", {"start": v(23.88, -183.67) * mm, "end": v(24.2, -184.06) * mm});
            skLineSegment(sketch, "E1656", {"start": v(24.2, -184.06) * mm, "end": v(24.54, -184.42) * mm});
            skLineSegment(sketch, "E1657", {"start": v(24.54, -184.42) * mm, "end": v(24.9, -184.77) * mm});
            skLineSegment(sketch, "E1658", {"start": v(24.9, -184.77) * mm, "end": v(25.27, -185.1) * mm});
            skLineSegment(sketch, "E1659", {"start": v(25.27, -185.1) * mm, "end": v(25.65, -185.42) * mm});
            skLineSegment(sketch, "E1660", {"start": v(25.65, -185.42) * mm, "end": v(26.04, -185.72) * mm});
            skLineSegment(sketch, "E1661", {"start": v(26.04, -185.72) * mm, "end": v(26.45, -186) * mm});
            skLineSegment(sketch, "E1662", {"start": v(26.45, -186) * mm, "end": v(26.88, -186.27) * mm});
            skLineSegment(sketch, "E1663", {"start": v(26.88, -186.27) * mm, "end": v(27.75, -186.76) * mm});
            skLineSegment(sketch, "E1664", {"start": v(27.75, -186.76) * mm, "end": v(28.64, -187.18) * mm});
            skLineSegment(sketch, "E1665", {"start": v(28.64, -187.18) * mm, "end": v(29.54, -187.53) * mm});
            skLineSegment(sketch, "E1666", {"start": v(29.54, -187.53) * mm, "end": v(30.47, -187.83) * mm});
            skLineSegment(sketch, "E1667", {"start": v(30.47, -187.83) * mm, "end": v(31.41, -188.05) * mm});
            skLineSegment(sketch, "E1668", {"start": v(31.41, -188.05) * mm, "end": v(32.37, -188.21) * mm});
            skLineSegment(sketch, "E1669", {"start": v(32.37, -188.21) * mm, "end": v(33.35, -188.31) * mm});
            skLineSegment(sketch, "E1670", {"start": v(33.35, -188.31) * mm, "end": v(34.35, -188.34) * mm});
            skLineSegment(sketch, "E1671", {"start": v(34.35, -188.34) * mm, "end": v(34.95, -188.33) * mm});
            skLineSegment(sketch, "E1672", {"start": v(34.95, -188.33) * mm, "end": v(35.55, -188.3) * mm});
            skLineSegment(sketch, "E1673", {"start": v(35.55, -188.3) * mm, "end": v(36.13, -188.24) * mm});
            skLineSegment(sketch, "E1674", {"start": v(36.13, -188.24) * mm, "end": v(36.7, -188.17) * mm});
            skLineSegment(sketch, "E1675", {"start": v(36.7, -188.17) * mm, "end": v(37.26, -188.07) * mm});
            skLineSegment(sketch, "E1676", {"start": v(37.26, -188.07) * mm, "end": v(37.8, -187.95) * mm});
            skLineSegment(sketch, "E1677", {"start": v(37.8, -187.95) * mm, "end": v(38.34, -187.8) * mm});
            skLineSegment(sketch, "E1678", {"start": v(38.34, -187.8) * mm, "end": v(38.86, -187.64) * mm});
            skLineSegment(sketch, "E1679", {"start": v(38.86, -187.64) * mm, "end": v(39.37, -187.45) * mm});
            skLineSegment(sketch, "E1680", {"start": v(39.37, -187.45) * mm, "end": v(39.87, -187.24) * mm});
            skLineSegment(sketch, "E1681", {"start": v(39.87, -187.24) * mm, "end": v(40.36, -187) * mm});
            skLineSegment(sketch, "E1682", {"start": v(40.36, -187) * mm, "end": v(40.84, -186.76) * mm});
            skLineSegment(sketch, "E1683", {"start": v(40.84, -186.76) * mm, "end": v(41.3, -186.48) * mm});
            skLineSegment(sketch, "E1684", {"start": v(41.3, -186.48) * mm, "end": v(41.75, -186.18) * mm});
            skLineSegment(sketch, "E1685", {"start": v(41.75, -186.18) * mm, "end": v(42.2, -185.86) * mm});
            skLineSegment(sketch, "E1686", {"start": v(42.2, -185.86) * mm, "end": v(42.63, -185.52) * mm});
            skLineSegment(sketch, "E1687", {"start": v(42.63, -185.52) * mm, "end": v(43.04, -185.16) * mm});
            skLineSegment(sketch, "E1688", {"start": v(43.04, -185.16) * mm, "end": v(43.44, -184.78) * mm});
            skLineSegment(sketch, "E1689", {"start": v(43.44, -184.78) * mm, "end": v(43.82, -184.37) * mm});
            skLineSegment(sketch, "E1690", {"start": v(43.82, -184.37) * mm, "end": v(44.18, -183.94) * mm});
            skLineSegment(sketch, "E1691", {"start": v(44.18, -183.94) * mm, "end": v(44.53, -183.5) * mm});
            skLineSegment(sketch, "E1692", {"start": v(44.53, -183.5) * mm, "end": v(44.86, -183.02) * mm});
            skLineSegment(sketch, "E1693", {"start": v(44.86, -183.02) * mm, "end": v(45.17, -182.53) * mm});
            skLineSegment(sketch, "E1694", {"start": v(45.17, -182.53) * mm, "end": v(45.47, -182.02) * mm});
            skLineSegment(sketch, "E1695", {"start": v(45.47, -182.02) * mm, "end": v(45.75, -181.49) * mm});
            skLineSegment(sketch, "E1696", {"start": v(45.75, -181.49) * mm, "end": v(46, -180.93) * mm});
            skLineSegment(sketch, "E1697", {"start": v(46, -180.93) * mm, "end": v(46.25, -180.36) * mm});
            skLineSegment(sketch, "E1698", {"start": v(46.25, -180.36) * mm, "end": v(46.48, -179.76) * mm});
            skLineSegment(sketch, "E1699", {"start": v(46.48, -179.76) * mm, "end": v(46.69, -179.14) * mm});
            skLineSegment(sketch, "E1700", {"start": v(46.69, -179.14) * mm, "end": v(46.88, -178.5) * mm});
            skLineSegment(sketch, "E1701", {"start": v(46.88, -178.5) * mm, "end": v(47.06, -177.84) * mm});
            skLineSegment(sketch, "E1702", {"start": v(-61.37, -192.57) * mm, "end": v(-66.77, -192.57) * mm});
            skLineSegment(sketch, "E1703", {"start": v(-66.77, -192.57) * mm, "end": v(-66.77, -148.6) * mm});
            skLineSegment(sketch, "E1704", {"start": v(-66.77, -148.6) * mm, "end": v(-61.37, -148.6) * mm});
            skLineSegment(sketch, "E1705", {"start": v(-61.37, -148.6) * mm, "end": v(-61.37, -173.67) * mm});
            skLineSegment(sketch, "E1706", {"start": v(-61.37, -173.67) * mm, "end": v(-48.6, -160.72) * mm});
            skLineSegment(sketch, "E1707", {"start": v(-48.6, -160.72) * mm, "end": v(-41.6, -160.72) * mm});
            skLineSegment(sketch, "E1708", {"start": v(-41.6, -160.72) * mm, "end": v(-53.78, -172.53) * mm});
            skLineSegment(sketch, "E1709", {"start": v(-53.78, -172.53) * mm, "end": v(-40.38, -192.57) * mm});
            skLineSegment(sketch, "E1710", {"start": v(-40.38, -192.57) * mm, "end": v(-47.03, -192.57) * mm});
            skLineSegment(sketch, "E1711", {"start": v(-47.03, -192.57) * mm, "end": v(-57.56, -176.28) * mm});
            skLineSegment(sketch, "E1712", {"start": v(-57.56, -176.28) * mm, "end": v(-61.37, -179.94) * mm});
            skLineSegment(sketch, "E1713", {"start": v(-61.37, -179.94) * mm, "end": v(-61.37, -192.57) * mm});
            skLineSegment(sketch, "E1714", {"start": v(-120.8, -192.57) * mm, "end": v(-126.62, -192.57) * mm});
            skLineSegment(sketch, "E1715", {"start": v(-126.62, -192.57) * mm, "end": v(-126.62, -153.79) * mm});
            skLineSegment(sketch, "E1716", {"start": v(-126.62, -153.79) * mm, "end": v(-141.1, -153.79) * mm});
            skLineSegment(sketch, "E1717", {"start": v(-141.1, -153.79) * mm, "end": v(-141.1, -148.6) * mm});
            skLineSegment(sketch, "E1718", {"start": v(-141.1, -148.6) * mm, "end": v(-106.25, -148.6) * mm});
            skLineSegment(sketch, "E1719", {"start": v(-106.25, -148.6) * mm, "end": v(-106.25, -153.79) * mm});
            skLineSegment(sketch, "E1720", {"start": v(-106.25, -153.79) * mm, "end": v(-120.8, -153.79) * mm});
            skLineSegment(sketch, "E1721", {"start": v(-120.8, -153.79) * mm, "end": v(-120.8, -192.57) * mm});
            skLineSegment(sketch, "E1722", {"start": v(-143.75, -213.3) * mm, "end": v(-143.75, -220.63) * mm});
            skLineSegment(sketch, "E1723", {"start": v(-143.75, -220.63) * mm, "end": v(-148.15, -220.63) * mm});
            skArc(sketch, "E1724", {"start": v(-148.15, -220.63) * mm, "mid": v(-153.33, -218.48) * mm, "end": v(-155.48, -213.3) * mm});
            skLineSegment(sketch, "E1725", {"start": v(-155.48, -213.3) * mm, "end": v(-155.48, -131.21) * mm});
            skArc(sketch, "E1726", {"start": v(-155.48, -131.21) * mm, "mid": v(-153.33, -126.03) * mm, "end": v(-148.15, -123.88) * mm});
            skLineSegment(sketch, "E1727", {"start": v(-148.15, -123.88) * mm, "end": v(-143.75, -123.88) * mm});
            skLineSegment(sketch, "E1728", {"start": v(-143.75, -131.21) * mm, "end": v(-143.75, -123.88) * mm});
            skArc(sketch, "E1729", {"start": v(-148.15, -135.61) * mm, "mid": v(-146.86, -132.5) * mm, "end": v(-143.75, -131.21) * mm});
            skLineSegment(sketch, "E1730", {"start": v(-148.15, -208.9) * mm, "end": v(-148.15, -135.61) * mm});
            skArc(sketch, "E1731", {"start": v(-143.75, -213.3) * mm, "mid": v(-146.86, -212.01) * mm, "end": v(-148.15, -208.9) * mm});
            skLineSegment(sketch, "E1732", {"start": v(-138.4, 77.9) * mm, "end": v(-143.58, 83.09) * mm});
            skLineSegment(sketch, "E1733", {"start": v(-143.58, 83.09) * mm, "end": v(-5.18, 221.48) * mm});
            skArc(sketch, "E1734", {"start": v(-5.18, 221.48) * mm, "mid": v(0, 223.63) * mm, "end": v(5.18, 221.48) * mm});
            skLineSegment(sketch, "E1735", {"start": v(5.18, 221.48) * mm, "end": v(8.3, 218.37) * mm});
            skLineSegment(sketch, "E1736", {"start": v(3.1, 213.2) * mm, "end": v(8.3, 218.37) * mm});
            skArc(sketch, "E1737", {"start": v(-3.1, 213.2) * mm, "mid": v(0, 214.48) * mm, "end": v(3.1, 213.2) * mm});
            skLineSegment(sketch, "E1738", {"start": v(-138.4, 77.9) * mm, "end": v(-3.1, 213.2) * mm});
            skSolve(sketch);
        }
        {
            var Q0;
            Q0=makeQuery(id+"F0.imprint","IMPRINT",FACE,{"disambiguationData":[TD([[makeQuery(id+"F0.imprint","IMPRINT",EDGE,{"derivedFrom":sQuery(id+"F0.wireOp",EDGE,"E0")}),-1.0]])]});
            extrude(context, id + "F1", {"entities" : qUnion([Q0]), "depth" : 3 * mm});
        }
    });
